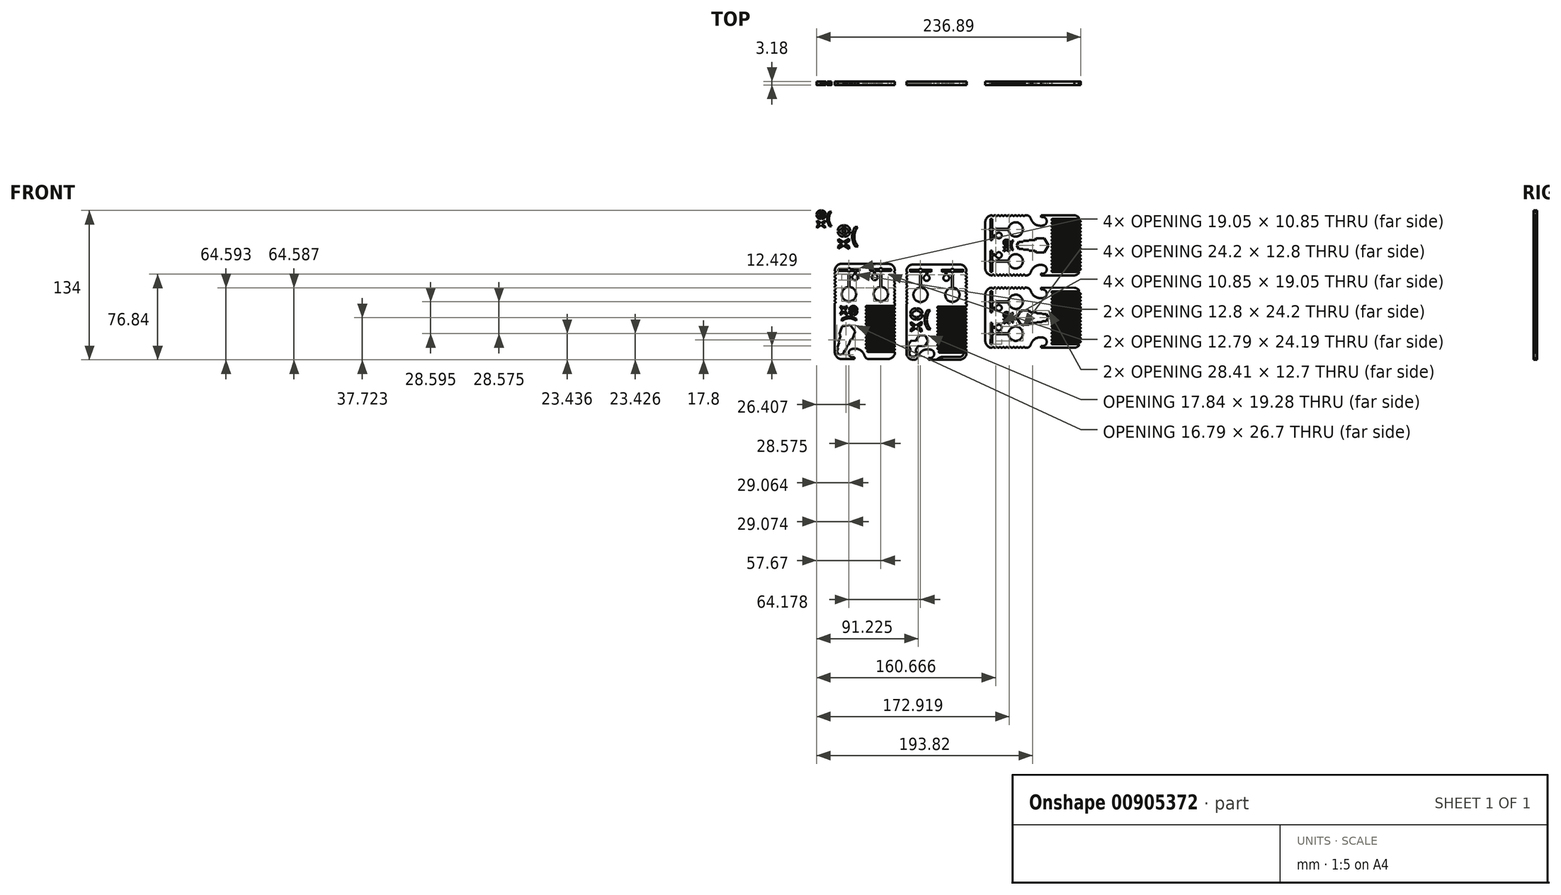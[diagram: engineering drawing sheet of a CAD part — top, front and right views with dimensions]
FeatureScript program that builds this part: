
annotation { "Feature Type Name" : "Feature", "Feature Type Description" : "" }
export const myFeature = defineFeature(function(context is Context, id is Id, definition is map)
    precondition{}
    {
        {
            var Q0;
            Q0=qCreatedBy(makeId("Front.planeOp"),FACE);
            var sketch = newSketch(context, id + "F0", { "sketchPlane" : qUnion([Q0])});
            skLineSegment(sketch, "E0.bottom", {"start": v(-20.64, 42.8) * mm, "end": v(20.64, 42.8) * mm});
            skLineSegment(sketch, "E0.top", {"start": v(-20.64, -42.8) * mm, "end": v(-20.41, -42.8) * mm});
            skLineSegment(sketch, "E0.left", {"start": v(-26.99, 34.92) * mm, "end": v(-26.99, 33.38) * mm});
            skLineSegment(sketch, "E0.right", {"start": v(26.99, 34.92) * mm, "end": v(26.99, 33.38) * mm});
            skArc(sketch, "E1.filletArc", {"start": v(-20.64, 42.8) * mm, "mid": v(-25.13, 40.94) * mm, "end": v(-26.99, 36.45) * mm});
            skArc(sketch, "E2.filletArc", {"start": v(26.99, 36.45) * mm, "mid": v(25.13, 40.94) * mm, "end": v(20.64, 42.8) * mm});
            skPoint(sketch, "E3.visualSharp", {"position": v(26.99, -42.8) * mm});
            skArc(sketch, "E3.filletArc", {"start": v(20.64, -42.8) * mm, "mid": v(24.88, -41.17) * mm, "end": v(26.95, -37.12) * mm});
            skPoint(sketch, "E4.visualSharp", {"position": v(-26.99, -42.8) * mm});
            skArc(sketch, "E4.filletArc", {"start": v(-26.99, -36.45) * mm, "mid": v(-25.13, -40.94) * mm, "end": v(-20.64, -42.8) * mm});
            skLineSegment(sketch, "E5", {"start": v(-23.81, 36.45) * mm, "end": v(-23.81, 38.04) * mm});
            skLineSegment(sketch, "E6", {"start": v(-23.81, 38.04) * mm, "end": v(-15.89, 38.04) * mm});
            skLineSegment(sketch, "E7", {"start": v(-4.76, 38.04) * mm, "end": v(-4.76, 36.45) * mm});
            skLineSegment(sketch, "E8.MirrorCS", {"start": v(4.76, 38.04) * mm, "end": v(4.76, 36.45) * mm});
            skLineSegment(sketch, "E9.MirrorCS", {"start": v(23.81, 38.04) * mm, "end": v(15.89, 38.04) * mm});
            skLineSegment(sketch, "E10.MirrorCS", {"start": v(23.81, 36.45) * mm, "end": v(23.81, 38.04) * mm});
            skLineSegment(sketch, "E11", {"start": v(-26.99, -21.76) * mm, "end": v(-26.99, -13.82) * mm});
            skLineSegment(sketch, "E12", {"start": v(-26.99, -21.76) * mm, "end": v(-26.99, -26.81) * mm});
            skLineSegment(sketch, "E13", {"start": v(-26.99, -29.7) * mm, "end": v(-26.99, -21.76) * mm});
            skPoint(sketch, "E14.orphan", {"position": v(4.76, 36.45) * mm});
            skPoint(sketch, "E15.MirrorCS.end.orphan", {"position": v(23.81, 36.45) * mm});
            skLineSegment(sketch, "E16", {"start": v(4.76, 36.45) * mm, "end": v(8.29, 36.45) * mm});
            skPoint(sketch, "E17.center.orphan", {"position": v(0, -42.8) * mm});
            skLineSegment(sketch, "E18", {"start": v(-23.81, 36.45) * mm, "end": v(-15.68, 36.45) * mm});
            skLineSegment(sketch, "E19.trimOffspring", {"start": v(-7.21, -42.8) * mm, "end": v(20.64, -42.8) * mm});
            skLineSegment(sketch, "E20.MirrorCS", {"start": v(15.06, 25.6) * mm, "end": v(15.06, 25.6) * mm});
            skLineSegment(sketch, "E21.MirrorCS", {"start": v(13.53, 25.6) * mm, "end": v(13.53, 25.6) * mm});
            skLineSegment(sketch, "E22.MirrorCS", {"start": v(13.86, 33.27) * mm, "end": v(14.75, 33.27) * mm});
            skArc(sketch, "E23", {"start": v(-8.11, 1.8) * mm, "mid": v(-10.63, -6.86) * mm, "end": v(-7.86, -15.46) * mm});
            skLineSegment(sketch, "E24.MirrorCS", {"start": v(-13.53, 25.6) * mm, "end": v(-13.53, 25.6) * mm});
            skLineSegment(sketch, "E25.MirrorCS", {"start": v(-15.06, 25.6) * mm, "end": v(-15.06, 25.6) * mm});
            skLineSegment(sketch, "E26.MirrorCS", {"start": v(-13.86, 33.27) * mm, "end": v(-14.75, 33.27) * mm});
            skArc(sketch, "E27", {"start": v(-20.67, -3.67) * mm, "mid": v(-19.53, -4.17) * mm, "end": v(-18.32, -4.4) * mm});
            skArc(sketch, "E28", {"start": v(-16.35, -4.22) * mm, "mid": v(-14.97, -3.48) * mm, "end": v(-14.3, -2.06) * mm});
            skArc(sketch, "E29", {"start": v(-23.46, -2.07) * mm, "mid": v(-23.38, -2.77) * mm, "end": v(-23.23, -3.46) * mm});
            skArc(sketch, "E30", {"start": v(-23.23, -3.46) * mm, "mid": v(-22.88, -4.33) * mm, "end": v(-22.36, -5.1) * mm});
            skArc(sketch, "E31", {"start": v(-22.36, -5.1) * mm, "mid": v(-21.57, -5.81) * mm, "end": v(-20.63, -6.31) * mm});
            skArc(sketch, "E32", {"start": v(-20.63, -6.31) * mm, "mid": v(-19.5, -6.64) * mm, "end": v(-18.32, -6.76) * mm});
            skArc(sketch, "E33", {"start": v(-18.32, -6.76) * mm, "mid": v(-18.31, -6.76) * mm, "end": v(-18.3, -6.76) * mm});
            skArc(sketch, "E34", {"start": v(-16.68, -6.69) * mm, "mid": v(-15.91, -6.55) * mm, "end": v(-15.17, -6.3) * mm});
            skArc(sketch, "E35", {"start": v(-15.17, -6.3) * mm, "mid": v(-14.58, -6.02) * mm, "end": v(-14.05, -5.65) * mm});
            skArc(sketch, "E36", {"start": v(-14.05, -5.65) * mm, "mid": v(-13.51, -5.13) * mm, "end": v(-13.08, -4.53) * mm});
            skArc(sketch, "E37", {"start": v(-13.08, -4.53) * mm, "mid": v(-12.75, -3.84) * mm, "end": v(-12.54, -3.1) * mm});
            skArc(sketch, "E38", {"start": v(-12.54, -3.1) * mm, "mid": v(-12.45, -2.62) * mm, "end": v(-12.4, -2.15) * mm});
            skArc(sketch, "E39", {"start": v(-12.4, -2.15) * mm, "mid": v(-12.4, -2.1) * mm, "end": v(-12.4, -2.06) * mm});
            skLineSegment(sketch, "E40", {"start": v(-21.55, -1.68) * mm, "end": v(-21.56, -1.68) * mm});
            skLineSegment(sketch, "E41", {"start": v(-14.29, -1.66) * mm, "end": v(-14.27, -1.66) * mm});
            skLineSegment(sketch, "E42.trimOffspring", {"start": v(-21.52, -2.06) * mm, "end": v(-23.46, -2.07) * mm});
            skLineSegment(sketch, "E43", {"start": v(-13.36, -2.06) * mm, "end": v(-12.4, -2.06) * mm});
            skArc(sketch, "E44.trimOffspring", {"start": v(-12.4, -1.66) * mm, "mid": v(-12.4, -1.65) * mm, "end": v(-12.4, -1.64) * mm});
            skLineSegment(sketch, "E45.trimOffspring", {"start": v(-14.3, -2.06) * mm, "end": v(-13.36, -2.06) * mm});
            skArc(sketch, "E46.trimOffspring", {"start": v(-21.52, -2.06) * mm, "mid": v(-21.23, -2.94) * mm, "end": v(-20.67, -3.67) * mm});
            skPoint(sketch, "E47.orphan", {"position": v(-17.78, -4.43) * mm});
            skLineSegment(sketch, "E48", {"start": v(-21.56, -1.68) * mm, "end": v(-21.55, -1.68) * mm});
            skArc(sketch, "E49.MirrorCS", {"start": v(-21.53, -1.3) * mm, "mid": v(-21.24, -0.42) * mm, "end": v(-20.68, 0.32) * mm});
            skArc(sketch, "E50.MirrorCS", {"start": v(-20.68, 0.32) * mm, "mid": v(-19.56, 0.83) * mm, "end": v(-18.35, 1.08) * mm});
            skArc(sketch, "E51.MirrorCS", {"start": v(-16.37, 0.9) * mm, "mid": v(-14.99, 0.18) * mm, "end": v(-14.3, -1.23) * mm});
            skArc(sketch, "E52.MirrorCS", {"start": v(-12.41, -1.13) * mm, "mid": v(-12.41, -1.17) * mm, "end": v(-12.4, -1.21) * mm});
            skArc(sketch, "E53.MirrorCS", {"start": v(-12.56, -0.18) * mm, "mid": v(-12.46, -0.65) * mm, "end": v(-12.41, -1.13) * mm});
            skArc(sketch, "E54.MirrorCS", {"start": v(-13.1, 1.25) * mm, "mid": v(-12.77, 0.56) * mm, "end": v(-12.56, -0.18) * mm});
            skArc(sketch, "E55.MirrorCS", {"start": v(-14.09, 2.36) * mm, "mid": v(-13.55, 1.85) * mm, "end": v(-13.1, 1.25) * mm});
            skArc(sketch, "E56.MirrorCS", {"start": v(-15.21, 3) * mm, "mid": v(-14.63, 2.72) * mm, "end": v(-14.09, 2.36) * mm});
            skArc(sketch, "E57.MirrorCS", {"start": v(-16.73, 3.37) * mm, "mid": v(-15.96, 3.24) * mm, "end": v(-15.21, 3) * mm});
            skArc(sketch, "E58.MirrorCS", {"start": v(-18.37, 3.43) * mm, "mid": v(-18.36, 3.43) * mm, "end": v(-18.36, 3.43) * mm});
            skArc(sketch, "E59.MirrorCS", {"start": v(-20.67, 2.96) * mm, "mid": v(-19.54, 3.3) * mm, "end": v(-18.37, 3.43) * mm});
            skArc(sketch, "E60.MirrorCS", {"start": v(-22.4, 1.73) * mm, "mid": v(-21.6, 2.45) * mm, "end": v(-20.67, 2.96) * mm});
            skArc(sketch, "E61.MirrorCS", {"start": v(-23.25, 0.09) * mm, "mid": v(-22.9, 0.95) * mm, "end": v(-22.4, 1.73) * mm});
            skArc(sketch, "E62.MirrorCS", {"start": v(-23.46, -1.3) * mm, "mid": v(-23.4, -0.6) * mm, "end": v(-23.25, 0.09) * mm});
            skLineSegment(sketch, "E63.MirrorCS", {"start": v(-21.53, -1.3) * mm, "end": v(-23.47, -1.3) * mm});
            skLineSegment(sketch, "E64.MirrorCS", {"start": v(-14.3, -1.23) * mm, "end": v(-13.36, -1.22) * mm});
            skLineSegment(sketch, "E65.MirrorCS", {"start": v(-13.36, -1.22) * mm, "end": v(-12.4, -1.21) * mm});
            skArc(sketch, "E66", {"start": v(-14.27, -1.66) * mm, "mid": v(-14.27, -1.65) * mm, "end": v(-14.27, -1.65) * mm});
            skLineSegment(sketch, "E67.0", {"start": v(-17.55, -6.77) * mm, "end": v(-17.56, -4.42) * mm});
            skLineSegment(sketch, "E68.0", {"start": v(-18.3, -6.77) * mm, "end": v(-18.32, -4.4) * mm});
            skLineSegment(sketch, "E69.trimOffspring", {"start": v(-18.35, 1.08) * mm, "end": v(-18.36, 3.44) * mm});
            skPoint(sketch, "E70.orphan", {"position": v(-17.93, -1.66) * mm});
            skLineSegment(sketch, "E71.trimOffspring", {"start": v(-17.58, 1.1) * mm, "end": v(-17.6, 3.45) * mm});
            skPoint(sketch, "E72.MirrorCS.end.orphan", {"position": v(-14.27, -1.64) * mm});
            skPoint(sketch, "E72.MirrorCS.start.orphan", {"position": v(-14.3, -1.23) * mm});
            skPoint(sketch, "E73.MirrorCS.end.orphan", {"position": v(-12.4, -0.88) * mm});
            skPoint(sketch, "E73.MirrorCS.start.orphan", {"position": v(-12.4, -0.45) * mm});
            skPoint(sketch, "E74.orphan", {"position": v(-23.47, -1.69) * mm});
            skPoint(sketch, "E75.MirrorCS.end.orphan", {"position": v(-21.53, -1.3) * mm});
            skArc(sketch, "E76.trimOffspring", {"start": v(-17.55, -6.77) * mm, "mid": v(-17.11, -6.74) * mm, "end": v(-16.68, -6.69) * mm});
            skArc(sketch, "E77.trimOffspring", {"start": v(-17.56, -4.42) * mm, "mid": v(-16.95, -4.35) * mm, "end": v(-16.35, -4.22) * mm});
            skArc(sketch, "E78.trimOffspring", {"start": v(-17.58, 1.1) * mm, "mid": v(-16.97, 1.03) * mm, "end": v(-16.37, 0.9) * mm});
            skArc(sketch, "E79.trimOffspring", {"start": v(-17.6, 3.44) * mm, "mid": v(-17.16, 3.42) * mm, "end": v(-16.73, 3.37) * mm});
            skText(sketch, "E80", { "text": "X", "fontName": "OpenSans-Bold.ttf"});
            skArc(sketch, "E81", {"start": v(-7.21, -41) * mm, "mid": v(-2.22, -38.57) * mm, "end": v(-4.96, -33.74) * mm});
            skArc(sketch, "E82", {"start": v(-20.41, -42.8) * mm, "mid": v(-17.8, -41.93) * mm, "end": v(-16.25, -39.67) * mm});
            skArc(sketch, "E83", {"start": v(-4.96, -33.74) * mm, "mid": v(-10.34, -33.76) * mm, "end": v(-14.8, -36.76) * mm});
            skArc(sketch, "E84", {"start": v(-14.8, -36.76) * mm, "mid": v(-15.63, -38.17) * mm, "end": v(-16.25, -39.67) * mm});
            skLineSegment(sketch, "E85", {"start": v(-7.21, -41) * mm, "end": v(-7.21, -42.8) * mm});
            skLineSegment(sketch, "E86", {"start": v(-13.54, 21.83) * mm, "end": v(-13.53, 21.83) * mm});
            skLineSegment(sketch, "E87", {"start": v(26.99, 6.39) * mm, "end": v(26.99, 7.32) * mm});
            skLineSegment(sketch, "E88", {"start": v(2.84, -34.92) * mm, "end": v(26.23, -34.92) * mm});
            skArc(sketch, "E89", {"start": v(26.23, -34.92) * mm, "mid": v(26.99, -34.16) * mm, "end": v(26.23, -33.39) * mm});
            skLineSegment(sketch, "E90", {"start": v(26.23, -33.39) * mm, "end": v(1.59, -33.39) * mm});
            skArc(sketch, "E91", {"start": v(26.95, -37.12) * mm, "mid": v(26.72, -36.65) * mm, "end": v(26.22, -36.45) * mm});
            skPoint(sketch, "E92.start.orphan", {"position": v(26.99, -36.45) * mm});
            skArc(sketch, "E93", {"start": v(2.84, -34.92) * mm, "mid": v(2.09, -35.69) * mm, "end": v(2.84, -36.45) * mm});
            skLineSegment(sketch, "E94", {"start": v(2.84, -36.45) * mm, "end": v(26.22, -36.45) * mm});
            skArc(sketch, "E95", {"start": v(1.59, -31.86) * mm, "mid": v(0.83, -32.62) * mm, "end": v(1.59, -33.39) * mm});
            skLineSegment(sketch, "E96", {"start": v(1.59, -31.86) * mm, "end": v(26.23, -31.86) * mm});
            skArc(sketch, "E97", {"start": v(26.23, -31.86) * mm, "mid": v(26.99, -31.09) * mm, "end": v(26.23, -30.32) * mm});
            skLineSegment(sketch, "E98", {"start": v(26.23, -30.32) * mm, "end": v(1.59, -30.32) * mm});
            skLineSegment(sketch, "E99", {"start": v(1.59, -28.8) * mm, "end": v(26.23, -28.8) * mm});
            skArc(sketch, "E100", {"start": v(26.23, -28.8) * mm, "mid": v(26.99, -28.02) * mm, "end": v(26.23, -27.26) * mm});
            skLineSegment(sketch, "E101", {"start": v(26.23, -27.26) * mm, "end": v(1.59, -27.26) * mm});
            skArc(sketch, "E102", {"start": v(1.59, -25.72) * mm, "mid": v(0.83, -26.5) * mm, "end": v(1.59, -27.26) * mm});
            skLineSegment(sketch, "E103", {"start": v(1.59, -25.72) * mm, "end": v(26.23, -25.72) * mm});
            skArc(sketch, "E104", {"start": v(26.23, -25.72) * mm, "mid": v(26.99, -24.96) * mm, "end": v(26.23, -24.2) * mm});
            skLineSegment(sketch, "E105", {"start": v(26.23, -24.2) * mm, "end": v(1.59, -24.2) * mm});
            skLineSegment(sketch, "E106", {"start": v(1.59, -22.66) * mm, "end": v(26.23, -22.66) * mm});
            skArc(sketch, "E107", {"start": v(26.23, -22.66) * mm, "mid": v(26.99, -21.9) * mm, "end": v(26.23, -21.13) * mm});
            skLineSegment(sketch, "E108", {"start": v(26.23, -21.13) * mm, "end": v(1.59, -21.13) * mm});
            skArc(sketch, "E109", {"start": v(1.59, -22.66) * mm, "mid": v(0.83, -23.43) * mm, "end": v(1.59, -24.2) * mm});
            skArc(sketch, "E110", {"start": v(1.59, -19.6) * mm, "mid": v(0.83, -20.36) * mm, "end": v(1.59, -21.13) * mm});
            skLineSegment(sketch, "E111", {"start": v(1.59, -19.6) * mm, "end": v(26.23, -19.6) * mm});
            skArc(sketch, "E112", {"start": v(26.23, -19.6) * mm, "mid": v(26.99, -18.83) * mm, "end": v(26.23, -18.06) * mm});
            skLineSegment(sketch, "E113", {"start": v(26.23, -18.06) * mm, "end": v(1.59, -18.06) * mm});
            skArc(sketch, "E114", {"start": v(1.59, -16.53) * mm, "mid": v(0.83, -17.3) * mm, "end": v(1.59, -18.06) * mm});
            skLineSegment(sketch, "E115", {"start": v(1.59, -16.53) * mm, "end": v(26.23, -16.53) * mm});
            skArc(sketch, "E116", {"start": v(26.23, -16.53) * mm, "mid": v(26.99, -15.76) * mm, "end": v(26.23, -15) * mm});
            skLineSegment(sketch, "E117", {"start": v(26.23, -15) * mm, "end": v(1.59, -15) * mm});
            skArc(sketch, "E118", {"start": v(1.59, -13.46) * mm, "mid": v(0.83, -14.23) * mm, "end": v(1.59, -15) * mm});
            skLineSegment(sketch, "E119", {"start": v(1.59, -13.46) * mm, "end": v(26.23, -13.46) * mm});
            skArc(sketch, "E120", {"start": v(26.23, -13.46) * mm, "mid": v(26.99, -12.7) * mm, "end": v(26.23, -11.93) * mm});
            skLineSegment(sketch, "E121", {"start": v(26.23, -11.93) * mm, "end": v(1.59, -11.93) * mm});
            skArc(sketch, "E122", {"start": v(1.59, -10.4) * mm, "mid": v(0.83, -11.16) * mm, "end": v(1.59, -11.93) * mm});
            skLineSegment(sketch, "E123", {"start": v(1.59, -10.4) * mm, "end": v(26.23, -10.4) * mm});
            skArc(sketch, "E124", {"start": v(26.23, -10.4) * mm, "mid": v(26.99, -9.63) * mm, "end": v(26.23, -8.86) * mm});
            skLineSegment(sketch, "E125", {"start": v(26.23, -8.86) * mm, "end": v(1.59, -8.86) * mm});
            skArc(sketch, "E126", {"start": v(1.59, -7.33) * mm, "mid": v(0.83, -8.1) * mm, "end": v(1.59, -8.86) * mm});
            skLineSegment(sketch, "E127", {"start": v(1.59, -7.33) * mm, "end": v(26.23, -7.33) * mm});
            skArc(sketch, "E128", {"start": v(26.23, -7.33) * mm, "mid": v(26.99, -6.56) * mm, "end": v(26.23, -5.8) * mm});
            skLineSegment(sketch, "E129", {"start": v(26.23, -5.8) * mm, "end": v(1.59, -5.8) * mm});
            skArc(sketch, "E130", {"start": v(1.59, -4.26) * mm, "mid": v(0.83, -5.03) * mm, "end": v(1.59, -5.8) * mm});
            skLineSegment(sketch, "E131", {"start": v(1.59, -4.26) * mm, "end": v(26.23, -4.26) * mm});
            skArc(sketch, "E132", {"start": v(26.23, -4.26) * mm, "mid": v(26.99, -3.5) * mm, "end": v(26.23, -2.73) * mm});
            skLineSegment(sketch, "E133", {"start": v(26.23, -2.73) * mm, "end": v(1.59, -2.73) * mm});
            skArc(sketch, "E134", {"start": v(1.59, -1.2) * mm, "mid": v(0.83, -1.97) * mm, "end": v(1.59, -2.73) * mm});
            skLineSegment(sketch, "E135", {"start": v(1.59, -1.2) * mm, "end": v(26.23, -1.2) * mm});
            skArc(sketch, "E136", {"start": v(26.23, -1.2) * mm, "mid": v(26.99, -0.43) * mm, "end": v(26.23, 0.33) * mm});
            skLineSegment(sketch, "E137", {"start": v(26.23, 0.33) * mm, "end": v(1.59, 0.33) * mm});
            skArc(sketch, "E138", {"start": v(1.59, 1.87) * mm, "mid": v(0.83, 1.1) * mm, "end": v(1.59, 0.33) * mm});
            skLineSegment(sketch, "E139", {"start": v(1.59, 1.87) * mm, "end": v(26.23, 1.87) * mm});
            skArc(sketch, "E140", {"start": v(26.23, 1.87) * mm, "mid": v(26.99, 2.63) * mm, "end": v(26.23, 3.4) * mm});
            skLineSegment(sketch, "E141", {"start": v(26.23, 3.4) * mm, "end": v(1.59, 3.4) * mm});
            skArc(sketch, "E142", {"start": v(1.59, 4.93) * mm, "mid": v(0.83, 4.17) * mm, "end": v(1.59, 3.4) * mm});
            skLineSegment(sketch, "E143", {"start": v(1.59, 4.93) * mm, "end": v(26.23, 4.93) * mm});
            skArc(sketch, "E144", {"start": v(26.23, 4.93) * mm, "mid": v(26.77, 5.16) * mm, "end": v(26.99, 5.7) * mm});
            skLineSegment(sketch, "E145", {"start": v(26.99, 5.7) * mm, "end": v(26.99, 6.39) * mm});
            skLineSegment(sketch, "E146.0", {"start": v(-14.75, 33.27) * mm, "end": v(-14.75, 22.45) * mm});
            skLineSegment(sketch, "E147.0", {"start": v(-13.86, 33.27) * mm, "end": v(-13.86, 22.45) * mm});
            skLineSegment(sketch, "E148.0", {"start": v(13.86, 33.27) * mm, "end": v(13.86, 22.45) * mm});
            skLineSegment(sketch, "E149.0", {"start": v(14.75, 33.27) * mm, "end": v(14.75, 22.45) * mm});
            skArc(sketch, "E150", {"start": v(13.3, 21.82) * mm, "mid": v(14.33, 9.08) * mm, "end": v(15.27, 21.83) * mm});
            skArc(sketch, "E151", {"start": v(-15.3, 21.82) * mm, "mid": v(-14.28, 9.07) * mm, "end": v(-13.32, 21.83) * mm});
            skArc(sketch, "E152", {"start": v(-26.99, 7.32) * mm, "mid": v(-26.23, 8.1) * mm, "end": v(-26.99, 8.86) * mm});
            skArc(sketch, "E153", {"start": v(-26.99, 10.4) * mm, "mid": v(-26.23, 11.16) * mm, "end": v(-26.99, 11.92) * mm});
            skArc(sketch, "E154", {"start": v(-26.99, 13.46) * mm, "mid": v(-26.23, 14.22) * mm, "end": v(-26.99, 14.99) * mm});
            skArc(sketch, "E155", {"start": v(-26.99, 16.52) * mm, "mid": v(-26.23, 17.29) * mm, "end": v(-26.99, 18.05) * mm});
            skArc(sketch, "E156", {"start": v(-26.99, 19.59) * mm, "mid": v(-26.23, 20.35) * mm, "end": v(-26.99, 21.12) * mm});
            skArc(sketch, "E157", {"start": v(-26.99, 22.65) * mm, "mid": v(-26.23, 23.42) * mm, "end": v(-26.99, 24.19) * mm});
            skArc(sketch, "E158", {"start": v(-26.99, 25.72) * mm, "mid": v(-26.23, 26.49) * mm, "end": v(-26.99, 27.25) * mm});
            skArc(sketch, "E159", {"start": v(-26.99, 28.78) * mm, "mid": v(-26.23, 29.55) * mm, "end": v(-26.99, 30.32) * mm});
            skArc(sketch, "E160", {"start": v(-26.99, 31.85) * mm, "mid": v(-26.23, 32.62) * mm, "end": v(-26.99, 33.38) * mm});
            skArc(sketch, "E161", {"start": v(-26.99, 34.92) * mm, "mid": v(-26.23, 35.68) * mm, "end": v(-26.99, 36.45) * mm});
            skArc(sketch, "E162", {"start": v(26.99, 8.86) * mm, "mid": v(26.23, 8.1) * mm, "end": v(26.99, 7.32) * mm});
            skArc(sketch, "E163", {"start": v(26.99, 11.92) * mm, "mid": v(26.23, 11.16) * mm, "end": v(26.99, 10.4) * mm});
            skArc(sketch, "E164", {"start": v(26.99, 14.99) * mm, "mid": v(26.23, 14.22) * mm, "end": v(26.99, 13.46) * mm});
            skArc(sketch, "E165", {"start": v(26.99, 18.05) * mm, "mid": v(26.23, 17.29) * mm, "end": v(26.99, 16.52) * mm});
            skArc(sketch, "E166", {"start": v(26.99, 21.12) * mm, "mid": v(26.23, 20.35) * mm, "end": v(26.99, 19.59) * mm});
            skArc(sketch, "E167", {"start": v(26.99, 24.19) * mm, "mid": v(26.23, 23.42) * mm, "end": v(26.99, 22.65) * mm});
            skArc(sketch, "E168", {"start": v(26.99, 27.25) * mm, "mid": v(26.23, 26.49) * mm, "end": v(26.99, 25.72) * mm});
            skArc(sketch, "E169", {"start": v(26.99, 30.32) * mm, "mid": v(26.23, 29.55) * mm, "end": v(26.99, 28.78) * mm});
            skArc(sketch, "E170", {"start": v(26.99, 33.38) * mm, "mid": v(26.23, 32.62) * mm, "end": v(26.99, 31.85) * mm});
            skArc(sketch, "E171", {"start": v(26.99, 36.45) * mm, "mid": v(26.23, 35.68) * mm, "end": v(26.99, 34.92) * mm});
            skLineSegment(sketch, "E172.trimOffspring", {"start": v(-26.99, 7.32) * mm, "end": v(-26.99, -36.45) * mm});
            skLineSegment(sketch, "E173.trimOffspring", {"start": v(-26.99, 10.4) * mm, "end": v(-26.99, 8.86) * mm});
            skLineSegment(sketch, "E174.trimOffspring", {"start": v(-26.99, 13.46) * mm, "end": v(-26.99, 11.92) * mm});
            skLineSegment(sketch, "E175.trimOffspring", {"start": v(-26.99, 16.52) * mm, "end": v(-26.99, 14.99) * mm});
            skLineSegment(sketch, "E176.trimOffspring", {"start": v(-26.99, 19.59) * mm, "end": v(-26.99, 18.05) * mm});
            skLineSegment(sketch, "E177.trimOffspring", {"start": v(-26.99, 22.65) * mm, "end": v(-26.99, 21.12) * mm});
            skLineSegment(sketch, "E178.trimOffspring", {"start": v(-26.99, 25.72) * mm, "end": v(-26.99, 24.19) * mm});
            skLineSegment(sketch, "E179.trimOffspring", {"start": v(-26.99, 28.78) * mm, "end": v(-26.99, 27.25) * mm});
            skLineSegment(sketch, "E180.trimOffspring", {"start": v(-26.99, 31.85) * mm, "end": v(-26.99, 30.32) * mm});
            skLineSegment(sketch, "E181.trimOffspring", {"start": v(26.99, 31.85) * mm, "end": v(26.99, 30.32) * mm});
            skLineSegment(sketch, "E182.trimOffspring", {"start": v(26.99, 28.78) * mm, "end": v(26.99, 27.25) * mm});
            skLineSegment(sketch, "E183.trimOffspring", {"start": v(26.99, 25.72) * mm, "end": v(26.99, 24.19) * mm});
            skLineSegment(sketch, "E184.trimOffspring", {"start": v(26.99, 22.65) * mm, "end": v(26.99, 21.12) * mm});
            skLineSegment(sketch, "E185.trimOffspring", {"start": v(26.99, 19.59) * mm, "end": v(26.99, 18.05) * mm});
            skLineSegment(sketch, "E186.trimOffspring", {"start": v(26.99, 16.52) * mm, "end": v(26.99, 14.99) * mm});
            skLineSegment(sketch, "E187.trimOffspring", {"start": v(26.99, 13.46) * mm, "end": v(26.99, 11.92) * mm});
            skLineSegment(sketch, "E188.trimOffspring", {"start": v(26.99, 10.4) * mm, "end": v(26.99, 8.86) * mm});
            skLineSegment(sketch, "E189", {"start": v(-5.59, 1.8) * mm, "end": v(-8.11, 1.8) * mm});
            skLineSegment(sketch, "E190", {"start": v(-8.11, 1.8) * mm, "end": v(-5.59, 1.8) * mm});
            skPoint(sketch, "E191.orphan", {"position": v(-14.3, 33.27) * mm});
            skLineSegment(sketch, "E192.trimOffspring", {"start": v(-12.71, 38.04) * mm, "end": v(-4.76, 38.04) * mm});
            skPoint(sketch, "E193.endSnap0", {"position": v(14.29, 38.04) * mm});
            skLineSegment(sketch, "E194.trimOffspring", {"start": v(12.71, 38.04) * mm, "end": v(4.76, 38.04) * mm});
            skLineSegment(sketch, "E195.trimOffspring", {"start": v(14.3, 38.04) * mm, "end": v(14.29, 38.04) * mm});
            skPoint(sketch, "E193.start.orphan", {"position": v(14.3, 33.27) * mm});
            skLineSegment(sketch, "E196", {"start": v(12.71, 38.04) * mm, "end": v(12.9, 38.04) * mm});
            skArc(sketch, "E197", {"start": v(15.68, 38.04) * mm, "mid": v(14.29, 38.84) * mm, "end": v(12.9, 38.04) * mm});
            skLineSegment(sketch, "E198.trimOffspring", {"start": v(14.29, 38.04) * mm, "end": v(14.3, 38.04) * mm});
            skLineSegment(sketch, "E199.trimOffspring", {"start": v(15.68, 38.04) * mm, "end": v(15.89, 38.04) * mm});
            skPoint(sketch, "E200.end.orphan", {"position": v(14.3, 36.45) * mm});
            skLineSegment(sketch, "E201.trimOffspring", {"start": v(15.68, 36.45) * mm, "end": v(23.81, 36.45) * mm});
            skArc(sketch, "E202.trimOffspring", {"start": v(12.9, 36.45) * mm, "mid": v(14.29, 35.64) * mm, "end": v(15.68, 36.45) * mm});
            skLineSegment(sketch, "E203", {"start": v(-15.89, 38.04) * mm, "end": v(-15.68, 38.04) * mm});
            skPoint(sketch, "E204.orphan", {"position": v(8.83, 36.45) * mm});
            skPoint(sketch, "E205.start.orphan", {"position": v(8.83, 33.27) * mm});
            skLineSegment(sketch, "E206.trimOffspring", {"start": v(9.28, 36.45) * mm, "end": v(12.9, 36.45) * mm});
            skArc(sketch, "E207.MirrorCS", {"start": v(-15.68, 38.04) * mm, "mid": v(-14.29, 38.84) * mm, "end": v(-12.9, 38.04) * mm});
            skArc(sketch, "E208.MirrorCS", {"start": v(-12.9, 36.45) * mm, "mid": v(-14.29, 35.64) * mm, "end": v(-15.68, 36.45) * mm});
            skPoint(sketch, "E209.start.orphan", {"position": v(0, 42.8) * mm});
            skLineSegment(sketch, "E210.trimOffspring", {"start": v(-12.9, 36.45) * mm, "end": v(-9.28, 36.45) * mm});
            skLineSegment(sketch, "E211.trimOffspring", {"start": v(-12.9, 38.04) * mm, "end": v(-12.71, 38.04) * mm});
            skLineSegment(sketch, "E212.trimOffspring", {"start": v(-8.29, 36.45) * mm, "end": v(-4.76, 36.45) * mm});
            skArc(sketch, "E213", {"start": v(-9.9, 33.04) * mm, "mid": v(-8.95, 34.63) * mm, "end": v(-9.28, 36.45) * mm});
            skArc(sketch, "E214.0", {"start": v(-8.4, 33.52) * mm, "mid": v(-8.02, 34.97) * mm, "end": v(-8.29, 36.45) * mm});
            skArc(sketch, "E215.MirrorCS", {"start": v(8.4, 33.52) * mm, "mid": v(8.02, 34.97) * mm, "end": v(8.29, 36.45) * mm});
            skArc(sketch, "E216.MirrorCS", {"start": v(9.9, 33.04) * mm, "mid": v(8.95, 34.63) * mm, "end": v(9.28, 36.45) * mm});
            skArc(sketch, "E217.MirrorCS", {"start": v(9.9, 33.04) * mm, "mid": v(8.58, 28) * mm, "end": v(8.25, 33.2) * mm});
            skPoint(sketch, "E218.orphan", {"position": v(9.94, 33.02) * mm});
            skPoint(sketch, "E219.start.orphan", {"position": v(-9.9, 33.04) * mm});
            skArc(sketch, "E220.MirrorCS", {"start": v(-9.9, 33.04) * mm, "mid": v(-8.58, 28) * mm, "end": v(-8.25, 33.2) * mm});
            skPoint(sketch, "E221.orphan", {"position": v(-9.94, 33.02) * mm});
            skArc(sketch, "E222.0", {"start": v(-5.59, 1.8) * mm, "mid": v(-8.59, -6.88) * mm, "end": v(-5.28, -15.46) * mm});
            skLineSegment(sketch, "E223", {"start": v(-7.86, -15.46) * mm, "end": v(-5.28, -15.46) * mm});
            skArc(sketch, "E224", {"start": v(-15.3, 21.82) * mm, "mid": v(-14.92, 22.04) * mm, "end": v(-14.75, 22.45) * mm});
            skArc(sketch, "E225.MirrorCS", {"start": v(-13.3, 21.82) * mm, "mid": v(-13.69, 22.04) * mm, "end": v(-13.86, 22.45) * mm});
            skArc(sketch, "E226.MirrorCS", {"start": v(15.3, 21.82) * mm, "mid": v(14.92, 22.04) * mm, "end": v(14.75, 22.45) * mm});
            skArc(sketch, "E227.MirrorCS", {"start": v(13.3, 21.82) * mm, "mid": v(13.69, 22.04) * mm, "end": v(13.86, 22.45) * mm});
            skArc(sketch, "E228", {"start": v(-8.4, 33.52) * mm, "mid": v(-8.4, 33.33) * mm, "end": v(-8.25, 33.2) * mm});
            skArc(sketch, "E229.MirrorCS", {"start": v(8.4, 33.52) * mm, "mid": v(8.4, 33.33) * mm, "end": v(8.25, 33.2) * mm});
            skArc(sketch, "E230", {"start": v(1.59, -28.8) * mm, "mid": v(0.83, -29.56) * mm, "end": v(1.59, -30.32) * mm});
            skPoint(sketch, "E231", {"position": v(13.9, -5.8) * mm});
            skPoint(sketch, "E232", {"position": v(-26.99, -17.79) * mm});
            skLineSegment(sketch, "E233.0", {"start": v(-24.67, -36.57) * mm, "end": v(-22.93, -33.87) * mm});
            skLineSegment(sketch, "E233.2", {"start": v(-18.8, -34.08) * mm, "end": v(-17.34, -36.93) * mm});
            skLineSegment(sketch, "E233.3", {"start": v(-17.34, -36.93) * mm, "end": v(-19.33, -40) * mm});
            skLineSegment(sketch, "E233.4", {"start": v(-19.33, -40) * mm, "end": v(-23, -39.83) * mm});
            skLineSegment(sketch, "E233.5", {"start": v(-23, -39.83) * mm, "end": v(-24.67, -36.57) * mm});
            skLineSegment(sketch, "E234.0", {"start": v(-25.23, -29.39) * mm, "end": v(-22.75, -25.54) * mm});
            skLineSegment(sketch, "E234.1", {"start": v(-22.75, -25.54) * mm, "end": v(-18.63, -25.74) * mm});
            skLineSegment(sketch, "E234.3", {"start": v(-16.33, -30.22) * mm, "end": v(-18.8, -34.08) * mm});
            skLineSegment(sketch, "E234.5", {"start": v(-22.93, -33.87) * mm, "end": v(-25.23, -29.39) * mm});
            skLineSegment(sketch, "E235.0", {"start": v(-18.63, -25.74) * mm, "end": v(-15.4, -20.73) * mm});
            skLineSegment(sketch, "E235.1", {"start": v(-15.4, -20.73) * mm, "end": v(-9.91, -21) * mm});
            skLineSegment(sketch, "E235.2", {"start": v(-9.91, -21) * mm, "end": v(-7.4, -25.9) * mm});
            skLineSegment(sketch, "E235.3", {"start": v(-7.4, -25.9) * mm, "end": v(-10.38, -30.51) * mm});
            skLineSegment(sketch, "E235.4", {"start": v(-10.38, -30.51) * mm, "end": v(-16.33, -30.22) * mm});
            skArc(sketch, "E236", {"start": v(-73.14, 76.21) * mm, "mid": v(-75.66, 67.54) * mm, "end": v(-72.89, 58.95) * mm});
            skArc(sketch, "E237", {"start": v(-85.69, 70.74) * mm, "mid": v(-84.56, 70.24) * mm, "end": v(-83.34, 70) * mm});
            skArc(sketch, "E238", {"start": v(-81.37, 70.2) * mm, "mid": v(-80, 70.93) * mm, "end": v(-79.33, 72.34) * mm});
            skArc(sketch, "E239", {"start": v(-88.48, 72.34) * mm, "mid": v(-88.4, 71.63) * mm, "end": v(-88.25, 70.94) * mm});
            skArc(sketch, "E240", {"start": v(-88.25, 70.94) * mm, "mid": v(-87.9, 70.08) * mm, "end": v(-87.39, 69.31) * mm});
            skArc(sketch, "E241", {"start": v(-87.39, 69.31) * mm, "mid": v(-86.6, 68.6) * mm, "end": v(-85.65, 68.1) * mm});
            skArc(sketch, "E242", {"start": v(-85.65, 68.1) * mm, "mid": v(-84.52, 67.77) * mm, "end": v(-83.34, 67.65) * mm});
            skArc(sketch, "E243", {"start": v(-83.34, 67.65) * mm, "mid": v(-83.34, 67.65) * mm, "end": v(-83.33, 67.65) * mm});
            skArc(sketch, "E244", {"start": v(-81.7, 67.72) * mm, "mid": v(-80.94, 67.86) * mm, "end": v(-80.2, 68.1) * mm});
            skArc(sketch, "E245", {"start": v(-80.2, 68.1) * mm, "mid": v(-79.6, 68.39) * mm, "end": v(-79.07, 68.76) * mm});
            skArc(sketch, "E246", {"start": v(-79.07, 68.76) * mm, "mid": v(-78.54, 69.27) * mm, "end": v(-78.1, 69.88) * mm});
            skArc(sketch, "E247", {"start": v(-78.1, 69.88) * mm, "mid": v(-77.77, 70.57) * mm, "end": v(-77.57, 71.31) * mm});
            skArc(sketch, "E248", {"start": v(-77.57, 71.31) * mm, "mid": v(-77.48, 71.78) * mm, "end": v(-77.43, 72.26) * mm});
            skArc(sketch, "E249", {"start": v(-77.43, 72.26) * mm, "mid": v(-77.43, 72.3) * mm, "end": v(-77.43, 72.34) * mm});
            skLineSegment(sketch, "E250", {"start": v(-86.58, 72.73) * mm, "end": v(-86.59, 72.73) * mm});
            skLineSegment(sketch, "E251", {"start": v(-79.3, 72.75) * mm, "end": v(-79.3, 72.75) * mm});
            skLineSegment(sketch, "E252.trimOffspring", {"start": v(-86.55, 72.34) * mm, "end": v(-88.49, 72.34) * mm});
            skLineSegment(sketch, "E253", {"start": v(-78.38, 72.34) * mm, "end": v(-77.43, 72.34) * mm});
            skArc(sketch, "E254.trimOffspring", {"start": v(-77.41, 72.75) * mm, "mid": v(-77.41, 72.76) * mm, "end": v(-77.41, 72.77) * mm});
            skLineSegment(sketch, "E255.trimOffspring", {"start": v(-79.33, 72.34) * mm, "end": v(-78.38, 72.34) * mm});
            skArc(sketch, "E256.trimOffspring", {"start": v(-86.55, 72.34) * mm, "mid": v(-86.25, 71.47) * mm, "end": v(-85.69, 70.74) * mm});
            skPoint(sketch, "E257.orphan", {"position": v(-82.8, 69.98) * mm});
            skLineSegment(sketch, "E258", {"start": v(-86.59, 72.73) * mm, "end": v(-86.58, 72.73) * mm});
            skArc(sketch, "E259.MirrorCS", {"start": v(-86.55, 73.1) * mm, "mid": v(-86.27, 73.99) * mm, "end": v(-85.7, 74.73) * mm});
            skArc(sketch, "E260.MirrorCS", {"start": v(-85.7, 74.73) * mm, "mid": v(-84.58, 75.24) * mm, "end": v(-83.37, 75.48) * mm});
            skArc(sketch, "E261.MirrorCS", {"start": v(-81.4, 75.31) * mm, "mid": v(-80.01, 74.59) * mm, "end": v(-79.33, 73.18) * mm});
            skArc(sketch, "E262.MirrorCS", {"start": v(-77.44, 73.28) * mm, "mid": v(-77.43, 73.24) * mm, "end": v(-77.43, 73.2) * mm});
            skArc(sketch, "E263.MirrorCS", {"start": v(-77.58, 74.23) * mm, "mid": v(-77.49, 73.76) * mm, "end": v(-77.44, 73.28) * mm});
            skArc(sketch, "E264.MirrorCS", {"start": v(-78.13, 75.66) * mm, "mid": v(-77.8, 74.97) * mm, "end": v(-77.58, 74.23) * mm});
            skArc(sketch, "E265.MirrorCS", {"start": v(-79.11, 76.77) * mm, "mid": v(-78.57, 76.26) * mm, "end": v(-78.13, 75.66) * mm});
            skArc(sketch, "E266.MirrorCS", {"start": v(-80.24, 77.4) * mm, "mid": v(-79.65, 77.13) * mm, "end": v(-79.11, 76.77) * mm});
            skArc(sketch, "E267.MirrorCS", {"start": v(-81.76, 77.78) * mm, "mid": v(-80.98, 77.64) * mm, "end": v(-80.24, 77.4) * mm});
            skArc(sketch, "E268.MirrorCS", {"start": v(-83.39, 77.84) * mm, "mid": v(-83.39, 77.84) * mm, "end": v(-83.38, 77.84) * mm});
            skArc(sketch, "E269.MirrorCS", {"start": v(-85.7, 77.37) * mm, "mid": v(-84.56, 77.7) * mm, "end": v(-83.39, 77.84) * mm});
            skArc(sketch, "E270.MirrorCS", {"start": v(-87.42, 76.13) * mm, "mid": v(-86.63, 76.86) * mm, "end": v(-85.7, 77.37) * mm});
            skArc(sketch, "E271.MirrorCS", {"start": v(-88.27, 74.5) * mm, "mid": v(-87.93, 75.36) * mm, "end": v(-87.42, 76.13) * mm});
            skArc(sketch, "E272.MirrorCS", {"start": v(-88.48, 73.1) * mm, "mid": v(-88.41, 73.8) * mm, "end": v(-88.27, 74.5) * mm});
            skLineSegment(sketch, "E273.MirrorCS", {"start": v(-86.55, 73.1) * mm, "end": v(-88.5, 73.1) * mm});
            skLineSegment(sketch, "E274.MirrorCS", {"start": v(-79.33, 73.18) * mm, "end": v(-78.39, 73.19) * mm});
            skLineSegment(sketch, "E275.MirrorCS", {"start": v(-78.39, 73.19) * mm, "end": v(-77.43, 73.2) * mm});
            skArc(sketch, "E276", {"start": v(-79.3, 72.75) * mm, "mid": v(-79.3, 72.76) * mm, "end": v(-79.3, 72.76) * mm});
            skLineSegment(sketch, "E277.0", {"start": v(-82.57, 67.64) * mm, "end": v(-82.58, 70) * mm});
            skLineSegment(sketch, "E278.0", {"start": v(-83.33, 67.63) * mm, "end": v(-83.34, 70) * mm});
            skLineSegment(sketch, "E279.trimOffspring", {"start": v(-83.37, 75.48) * mm, "end": v(-83.38, 77.85) * mm});
            skPoint(sketch, "E280.orphan", {"position": v(-82.95, 72.74) * mm});
            skLineSegment(sketch, "E281.trimOffspring", {"start": v(-82.6, 75.5) * mm, "end": v(-82.62, 77.85) * mm});
            skPoint(sketch, "E282.MirrorCS.end.orphan", {"position": v(-79.3, 72.77) * mm});
            skPoint(sketch, "E282.MirrorCS.start.orphan", {"position": v(-79.33, 73.18) * mm});
            skPoint(sketch, "E283.MirrorCS.end.orphan", {"position": v(-77.41, 73.53) * mm});
            skPoint(sketch, "E283.MirrorCS.start.orphan", {"position": v(-77.43, 73.96) * mm});
            skPoint(sketch, "E284.orphan", {"position": v(-88.49, 72.72) * mm});
            skPoint(sketch, "E285.MirrorCS.end.orphan", {"position": v(-86.55, 73.1) * mm});
            skArc(sketch, "E286.trimOffspring", {"start": v(-82.57, 67.64) * mm, "mid": v(-82.14, 67.67) * mm, "end": v(-81.7, 67.72) * mm});
            skArc(sketch, "E287.trimOffspring", {"start": v(-82.58, 70) * mm, "mid": v(-81.97, 70.06) * mm, "end": v(-81.37, 70.2) * mm});
            skArc(sketch, "E288.trimOffspring", {"start": v(-82.6, 75.5) * mm, "mid": v(-82, 75.44) * mm, "end": v(-81.4, 75.31) * mm});
            skArc(sketch, "E289.trimOffspring", {"start": v(-82.62, 77.85) * mm, "mid": v(-82.19, 77.83) * mm, "end": v(-81.76, 77.78) * mm});
            skText(sketch, "E290", { "text": "X", "fontName": "OpenSans-Bold.ttf"});
            skLineSegment(sketch, "E291", {"start": v(-70.61, 76.21) * mm, "end": v(-73.14, 76.21) * mm});
            skLineSegment(sketch, "E292", {"start": v(-73.14, 76.21) * mm, "end": v(-70.61, 76.21) * mm});
            skCircle(sketch, "E293", {"center": v(-82.95, 72.74) * mm, "radius": 1.3 * mm});
            skArc(sketch, "E294.0", {"start": v(-70.61, 76.21) * mm, "mid": v(-73.61, 67.53) * mm, "end": v(-70.3, 58.95) * mm});
            skLineSegment(sketch, "E295", {"start": v(-72.89, 58.95) * mm, "end": v(-70.3, 58.95) * mm});
            skPoint(sketch, "E296", {"position": v(-17.8, -41.93) * mm});
            skArc(sketch, "E297", {"start": v(-96.1, 89.98) * mm, "mid": v(-97.99, 83.52) * mm, "end": v(-95.93, 77.12) * mm});
            skArc(sketch, "E298", {"start": v(-105.46, 85.9) * mm, "mid": v(-104.62, 85.53) * mm, "end": v(-103.71, 85.35) * mm});
            skArc(sketch, "E299", {"start": v(-102.25, 85.5) * mm, "mid": v(-101.22, 86.05) * mm, "end": v(-100.72, 87.1) * mm});
            skArc(sketch, "E300", {"start": v(-107.54, 87.1) * mm, "mid": v(-107.48, 86.57) * mm, "end": v(-107.37, 86.06) * mm});
            skArc(sketch, "E301", {"start": v(-107.37, 86.06) * mm, "mid": v(-107.11, 85.41) * mm, "end": v(-106.72, 84.84) * mm});
            skArc(sketch, "E302", {"start": v(-106.72, 84.84) * mm, "mid": v(-106.13, 84.3) * mm, "end": v(-105.43, 83.93) * mm});
            skArc(sketch, "E303", {"start": v(-105.43, 83.93) * mm, "mid": v(-104.59, 83.7) * mm, "end": v(-103.71, 83.6) * mm});
            skArc(sketch, "E304", {"start": v(-103.71, 83.6) * mm, "mid": v(-103.7, 83.6) * mm, "end": v(-103.7, 83.6) * mm});
            skArc(sketch, "E305", {"start": v(-102.5, 83.65) * mm, "mid": v(-101.92, 83.76) * mm, "end": v(-101.37, 83.94) * mm});
            skArc(sketch, "E306", {"start": v(-101.37, 83.94) * mm, "mid": v(-100.93, 84.15) * mm, "end": v(-100.53, 84.43) * mm});
            skArc(sketch, "E307", {"start": v(-100.53, 84.43) * mm, "mid": v(-100.13, 84.81) * mm, "end": v(-99.8, 85.26) * mm});
            skArc(sketch, "E308", {"start": v(-99.8, 85.26) * mm, "mid": v(-99.56, 85.78) * mm, "end": v(-99.4, 86.33) * mm});
            skArc(sketch, "E309", {"start": v(-99.4, 86.33) * mm, "mid": v(-99.34, 86.68) * mm, "end": v(-99.31, 87.04) * mm});
            skArc(sketch, "E310", {"start": v(-99.31, 87.04) * mm, "mid": v(-99.3, 87.07) * mm, "end": v(-99.3, 87.1) * mm});
            skLineSegment(sketch, "E311", {"start": v(-106.12, 87.38) * mm, "end": v(-106.13, 87.38) * mm});
            skLineSegment(sketch, "E312", {"start": v(-100.7, 87.4) * mm, "end": v(-100.7, 87.4) * mm});
            skLineSegment(sketch, "E313.trimOffspring", {"start": v(-106.1, 87.1) * mm, "end": v(-107.54, 87.1) * mm});
            skLineSegment(sketch, "E314", {"start": v(-100.02, 87.1) * mm, "end": v(-99.3, 87.1) * mm});
            skArc(sketch, "E315.trimOffspring", {"start": v(-99.3, 87.4) * mm, "mid": v(-99.3, 87.4) * mm, "end": v(-99.3, 87.42) * mm});
            skLineSegment(sketch, "E316.trimOffspring", {"start": v(-100.72, 87.1) * mm, "end": v(-100.02, 87.1) * mm});
            skArc(sketch, "E317.trimOffspring", {"start": v(-106.1, 87.1) * mm, "mid": v(-105.88, 86.45) * mm, "end": v(-105.46, 85.9) * mm});
            skPoint(sketch, "E318.orphan", {"position": v(-103.31, 85.34) * mm});
            skLineSegment(sketch, "E319", {"start": v(-106.13, 87.38) * mm, "end": v(-106.12, 87.38) * mm});
            skArc(sketch, "E320.MirrorCS", {"start": v(-106.1, 87.67) * mm, "mid": v(-105.89, 88.32) * mm, "end": v(-105.47, 88.87) * mm});
            skArc(sketch, "E321.MirrorCS", {"start": v(-105.47, 88.87) * mm, "mid": v(-104.64, 89.25) * mm, "end": v(-103.73, 89.44) * mm});
            skArc(sketch, "E322.MirrorCS", {"start": v(-102.26, 89.3) * mm, "mid": v(-101.23, 88.77) * mm, "end": v(-100.72, 87.72) * mm});
            skArc(sketch, "E323.MirrorCS", {"start": v(-99.31, 87.8) * mm, "mid": v(-99.31, 87.76) * mm, "end": v(-99.3, 87.73) * mm});
            skArc(sketch, "E324.MirrorCS", {"start": v(-99.42, 88.5) * mm, "mid": v(-99.35, 88.15) * mm, "end": v(-99.31, 87.8) * mm});
            skArc(sketch, "E325.MirrorCS", {"start": v(-99.83, 89.57) * mm, "mid": v(-99.58, 89.05) * mm, "end": v(-99.42, 88.5) * mm});
            skArc(sketch, "E326.MirrorCS", {"start": v(-100.56, 90.4) * mm, "mid": v(-100.16, 90.01) * mm, "end": v(-99.83, 89.57) * mm});
            skArc(sketch, "E327.MirrorCS", {"start": v(-101.4, 90.87) * mm, "mid": v(-100.96, 90.66) * mm, "end": v(-100.56, 90.4) * mm});
            skArc(sketch, "E328.MirrorCS", {"start": v(-102.53, 91.15) * mm, "mid": v(-101.95, 91.05) * mm, "end": v(-101.4, 90.87) * mm});
            skArc(sketch, "E329.MirrorCS", {"start": v(-103.75, 91.19) * mm, "mid": v(-103.74, 91.19) * mm, "end": v(-103.74, 91.19) * mm});
            skArc(sketch, "E330.MirrorCS", {"start": v(-105.46, 90.84) * mm, "mid": v(-104.62, 91.1) * mm, "end": v(-103.75, 91.19) * mm});
            skArc(sketch, "E331.MirrorCS", {"start": v(-106.75, 89.92) * mm, "mid": v(-106.16, 90.46) * mm, "end": v(-105.46, 90.84) * mm});
            skArc(sketch, "E332.MirrorCS", {"start": v(-107.38, 88.7) * mm, "mid": v(-107.13, 89.35) * mm, "end": v(-106.75, 89.92) * mm});
            skArc(sketch, "E333.MirrorCS", {"start": v(-107.54, 87.66) * mm, "mid": v(-107.5, 88.19) * mm, "end": v(-107.38, 88.7) * mm});
            skLineSegment(sketch, "E334.MirrorCS", {"start": v(-106.1, 87.67) * mm, "end": v(-107.55, 87.66) * mm});
            skLineSegment(sketch, "E335.MirrorCS", {"start": v(-100.72, 87.72) * mm, "end": v(-100.02, 87.73) * mm});
            skLineSegment(sketch, "E336.MirrorCS", {"start": v(-100.02, 87.73) * mm, "end": v(-99.3, 87.73) * mm});
            skArc(sketch, "E337", {"start": v(-100.7, 87.4) * mm, "mid": v(-100.7, 87.4) * mm, "end": v(-100.7, 87.4) * mm});
            skLineSegment(sketch, "E338.0", {"start": v(-103.14, 83.6) * mm, "end": v(-103.15, 85.35) * mm});
            skLineSegment(sketch, "E339.0", {"start": v(-103.7, 83.6) * mm, "end": v(-103.71, 85.35) * mm});
            skLineSegment(sketch, "E340.trimOffspring", {"start": v(-103.73, 89.44) * mm, "end": v(-103.74, 91.2) * mm});
            skPoint(sketch, "E341.orphan", {"position": v(-103.42, 87.4) * mm});
            skLineSegment(sketch, "E342.trimOffspring", {"start": v(-103.17, 89.45) * mm, "end": v(-103.17, 91.2) * mm});
            skPoint(sketch, "E343.MirrorCS.end.orphan", {"position": v(-100.7, 87.42) * mm});
            skPoint(sketch, "E343.MirrorCS.start.orphan", {"position": v(-100.72, 87.72) * mm});
            skPoint(sketch, "E344.MirrorCS.end.orphan", {"position": v(-99.3, 87.98) * mm});
            skPoint(sketch, "E344.MirrorCS.start.orphan", {"position": v(-99.3, 88.3) * mm});
            skPoint(sketch, "E345.orphan", {"position": v(-107.55, 87.38) * mm});
            skPoint(sketch, "E346.MirrorCS.end.orphan", {"position": v(-106.1, 87.67) * mm});
            skArc(sketch, "E347.trimOffspring", {"start": v(-103.14, 83.6) * mm, "mid": v(-102.81, 83.62) * mm, "end": v(-102.5, 83.65) * mm});
            skArc(sketch, "E348.trimOffspring", {"start": v(-103.15, 85.35) * mm, "mid": v(-102.7, 85.4) * mm, "end": v(-102.25, 85.5) * mm});
            skArc(sketch, "E349.trimOffspring", {"start": v(-103.17, 89.45) * mm, "mid": v(-102.71, 89.4) * mm, "end": v(-102.26, 89.3) * mm});
            skArc(sketch, "E350.trimOffspring", {"start": v(-103.17, 91.2) * mm, "mid": v(-102.85, 91.18) * mm, "end": v(-102.53, 91.15) * mm});
            skText(sketch, "E351", { "text": "X", "fontName": "OpenSans-Bold.ttf"});
            skLineSegment(sketch, "E352", {"start": v(-94.23, 89.98) * mm, "end": v(-96.1, 89.98) * mm});
            skLineSegment(sketch, "E353", {"start": v(-96.1, 89.98) * mm, "end": v(-94.23, 89.98) * mm});
            skCircle(sketch, "E354", {"center": v(-103.42, 87.4) * mm, "radius": 0.97 * mm});
            skArc(sketch, "E355.0", {"start": v(-94.23, 89.98) * mm, "mid": v(-96.46, 83.51) * mm, "end": v(-94, 77.12) * mm});
            skLineSegment(sketch, "E356", {"start": v(-95.93, 77.12) * mm, "end": v(-94, 77.12) * mm});
            skLineSegment(sketch, "E357.MirrorCS", {"start": v(-73.58, -40.38) * mm, "end": v(-73.58, -42.18) * mm});
            skArc(sketch, "E358.MirrorCS", {"start": v(-73.58, -40.38) * mm, "mid": v(-78.57, -37.95) * mm, "end": v(-75.83, -33.12) * mm});
            skArc(sketch, "E359.MirrorCS", {"start": v(-75.83, -33.12) * mm, "mid": v(-70.45, -33.14) * mm, "end": v(-66, -36.14) * mm});
            skArc(sketch, "E360.MirrorCS", {"start": v(-66, -36.14) * mm, "mid": v(-65.16, -37.55) * mm, "end": v(-64.54, -39.05) * mm});
            skArc(sketch, "E361.MirrorCS", {"start": v(-60.38, -42.18) * mm, "mid": v(-62.98, -41.3) * mm, "end": v(-64.54, -39.05) * mm});
            skPoint(sketch, "E362.visualSharp", {"position": v(-47.84, 29.85) * mm});
            skLineSegment(sketch, "E363.0", {"start": v(-84.67, -12.92) * mm, "end": v(-77.45, -11.65) * mm});
            skLineSegment(sketch, "E363.1", {"start": v(-77.45, -11.65) * mm, "end": v(-72.74, -17.27) * mm});
            skLineSegment(sketch, "E363.2", {"start": v(-72.74, -17.27) * mm, "end": v(-75.25, -24.16) * mm});
            skLineSegment(sketch, "E363.3", {"start": v(-75.25, -24.16) * mm, "end": v(-77.05, -24.48) * mm});
            skLineSegment(sketch, "E363.4", {"start": v(-86, -21.22) * mm, "end": v(-87.18, -19.81) * mm});
            skLineSegment(sketch, "E363.5", {"start": v(-87.18, -19.81) * mm, "end": v(-84.67, -12.92) * mm});
            skPoint(sketch, "E363.0.midPoint", {"position": v(-81.06, -12.29) * mm});
            skLineSegment(sketch, "E364.2", {"start": v(-77.05, -24.48) * mm, "end": v(-78.93, -29.64) * mm});
            skLineSegment(sketch, "E364.3", {"start": v(-78.93, -29.64) * mm, "end": v(-79.84, -29.8) * mm});
            skLineSegment(sketch, "E364.4", {"start": v(-87.3, -27.09) * mm, "end": v(-87.88, -26.39) * mm});
            skLineSegment(sketch, "E364.5", {"start": v(-87.88, -26.39) * mm, "end": v(-86, -21.22) * mm});
            skPoint(sketch, "E365.visualSharp", {"position": v(-89.88, -42.8) * mm});
            skLineSegment(sketch, "E366.2", {"start": v(-79.84, -29.8) * mm, "end": v(-81.4, -34.1) * mm});
            skLineSegment(sketch, "E366.3", {"start": v(-81.4, -34.1) * mm, "end": v(-82.3, -34.27) * mm});
            skLineSegment(sketch, "E366.4", {"start": v(-88.27, -32.1) * mm, "end": v(-88.86, -31.4) * mm});
            skLineSegment(sketch, "E366.5", {"start": v(-88.86, -31.4) * mm, "end": v(-87.3, -27.09) * mm});
            skLineSegment(sketch, "E367.2", {"start": v(-82.3, -34.27) * mm, "end": v(-83.56, -37.71) * mm});
            skLineSegment(sketch, "E367.3", {"start": v(-83.56, -37.71) * mm, "end": v(-87.17, -38.35) * mm});
            skLineSegment(sketch, "E367.4", {"start": v(-87.17, -38.35) * mm, "end": v(-89.53, -35.54) * mm});
            skLineSegment(sketch, "E367.5", {"start": v(-89.53, -35.54) * mm, "end": v(-88.27, -32.1) * mm});
            skLineSegment(sketch, "E368.bottom", {"start": v(-84.82, 43.42) * mm, "end": v(-43.54, 43.42) * mm});
            skLineSegment(sketch, "E368.left", {"start": v(-91.17, 35.54) * mm, "end": v(-91.17, 34) * mm});
            skLineSegment(sketch, "E368.right", {"start": v(-37.2, 35.54) * mm, "end": v(-37.2, 34) * mm});
            skArc(sketch, "E369.filletArc", {"start": v(-84.82, 43.42) * mm, "mid": v(-89.3, 41.56) * mm, "end": v(-91.17, 37.07) * mm});
            skArc(sketch, "E370.filletArc", {"start": v(-37.2, 37.07) * mm, "mid": v(-39.05, 41.56) * mm, "end": v(-43.54, 43.42) * mm});
            skPoint(sketch, "E371.visualSharp", {"position": v(-37.2, -42.18) * mm});
            skArc(sketch, "E371.filletArc", {"start": v(-43.54, -42.18) * mm, "mid": v(-39.3, -40.55) * mm, "end": v(-37.23, -36.5) * mm});
            skArc(sketch, "E372.filletArc", {"start": v(-91.17, -35.83) * mm, "mid": v(-89.3, -40.32) * mm, "end": v(-84.82, -42.18) * mm});
            skLineSegment(sketch, "E373", {"start": v(-88, 37.07) * mm, "end": v(-88, 38.66) * mm});
            skLineSegment(sketch, "E374", {"start": v(-88, 38.66) * mm, "end": v(-80.07, 38.66) * mm});
            skLineSegment(sketch, "E375", {"start": v(-68.94, 38.66) * mm, "end": v(-68.94, 37.07) * mm});
            skLineSegment(sketch, "E376.MirrorCS", {"start": v(-59.42, 38.66) * mm, "end": v(-59.42, 37.07) * mm});
            skLineSegment(sketch, "E377.MirrorCS", {"start": v(-40.37, 38.66) * mm, "end": v(-48.29, 38.66) * mm});
            skLineSegment(sketch, "E378.MirrorCS", {"start": v(-40.37, 37.07) * mm, "end": v(-40.37, 38.66) * mm});
            skLineSegment(sketch, "E379", {"start": v(-91.17, -21.14) * mm, "end": v(-91.17, -13.2) * mm});
            skLineSegment(sketch, "E380", {"start": v(-91.17, -21.14) * mm, "end": v(-91.17, -26.2) * mm});
            skLineSegment(sketch, "E381", {"start": v(-91.17, -29.08) * mm, "end": v(-91.17, -21.14) * mm});
            skPoint(sketch, "E382.orphan", {"position": v(-59.42, 37.07) * mm});
            skPoint(sketch, "E383.MirrorCS.end.orphan", {"position": v(-40.37, 37.07) * mm});
            skLineSegment(sketch, "E384", {"start": v(-59.42, 37.07) * mm, "end": v(-55.9, 37.07) * mm});
            skPoint(sketch, "E385.center.orphan", {"position": v(-64.18, -42.18) * mm});
            skLineSegment(sketch, "E386", {"start": v(-88, 37.07) * mm, "end": v(-79.86, 37.07) * mm});
            skLineSegment(sketch, "E387.trimOffspring", {"start": v(-60.38, -42.18) * mm, "end": v(-43.54, -42.18) * mm});
            skLineSegment(sketch, "E388.MirrorCS", {"start": v(-49.11, 26.22) * mm, "end": v(-49.11, 26.21) * mm});
            skLineSegment(sketch, "E389.MirrorCS", {"start": v(-50.64, 26.22) * mm, "end": v(-50.64, 26.22) * mm});
            skLineSegment(sketch, "E390.MirrorCS", {"start": v(-50.32, 33.89) * mm, "end": v(-49.43, 33.89) * mm});
            skLineSegment(sketch, "E391.MirrorCS", {"start": v(-77.71, 26.22) * mm, "end": v(-77.71, 26.22) * mm});
            skLineSegment(sketch, "E392.MirrorCS", {"start": v(-79.24, 26.22) * mm, "end": v(-79.24, 26.21) * mm});
            skLineSegment(sketch, "E393.MirrorCS", {"start": v(-78.04, 33.89) * mm, "end": v(-78.92, 33.89) * mm});
            skLineSegment(sketch, "E394", {"start": v(-77.72, 22.45) * mm, "end": v(-77.71, 22.45) * mm});
            skLineSegment(sketch, "E395", {"start": v(-37.2, 7) * mm, "end": v(-37.2, 7.94) * mm});
            skLineSegment(sketch, "E396", {"start": v(-61.33, -34.3) * mm, "end": v(-37.95, -34.3) * mm});
            skArc(sketch, "E397", {"start": v(-37.95, -34.3) * mm, "mid": v(-37.2, -33.54) * mm, "end": v(-37.95, -32.77) * mm});
            skLineSegment(sketch, "E398", {"start": v(-37.95, -32.77) * mm, "end": v(-62.6, -32.77) * mm});
            skArc(sketch, "E399", {"start": v(-37.23, -36.5) * mm, "mid": v(-37.46, -36.03) * mm, "end": v(-37.96, -35.83) * mm});
            skPoint(sketch, "E400.start.orphan", {"position": v(-37.2, -35.83) * mm});
            skArc(sketch, "E401", {"start": v(-61.33, -34.3) * mm, "mid": v(-62.1, -35.07) * mm, "end": v(-61.33, -35.83) * mm});
            skLineSegment(sketch, "E402", {"start": v(-61.33, -35.83) * mm, "end": v(-37.96, -35.83) * mm});
            skArc(sketch, "E403", {"start": v(-62.6, -31.24) * mm, "mid": v(-63.35, -32) * mm, "end": v(-62.6, -32.77) * mm});
            skLineSegment(sketch, "E404", {"start": v(-62.6, -31.24) * mm, "end": v(-37.95, -31.24) * mm});
            skArc(sketch, "E405", {"start": v(-37.95, -31.24) * mm, "mid": v(-37.2, -30.47) * mm, "end": v(-37.95, -29.7) * mm});
            skLineSegment(sketch, "E406", {"start": v(-37.95, -29.7) * mm, "end": v(-62.6, -29.7) * mm});
            skLineSegment(sketch, "E407", {"start": v(-62.6, -28.17) * mm, "end": v(-37.95, -28.17) * mm});
            skArc(sketch, "E408", {"start": v(-37.95, -28.17) * mm, "mid": v(-37.2, -27.4) * mm, "end": v(-37.95, -26.64) * mm});
            skLineSegment(sketch, "E409", {"start": v(-37.95, -26.64) * mm, "end": v(-62.6, -26.64) * mm});
            skArc(sketch, "E410", {"start": v(-62.6, -25.1) * mm, "mid": v(-63.35, -25.87) * mm, "end": v(-62.6, -26.64) * mm});
            skLineSegment(sketch, "E411", {"start": v(-62.6, -25.1) * mm, "end": v(-37.95, -25.1) * mm});
            skArc(sketch, "E412", {"start": v(-37.95, -25.1) * mm, "mid": v(-37.2, -24.34) * mm, "end": v(-37.95, -23.57) * mm});
            skLineSegment(sketch, "E413", {"start": v(-37.95, -23.57) * mm, "end": v(-62.6, -23.57) * mm});
            skLineSegment(sketch, "E414", {"start": v(-62.6, -22.04) * mm, "end": v(-37.95, -22.04) * mm});
            skArc(sketch, "E415", {"start": v(-37.95, -22.04) * mm, "mid": v(-37.2, -21.27) * mm, "end": v(-37.95, -20.5) * mm});
            skLineSegment(sketch, "E416", {"start": v(-37.95, -20.5) * mm, "end": v(-62.6, -20.5) * mm});
            skArc(sketch, "E417", {"start": v(-62.6, -22.04) * mm, "mid": v(-63.35, -22.8) * mm, "end": v(-62.6, -23.57) * mm});
            skArc(sketch, "E418", {"start": v(-62.6, -18.97) * mm, "mid": v(-63.35, -19.74) * mm, "end": v(-62.6, -20.5) * mm});
            skLineSegment(sketch, "E419", {"start": v(-62.6, -18.97) * mm, "end": v(-37.95, -18.97) * mm});
            skArc(sketch, "E420", {"start": v(-37.95, -18.97) * mm, "mid": v(-37.2, -18.2) * mm, "end": v(-37.95, -17.44) * mm});
            skLineSegment(sketch, "E421", {"start": v(-37.95, -17.44) * mm, "end": v(-62.6, -17.44) * mm});
            skArc(sketch, "E422", {"start": v(-62.6, -15.9) * mm, "mid": v(-63.35, -16.67) * mm, "end": v(-62.6, -17.44) * mm});
            skLineSegment(sketch, "E423", {"start": v(-62.6, -15.9) * mm, "end": v(-37.95, -15.9) * mm});
            skArc(sketch, "E424", {"start": v(-37.95, -15.9) * mm, "mid": v(-37.2, -15.14) * mm, "end": v(-37.95, -14.37) * mm});
            skLineSegment(sketch, "E425", {"start": v(-37.95, -14.37) * mm, "end": v(-62.6, -14.37) * mm});
            skArc(sketch, "E426", {"start": v(-62.6, -12.84) * mm, "mid": v(-63.35, -13.6) * mm, "end": v(-62.6, -14.37) * mm});
            skLineSegment(sketch, "E427", {"start": v(-62.6, -12.84) * mm, "end": v(-37.95, -12.84) * mm});
            skArc(sketch, "E428", {"start": v(-37.95, -12.84) * mm, "mid": v(-37.2, -12.08) * mm, "end": v(-37.95, -11.3) * mm});
            skLineSegment(sketch, "E429", {"start": v(-37.95, -11.3) * mm, "end": v(-62.6, -11.3) * mm});
            skArc(sketch, "E430", {"start": v(-62.6, -9.78) * mm, "mid": v(-63.35, -10.54) * mm, "end": v(-62.6, -11.3) * mm});
            skLineSegment(sketch, "E431", {"start": v(-62.6, -9.78) * mm, "end": v(-37.95, -9.78) * mm});
            skArc(sketch, "E432", {"start": v(-37.95, -9.78) * mm, "mid": v(-37.2, -9) * mm, "end": v(-37.95, -8.24) * mm});
            skLineSegment(sketch, "E433", {"start": v(-37.95, -8.24) * mm, "end": v(-62.6, -8.24) * mm});
            skArc(sketch, "E434", {"start": v(-62.6, -6.71) * mm, "mid": v(-63.35, -7.48) * mm, "end": v(-62.6, -8.24) * mm});
            skLineSegment(sketch, "E435", {"start": v(-62.6, -6.71) * mm, "end": v(-37.95, -6.71) * mm});
            skArc(sketch, "E436", {"start": v(-37.95, -6.71) * mm, "mid": v(-37.2, -5.94) * mm, "end": v(-37.95, -5.18) * mm});
            skLineSegment(sketch, "E437", {"start": v(-37.95, -5.18) * mm, "end": v(-62.6, -5.18) * mm});
            skArc(sketch, "E438", {"start": v(-62.6, -3.64) * mm, "mid": v(-63.35, -4.41) * mm, "end": v(-62.6, -5.18) * mm});
            skLineSegment(sketch, "E439", {"start": v(-62.6, -3.64) * mm, "end": v(-37.95, -3.64) * mm});
            skArc(sketch, "E440", {"start": v(-37.95, -3.64) * mm, "mid": v(-37.2, -2.88) * mm, "end": v(-37.95, -2.11) * mm});
            skLineSegment(sketch, "E441", {"start": v(-37.95, -2.11) * mm, "end": v(-62.6, -2.11) * mm});
            skArc(sketch, "E442", {"start": v(-62.6, -0.58) * mm, "mid": v(-63.35, -1.35) * mm, "end": v(-62.6, -2.11) * mm});
            skLineSegment(sketch, "E443", {"start": v(-62.6, -0.58) * mm, "end": v(-37.95, -0.58) * mm});
            skArc(sketch, "E444", {"start": v(-37.95, -0.58) * mm, "mid": v(-37.2, 0.19) * mm, "end": v(-37.95, 0.95) * mm});
            skLineSegment(sketch, "E445", {"start": v(-37.95, 0.95) * mm, "end": v(-62.6, 0.95) * mm});
            skArc(sketch, "E446", {"start": v(-62.6, 2.49) * mm, "mid": v(-63.35, 1.72) * mm, "end": v(-62.6, 0.95) * mm});
            skLineSegment(sketch, "E447", {"start": v(-62.6, 2.49) * mm, "end": v(-37.95, 2.49) * mm});
            skArc(sketch, "E448", {"start": v(-37.95, 2.49) * mm, "mid": v(-37.2, 3.25) * mm, "end": v(-37.95, 4.02) * mm});
            skLineSegment(sketch, "E449", {"start": v(-37.95, 4.02) * mm, "end": v(-62.6, 4.02) * mm});
            skArc(sketch, "E450", {"start": v(-62.6, 5.55) * mm, "mid": v(-63.35, 4.79) * mm, "end": v(-62.6, 4.02) * mm});
            skLineSegment(sketch, "E451", {"start": v(-62.6, 5.55) * mm, "end": v(-37.95, 5.55) * mm});
            skArc(sketch, "E452", {"start": v(-37.95, 5.55) * mm, "mid": v(-37.41, 5.78) * mm, "end": v(-37.2, 6.32) * mm});
            skLineSegment(sketch, "E453", {"start": v(-37.2, 6.32) * mm, "end": v(-37.2, 7) * mm});
            skLineSegment(sketch, "E454.0", {"start": v(-78.92, 33.89) * mm, "end": v(-78.92, 23.07) * mm});
            skLineSegment(sketch, "E455.0", {"start": v(-78.04, 33.89) * mm, "end": v(-78.04, 23.07) * mm});
            skLineSegment(sketch, "E456.0", {"start": v(-50.32, 33.89) * mm, "end": v(-50.32, 23.07) * mm});
            skLineSegment(sketch, "E457.0", {"start": v(-49.43, 33.89) * mm, "end": v(-49.43, 23.07) * mm});
            skArc(sketch, "E458", {"start": v(-50.88, 22.44) * mm, "mid": v(-49.85, 9.7) * mm, "end": v(-48.9, 22.45) * mm});
            skArc(sketch, "E459", {"start": v(-79.48, 22.44) * mm, "mid": v(-78.46, 9.69) * mm, "end": v(-77.5, 22.45) * mm});
            skArc(sketch, "E460", {"start": v(-91.17, 7.94) * mm, "mid": v(-90.4, 8.71) * mm, "end": v(-91.17, 9.48) * mm});
            skArc(sketch, "E461", {"start": v(-91.17, 11.01) * mm, "mid": v(-90.4, 11.78) * mm, "end": v(-91.17, 12.54) * mm});
            skArc(sketch, "E462", {"start": v(-91.17, 14.08) * mm, "mid": v(-90.4, 14.84) * mm, "end": v(-91.17, 15.6) * mm});
            skArc(sketch, "E463", {"start": v(-91.17, 17.14) * mm, "mid": v(-90.4, 17.9) * mm, "end": v(-91.17, 18.67) * mm});
            skArc(sketch, "E464", {"start": v(-91.17, 20.2) * mm, "mid": v(-90.4, 20.97) * mm, "end": v(-91.17, 21.74) * mm});
            skArc(sketch, "E465", {"start": v(-91.17, 23.27) * mm, "mid": v(-90.4, 24.04) * mm, "end": v(-91.17, 24.8) * mm});
            skArc(sketch, "E466", {"start": v(-91.17, 26.34) * mm, "mid": v(-90.4, 27.1) * mm, "end": v(-91.17, 27.87) * mm});
            skArc(sketch, "E467", {"start": v(-91.17, 29.4) * mm, "mid": v(-90.4, 30.17) * mm, "end": v(-91.17, 30.94) * mm});
            skArc(sketch, "E468", {"start": v(-91.17, 32.47) * mm, "mid": v(-90.4, 33.24) * mm, "end": v(-91.17, 34) * mm});
            skArc(sketch, "E469", {"start": v(-91.17, 35.54) * mm, "mid": v(-90.4, 36.3) * mm, "end": v(-91.17, 37.07) * mm});
            skArc(sketch, "E470", {"start": v(-37.2, 9.48) * mm, "mid": v(-37.95, 8.71) * mm, "end": v(-37.2, 7.94) * mm});
            skArc(sketch, "E471", {"start": v(-37.2, 12.54) * mm, "mid": v(-37.95, 11.78) * mm, "end": v(-37.2, 11.01) * mm});
            skArc(sketch, "E472", {"start": v(-37.2, 15.6) * mm, "mid": v(-37.95, 14.84) * mm, "end": v(-37.2, 14.08) * mm});
            skArc(sketch, "E473", {"start": v(-37.2, 18.67) * mm, "mid": v(-37.95, 17.9) * mm, "end": v(-37.2, 17.14) * mm});
            skArc(sketch, "E474", {"start": v(-37.2, 21.74) * mm, "mid": v(-37.95, 20.97) * mm, "end": v(-37.2, 20.2) * mm});
            skArc(sketch, "E475", {"start": v(-37.2, 24.8) * mm, "mid": v(-37.95, 24.04) * mm, "end": v(-37.2, 23.27) * mm});
            skArc(sketch, "E476", {"start": v(-37.2, 27.87) * mm, "mid": v(-37.95, 27.1) * mm, "end": v(-37.2, 26.34) * mm});
            skArc(sketch, "E477", {"start": v(-37.2, 30.94) * mm, "mid": v(-37.95, 30.17) * mm, "end": v(-37.2, 29.4) * mm});
            skArc(sketch, "E478", {"start": v(-37.2, 34) * mm, "mid": v(-37.95, 33.24) * mm, "end": v(-37.2, 32.47) * mm});
            skArc(sketch, "E479", {"start": v(-37.2, 37.07) * mm, "mid": v(-37.95, 36.3) * mm, "end": v(-37.2, 35.54) * mm});
            skLineSegment(sketch, "E480.trimOffspring", {"start": v(-91.17, 7.94) * mm, "end": v(-91.17, -35.83) * mm});
            skLineSegment(sketch, "E481.trimOffspring", {"start": v(-91.17, 11.01) * mm, "end": v(-91.17, 9.48) * mm});
            skLineSegment(sketch, "E482.trimOffspring", {"start": v(-91.17, 14.08) * mm, "end": v(-91.17, 12.54) * mm});
            skLineSegment(sketch, "E483.trimOffspring", {"start": v(-91.17, 17.14) * mm, "end": v(-91.17, 15.6) * mm});
            skLineSegment(sketch, "E484.trimOffspring", {"start": v(-91.17, 20.2) * mm, "end": v(-91.17, 18.67) * mm});
            skLineSegment(sketch, "E485.trimOffspring", {"start": v(-91.17, 23.27) * mm, "end": v(-91.17, 21.74) * mm});
            skLineSegment(sketch, "E486.trimOffspring", {"start": v(-91.17, 26.34) * mm, "end": v(-91.17, 24.8) * mm});
            skLineSegment(sketch, "E487.trimOffspring", {"start": v(-91.17, 29.4) * mm, "end": v(-91.17, 27.87) * mm});
            skLineSegment(sketch, "E488.trimOffspring", {"start": v(-91.17, 32.47) * mm, "end": v(-91.17, 30.94) * mm});
            skLineSegment(sketch, "E489.trimOffspring", {"start": v(-37.2, 32.47) * mm, "end": v(-37.2, 30.94) * mm});
            skLineSegment(sketch, "E490.trimOffspring", {"start": v(-37.2, 29.4) * mm, "end": v(-37.2, 27.87) * mm});
            skLineSegment(sketch, "E491.trimOffspring", {"start": v(-37.2, 26.34) * mm, "end": v(-37.2, 24.8) * mm});
            skLineSegment(sketch, "E492.trimOffspring", {"start": v(-37.2, 23.27) * mm, "end": v(-37.2, 21.74) * mm});
            skLineSegment(sketch, "E493.trimOffspring", {"start": v(-37.2, 20.2) * mm, "end": v(-37.2, 18.67) * mm});
            skLineSegment(sketch, "E494.trimOffspring", {"start": v(-37.2, 17.14) * mm, "end": v(-37.2, 15.6) * mm});
            skLineSegment(sketch, "E495.trimOffspring", {"start": v(-37.2, 14.08) * mm, "end": v(-37.2, 12.54) * mm});
            skLineSegment(sketch, "E496.trimOffspring", {"start": v(-37.2, 11.01) * mm, "end": v(-37.2, 9.48) * mm});
            skPoint(sketch, "E497.orphan", {"position": v(-78.48, 33.89) * mm});
            skLineSegment(sketch, "E498.trimOffspring", {"start": v(-76.9, 38.66) * mm, "end": v(-68.94, 38.66) * mm});
            skPoint(sketch, "E499.endSnap0", {"position": v(-49.9, 38.66) * mm});
            skLineSegment(sketch, "E500.trimOffspring", {"start": v(-51.46, 38.66) * mm, "end": v(-59.42, 38.66) * mm});
            skLineSegment(sketch, "E501.trimOffspring", {"start": v(-49.88, 38.66) * mm, "end": v(-49.9, 38.66) * mm});
            skPoint(sketch, "E499.start.orphan", {"position": v(-49.88, 33.89) * mm});
            skLineSegment(sketch, "E502", {"start": v(-51.46, 38.66) * mm, "end": v(-51.28, 38.66) * mm});
            skArc(sketch, "E503", {"start": v(-48.5, 38.66) * mm, "mid": v(-49.89, 39.46) * mm, "end": v(-51.28, 38.66) * mm});
            skLineSegment(sketch, "E504.trimOffspring", {"start": v(-49.9, 38.66) * mm, "end": v(-49.88, 38.66) * mm});
            skLineSegment(sketch, "E505.trimOffspring", {"start": v(-48.5, 38.66) * mm, "end": v(-48.29, 38.66) * mm});
            skPoint(sketch, "E506.end.orphan", {"position": v(-49.89, 37.07) * mm});
            skLineSegment(sketch, "E507.trimOffspring", {"start": v(-48.5, 37.07) * mm, "end": v(-40.37, 37.07) * mm});
            skArc(sketch, "E508.trimOffspring", {"start": v(-51.28, 37.07) * mm, "mid": v(-49.89, 36.26) * mm, "end": v(-48.5, 37.07) * mm});
            skLineSegment(sketch, "E509", {"start": v(-80.07, 38.66) * mm, "end": v(-79.86, 38.66) * mm});
            skPoint(sketch, "E510.orphan", {"position": v(-55.35, 37.07) * mm});
            skPoint(sketch, "E511.start.orphan", {"position": v(-55.35, 33.89) * mm});
            skLineSegment(sketch, "E512.trimOffspring", {"start": v(-54.9, 37.07) * mm, "end": v(-51.28, 37.07) * mm});
            skArc(sketch, "E513.MirrorCS", {"start": v(-79.86, 38.66) * mm, "mid": v(-78.47, 39.46) * mm, "end": v(-77.08, 38.66) * mm});
            skArc(sketch, "E514.MirrorCS", {"start": v(-77.08, 37.07) * mm, "mid": v(-78.47, 36.26) * mm, "end": v(-79.86, 37.07) * mm});
            skPoint(sketch, "E515.start.orphan", {"position": v(-64.18, 43.42) * mm});
            skLineSegment(sketch, "E516.trimOffspring", {"start": v(-77.08, 37.07) * mm, "end": v(-73.45, 37.07) * mm});
            skLineSegment(sketch, "E517.trimOffspring", {"start": v(-77.08, 38.66) * mm, "end": v(-76.9, 38.66) * mm});
            skLineSegment(sketch, "E518.trimOffspring", {"start": v(-72.46, 37.07) * mm, "end": v(-68.94, 37.07) * mm});
            skArc(sketch, "E519", {"start": v(-74.09, 33.66) * mm, "mid": v(-73.13, 35.25) * mm, "end": v(-73.45, 37.07) * mm});
            skArc(sketch, "E520.0", {"start": v(-72.58, 34.14) * mm, "mid": v(-72.2, 35.6) * mm, "end": v(-72.46, 37.07) * mm});
            skArc(sketch, "E521.MirrorCS", {"start": v(-55.78, 34.14) * mm, "mid": v(-56.15, 35.6) * mm, "end": v(-55.9, 37.07) * mm});
            skArc(sketch, "E522.MirrorCS", {"start": v(-54.27, 33.66) * mm, "mid": v(-55.22, 35.25) * mm, "end": v(-54.9, 37.07) * mm});
            skArc(sketch, "E523.MirrorCS", {"start": v(-54.27, 33.66) * mm, "mid": v(-55.6, 28.62) * mm, "end": v(-55.93, 33.82) * mm});
            skPoint(sketch, "E524.orphan", {"position": v(-54.24, 33.64) * mm});
            skPoint(sketch, "E525.start.orphan", {"position": v(-74.09, 33.66) * mm});
            skArc(sketch, "E526.MirrorCS", {"start": v(-74.09, 33.66) * mm, "mid": v(-72.76, 28.62) * mm, "end": v(-72.43, 33.82) * mm});
            skPoint(sketch, "E527.orphan", {"position": v(-74.11, 33.64) * mm});
            skArc(sketch, "E528", {"start": v(-79.48, 22.44) * mm, "mid": v(-79.1, 22.66) * mm, "end": v(-78.92, 23.07) * mm});
            skArc(sketch, "E529.MirrorCS", {"start": v(-77.48, 22.44) * mm, "mid": v(-77.86, 22.66) * mm, "end": v(-78.04, 23.07) * mm});
            skArc(sketch, "E530.MirrorCS", {"start": v(-48.87, 22.44) * mm, "mid": v(-49.26, 22.66) * mm, "end": v(-49.43, 23.07) * mm});
            skArc(sketch, "E531.MirrorCS", {"start": v(-50.88, 22.44) * mm, "mid": v(-50.5, 22.66) * mm, "end": v(-50.32, 23.07) * mm});
            skArc(sketch, "E532", {"start": v(-72.58, 34.14) * mm, "mid": v(-72.57, 33.95) * mm, "end": v(-72.43, 33.82) * mm});
            skArc(sketch, "E533.MirrorCS", {"start": v(-55.78, 34.14) * mm, "mid": v(-55.78, 33.95) * mm, "end": v(-55.93, 33.82) * mm});
            skArc(sketch, "E534", {"start": v(-62.6, -28.17) * mm, "mid": v(-63.35, -28.94) * mm, "end": v(-62.6, -29.7) * mm});
            skPoint(sketch, "E535", {"position": v(-50.27, -5.18) * mm});
            skPoint(sketch, "E536", {"position": v(-91.17, -17.17) * mm});
            skArc(sketch, "E537", {"start": v(-76.1, 3.4) * mm, "mid": v(-76.47, 2.56) * mm, "end": v(-76.65, 1.65) * mm});
            skArc(sketch, "E538", {"start": v(-76.5, 0.19) * mm, "mid": v(-75.96, -0.84) * mm, "end": v(-74.9, -1.34) * mm});
            skArc(sketch, "E539", {"start": v(-74.9, 5.48) * mm, "mid": v(-75.43, 5.42) * mm, "end": v(-75.95, 5.3) * mm});
            skArc(sketch, "E540", {"start": v(-75.95, 5.3) * mm, "mid": v(-76.59, 5.05) * mm, "end": v(-77.16, 4.66) * mm});
            skArc(sketch, "E541", {"start": v(-77.16, 4.66) * mm, "mid": v(-77.7, 4.08) * mm, "end": v(-78.07, 3.37) * mm});
            skArc(sketch, "E542", {"start": v(-78.07, 3.37) * mm, "mid": v(-78.31, 2.53) * mm, "end": v(-78.4, 1.65) * mm});
            skArc(sketch, "E543", {"start": v(-78.4, 1.65) * mm, "mid": v(-78.4, 1.65) * mm, "end": v(-78.4, 1.65) * mm});
            skArc(sketch, "E544", {"start": v(-78.35, 0.43) * mm, "mid": v(-78.24, -0.14) * mm, "end": v(-78.06, -0.7) * mm});
            skArc(sketch, "E545", {"start": v(-78.06, -0.7) * mm, "mid": v(-77.85, -1.13) * mm, "end": v(-77.57, -1.53) * mm});
            skArc(sketch, "E546", {"start": v(-77.57, -1.53) * mm, "mid": v(-77.19, -1.93) * mm, "end": v(-76.74, -2.25) * mm});
            skArc(sketch, "E547", {"start": v(-76.74, -2.25) * mm, "mid": v(-76.22, -2.5) * mm, "end": v(-75.67, -2.65) * mm});
            skArc(sketch, "E548", {"start": v(-75.67, -2.65) * mm, "mid": v(-75.32, -2.72) * mm, "end": v(-74.96, -2.75) * mm});
            skArc(sketch, "E549", {"start": v(-74.96, -2.75) * mm, "mid": v(-74.93, -2.75) * mm, "end": v(-74.9, -2.75) * mm});
            skLineSegment(sketch, "E550", {"start": v(-74.62, 4.06) * mm, "end": v(-74.62, 4.07) * mm});
            skLineSegment(sketch, "E551", {"start": v(-74.6, -1.35) * mm, "end": v(-74.6, -1.36) * mm});
            skLineSegment(sketch, "E552.trimOffspring", {"start": v(-74.9, 4.04) * mm, "end": v(-74.9, 5.49) * mm});
            skLineSegment(sketch, "E553", {"start": v(-74.9, -2.04) * mm, "end": v(-74.9, -2.75) * mm});
            skArc(sketch, "E554.trimOffspring", {"start": v(-74.6, -2.76) * mm, "mid": v(-74.6, -2.76) * mm, "end": v(-74.58, -2.76) * mm});
            skLineSegment(sketch, "E555.trimOffspring", {"start": v(-74.9, -1.34) * mm, "end": v(-74.9, -2.04) * mm});
            skArc(sketch, "E556.trimOffspring", {"start": v(-74.9, 4.04) * mm, "mid": v(-75.55, 3.82) * mm, "end": v(-76.1, 3.4) * mm});
            skPoint(sketch, "E557.orphan", {"position": v(-76.66, 1.25) * mm});
            skLineSegment(sketch, "E558", {"start": v(-74.62, 4.07) * mm, "end": v(-74.62, 4.06) * mm});
            skArc(sketch, "E559.MirrorCS", {"start": v(-74.33, 4.04) * mm, "mid": v(-73.68, 3.83) * mm, "end": v(-73.13, 3.42) * mm});
            skArc(sketch, "E560.MirrorCS", {"start": v(-73.13, 3.42) * mm, "mid": v(-72.75, 2.58) * mm, "end": v(-72.56, 1.67) * mm});
            skArc(sketch, "E561.MirrorCS", {"start": v(-72.7, 0.2) * mm, "mid": v(-73.23, -0.83) * mm, "end": v(-74.28, -1.34) * mm});
            skArc(sketch, "E562.MirrorCS", {"start": v(-74.2, -2.74) * mm, "mid": v(-74.24, -2.75) * mm, "end": v(-74.27, -2.75) * mm});
            skArc(sketch, "E563.MirrorCS", {"start": v(-73.5, -2.64) * mm, "mid": v(-73.85, -2.7) * mm, "end": v(-74.2, -2.74) * mm});
            skArc(sketch, "E564.MirrorCS", {"start": v(-72.43, -2.23) * mm, "mid": v(-72.95, -2.48) * mm, "end": v(-73.5, -2.64) * mm});
            skArc(sketch, "E565.MirrorCS", {"start": v(-71.6, -1.5) * mm, "mid": v(-71.99, -1.9) * mm, "end": v(-72.43, -2.23) * mm});
            skArc(sketch, "E566.MirrorCS", {"start": v(-71.13, -0.66) * mm, "mid": v(-71.34, -1.1) * mm, "end": v(-71.6, -1.5) * mm});
            skArc(sketch, "E567.MirrorCS", {"start": v(-70.85, 0.47) * mm, "mid": v(-70.95, -0.1) * mm, "end": v(-71.13, -0.66) * mm});
            skArc(sketch, "E568.MirrorCS", {"start": v(-70.81, 1.69) * mm, "mid": v(-70.81, 1.68) * mm, "end": v(-70.81, 1.68) * mm});
            skArc(sketch, "E569.MirrorCS", {"start": v(-71.16, 3.4) * mm, "mid": v(-70.9, 2.56) * mm, "end": v(-70.81, 1.69) * mm});
            skArc(sketch, "E570.MirrorCS", {"start": v(-72.08, 4.69) * mm, "mid": v(-71.54, 4.1) * mm, "end": v(-71.16, 3.4) * mm});
            skArc(sketch, "E571.MirrorCS", {"start": v(-73.3, 5.32) * mm, "mid": v(-72.66, 5.07) * mm, "end": v(-72.08, 4.69) * mm});
            skArc(sketch, "E572.MirrorCS", {"start": v(-74.34, 5.48) * mm, "mid": v(-73.82, 5.43) * mm, "end": v(-73.3, 5.32) * mm});
            skLineSegment(sketch, "E573.MirrorCS", {"start": v(-74.33, 4.04) * mm, "end": v(-74.34, 5.49) * mm});
            skLineSegment(sketch, "E574.MirrorCS", {"start": v(-74.28, -1.34) * mm, "end": v(-74.27, -2.04) * mm});
            skLineSegment(sketch, "E575.MirrorCS", {"start": v(-74.27, -2.04) * mm, "end": v(-74.27, -2.75) * mm});
            skArc(sketch, "E576", {"start": v(-74.6, -1.36) * mm, "mid": v(-74.6, -1.36) * mm, "end": v(-74.6, -1.36) * mm});
            skLineSegment(sketch, "E577.0", {"start": v(-78.4, 1.08) * mm, "end": v(-76.66, 1.09) * mm});
            skLineSegment(sketch, "E578.0", {"start": v(-78.41, 1.65) * mm, "end": v(-76.65, 1.65) * mm});
            skLineSegment(sketch, "E579.trimOffspring", {"start": v(-72.56, 1.67) * mm, "end": v(-70.8, 1.68) * mm});
            skPoint(sketch, "E580.orphan", {"position": v(-74.6, 1.36) * mm});
            skLineSegment(sketch, "E581.trimOffspring", {"start": v(-72.55, 1.1) * mm, "end": v(-70.8, 1.11) * mm});
            skPoint(sketch, "E582.MirrorCS.end.orphan", {"position": v(-74.58, -1.36) * mm});
            skPoint(sketch, "E582.MirrorCS.start.orphan", {"position": v(-74.28, -1.34) * mm});
            skPoint(sketch, "E583.MirrorCS.end.orphan", {"position": v(-74.02, -2.76) * mm});
            skPoint(sketch, "E583.MirrorCS.start.orphan", {"position": v(-73.7, -2.75) * mm});
            skPoint(sketch, "E584.orphan", {"position": v(-74.62, 5.49) * mm});
            skPoint(sketch, "E585.MirrorCS.end.orphan", {"position": v(-74.33, 4.04) * mm});
            skArc(sketch, "E586.trimOffspring", {"start": v(-78.4, 1.08) * mm, "mid": v(-78.38, 0.76) * mm, "end": v(-78.35, 0.43) * mm});
            skArc(sketch, "E587.trimOffspring", {"start": v(-76.66, 1.09) * mm, "mid": v(-76.6, 0.63) * mm, "end": v(-76.5, 0.19) * mm});
            skArc(sketch, "E588.trimOffspring", {"start": v(-72.55, 1.1) * mm, "mid": v(-72.6, 0.65) * mm, "end": v(-72.7, 0.2) * mm});
            skArc(sketch, "E589.trimOffspring", {"start": v(-70.8, 1.11) * mm, "mid": v(-70.82, 0.8) * mm, "end": v(-70.85, 0.47) * mm});
            skText(sketch, "E590", { "text": "X", "fontName": "OpenSans-Bold.ttf"});
            skLineSegment(sketch, "E591", {"start": v(-72.02, -7.83) * mm, "end": v(-72.02, -5.95) * mm});
            skLineSegment(sketch, "E592", {"start": v(-72.02, -5.95) * mm, "end": v(-72.02, -7.83) * mm});
            skCircle(sketch, "E593", {"center": v(-74.6, 1.36) * mm, "radius": 0.97 * mm});
            skArc(sketch, "E594.0", {"start": v(-72.02, -7.83) * mm, "mid": v(-78.5, -5.6) * mm, "end": v(-84.88, -8.06) * mm});
            skLineSegment(sketch, "E595", {"start": v(-84.88, -6.13) * mm, "end": v(-84.88, -8.06) * mm});
            skArc(sketch, "E596", {"start": v(-72.02, -5.95) * mm, "mid": v(-78.48, -4.07) * mm, "end": v(-84.88, -6.13) * mm});
            skLineSegment(sketch, "E597", {"start": v(-84.82, -42.18) * mm, "end": v(-73.58, -42.18) * mm});
            skPoint(sketch, "E598.orphan", {"position": v(-71.4, -42.18) * mm});
            skLineSegment(sketch, "E599.0", {"start": v(96.82, 66.24) * mm, "end": v(100.49, 59.9) * mm});
            skLineSegment(sketch, "E599.4", {"start": v(88.57, 64.66) * mm, "end": v(89.49, 66.24) * mm});
            skLineSegment(sketch, "E599.5", {"start": v(89.49, 66.24) * mm, "end": v(96.82, 66.24) * mm});
            skPoint(sketch, "E599.0.midPoint", {"position": v(98.65, 63.07) * mm});
            skLineSegment(sketch, "E600.4", {"start": v(82.61, 63.86) * mm, "end": v(83.07, 64.66) * mm});
            skLineSegment(sketch, "E600.5", {"start": v(83.07, 64.66) * mm, "end": v(88.57, 64.66) * mm});
            skPoint(sketch, "E601.visualSharp", {"position": v(129.97, 34.2) * mm});
            skLineSegment(sketch, "E602.4", {"start": v(77.57, 63.07) * mm, "end": v(78.03, 63.86) * mm});
            skLineSegment(sketch, "E602.5", {"start": v(78.03, 63.86) * mm, "end": v(82.61, 63.86) * mm});
            skLineSegment(sketch, "E603.4", {"start": v(72.07, 59.9) * mm, "end": v(73.9, 63.07) * mm});
            skLineSegment(sketch, "E603.5", {"start": v(73.9, 63.07) * mm, "end": v(77.57, 63.07) * mm});
            skLineSegment(sketch, "E604.left", {"start": v(51.63, 32.9) * mm, "end": v(53.16, 32.9) * mm});
            skArc(sketch, "E605.filletArc", {"start": v(43.75, 39.26) * mm, "mid": v(45.6, 34.77) * mm, "end": v(50.1, 32.9) * mm});
            skArc(sketch, "E606.filletArc", {"start": v(123.67, 32.94) * mm, "mid": v(125.91, 33.62) * mm, "end": v(127.76, 35.06) * mm});
            skLineSegment(sketch, "E607", {"start": v(50.1, 36.08) * mm, "end": v(48.5, 36.08) * mm});
            skLineSegment(sketch, "E608", {"start": v(48.5, 36.08) * mm, "end": v(48.5, 44) * mm});
            skLineSegment(sketch, "E609", {"start": v(48.5, 55.13) * mm, "end": v(50.1, 55.13) * mm});
            skLineSegment(sketch, "E610", {"start": v(50.1, 36.08) * mm, "end": v(50.1, 44.22) * mm});
            skLineSegment(sketch, "E611.MirrorCS", {"start": v(60.94, 46.36) * mm, "end": v(60.95, 46.36) * mm});
            skLineSegment(sketch, "E612.MirrorCS", {"start": v(60.94, 44.83) * mm, "end": v(60.95, 44.83) * mm});
            skLineSegment(sketch, "E613.MirrorCS", {"start": v(53.28, 46.04) * mm, "end": v(53.28, 45.15) * mm});
            skLineSegment(sketch, "E614", {"start": v(64.71, 46.35) * mm, "end": v(64.71, 46.36) * mm});
            skLineSegment(sketch, "E615.0", {"start": v(53.28, 45.15) * mm, "end": v(64.1, 45.15) * mm});
            skLineSegment(sketch, "E616.0", {"start": v(53.28, 46.04) * mm, "end": v(64.1, 46.04) * mm});
            skArc(sketch, "E617", {"start": v(64.72, 44.6) * mm, "mid": v(77.48, 45.61) * mm, "end": v(64.72, 46.57) * mm});
            skArc(sketch, "E618", {"start": v(79.22, 32.9) * mm, "mid": v(78.46, 33.66) * mm, "end": v(77.69, 32.9) * mm});
            skArc(sketch, "E619", {"start": v(76.16, 32.9) * mm, "mid": v(75.39, 33.66) * mm, "end": v(74.62, 32.9) * mm});
            skArc(sketch, "E620", {"start": v(73.1, 32.9) * mm, "mid": v(72.32, 33.66) * mm, "end": v(71.56, 32.9) * mm});
            skArc(sketch, "E621", {"start": v(70.02, 32.9) * mm, "mid": v(69.26, 33.66) * mm, "end": v(68.5, 32.9) * mm});
            skArc(sketch, "E622", {"start": v(66.96, 32.9) * mm, "mid": v(66.2, 33.66) * mm, "end": v(65.43, 32.9) * mm});
            skArc(sketch, "E623", {"start": v(63.9, 32.9) * mm, "mid": v(63.13, 33.66) * mm, "end": v(62.36, 32.9) * mm});
            skArc(sketch, "E624", {"start": v(60.83, 32.9) * mm, "mid": v(60.06, 33.66) * mm, "end": v(59.3, 32.9) * mm});
            skArc(sketch, "E625", {"start": v(57.76, 32.9) * mm, "mid": v(57, 33.66) * mm, "end": v(56.23, 32.9) * mm});
            skArc(sketch, "E626", {"start": v(54.7, 32.9) * mm, "mid": v(53.93, 33.66) * mm, "end": v(53.16, 32.9) * mm});
            skArc(sketch, "E627", {"start": v(51.63, 32.9) * mm, "mid": v(50.86, 33.66) * mm, "end": v(50.1, 32.9) * mm});
            skLineSegment(sketch, "E628.trimOffspring", {"start": v(76.16, 32.9) * mm, "end": v(77.69, 32.9) * mm});
            skLineSegment(sketch, "E629.trimOffspring", {"start": v(73.1, 32.9) * mm, "end": v(74.62, 32.9) * mm});
            skLineSegment(sketch, "E630.trimOffspring", {"start": v(70.02, 32.9) * mm, "end": v(71.56, 32.9) * mm});
            skLineSegment(sketch, "E631.trimOffspring", {"start": v(66.96, 32.9) * mm, "end": v(68.5, 32.9) * mm});
            skLineSegment(sketch, "E632.trimOffspring", {"start": v(63.9, 32.9) * mm, "end": v(65.43, 32.9) * mm});
            skLineSegment(sketch, "E633.trimOffspring", {"start": v(60.83, 32.9) * mm, "end": v(62.36, 32.9) * mm});
            skLineSegment(sketch, "E634.trimOffspring", {"start": v(57.76, 32.9) * mm, "end": v(59.3, 32.9) * mm});
            skLineSegment(sketch, "E635.trimOffspring", {"start": v(54.7, 32.9) * mm, "end": v(56.23, 32.9) * mm});
            skPoint(sketch, "E636.orphan", {"position": v(53.28, 45.6) * mm});
            skLineSegment(sketch, "E637.trimOffspring", {"start": v(48.5, 47.18) * mm, "end": v(48.5, 55.13) * mm});
            skLineSegment(sketch, "E638", {"start": v(48.5, 44) * mm, "end": v(48.5, 44.22) * mm});
            skArc(sketch, "E639.MirrorCS", {"start": v(48.5, 44.22) * mm, "mid": v(47.7, 45.6) * mm, "end": v(48.5, 47) * mm});
            skArc(sketch, "E640.MirrorCS", {"start": v(50.1, 47) * mm, "mid": v(50.9, 45.6) * mm, "end": v(50.1, 44.22) * mm});
            skLineSegment(sketch, "E641.trimOffspring", {"start": v(50.1, 47) * mm, "end": v(50.1, 50.62) * mm});
            skLineSegment(sketch, "E642.trimOffspring", {"start": v(48.5, 47) * mm, "end": v(48.5, 47.18) * mm});
            skLineSegment(sketch, "E643.trimOffspring", {"start": v(50.1, 51.6) * mm, "end": v(50.1, 55.13) * mm});
            skArc(sketch, "E644", {"start": v(53.5, 49.99) * mm, "mid": v(51.92, 50.94) * mm, "end": v(50.1, 50.62) * mm});
            skArc(sketch, "E645.0", {"start": v(53.02, 51.5) * mm, "mid": v(51.57, 51.87) * mm, "end": v(50.1, 51.6) * mm});
            skPoint(sketch, "E646.start.orphan", {"position": v(53.5, 49.99) * mm});
            skArc(sketch, "E647.MirrorCS", {"start": v(53.5, 49.99) * mm, "mid": v(58.55, 51.31) * mm, "end": v(53.34, 51.65) * mm});
            skPoint(sketch, "E648.orphan", {"position": v(53.53, 49.96) * mm});
            skArc(sketch, "E649", {"start": v(64.72, 44.6) * mm, "mid": v(64.5, 44.98) * mm, "end": v(64.1, 45.15) * mm});
            skArc(sketch, "E650.MirrorCS", {"start": v(64.72, 46.6) * mm, "mid": v(64.5, 46.2) * mm, "end": v(64.1, 46.04) * mm});
            skArc(sketch, "E651", {"start": v(53.02, 51.5) * mm, "mid": v(53.22, 51.5) * mm, "end": v(53.34, 51.65) * mm});
            skLineSegment(sketch, "E652", {"start": v(128.59, 59.13) * mm, "end": v(103.95, 59.13) * mm});
            skArc(sketch, "E653", {"start": v(103.95, 59.13) * mm, "mid": v(103.19, 58.36) * mm, "end": v(103.95, 57.6) * mm});
            skLineSegment(sketch, "E654", {"start": v(103.95, 57.6) * mm, "end": v(128.59, 57.6) * mm});
            skArc(sketch, "E655", {"start": v(128.59, 56.06) * mm, "mid": v(129.35, 56.83) * mm, "end": v(128.59, 57.6) * mm});
            skLineSegment(sketch, "E656", {"start": v(128.59, 56.06) * mm, "end": v(103.95, 56.06) * mm});
            skArc(sketch, "E657", {"start": v(103.95, 56.06) * mm, "mid": v(103.19, 55.3) * mm, "end": v(103.95, 54.53) * mm});
            skLineSegment(sketch, "E658", {"start": v(103.95, 54.53) * mm, "end": v(128.59, 54.53) * mm});
            skLineSegment(sketch, "E659", {"start": v(128.59, 53) * mm, "end": v(103.95, 53) * mm});
            skArc(sketch, "E660", {"start": v(103.95, 53) * mm, "mid": v(103.19, 52.23) * mm, "end": v(103.95, 51.46) * mm});
            skLineSegment(sketch, "E661", {"start": v(103.95, 51.46) * mm, "end": v(128.59, 51.46) * mm});
            skArc(sketch, "E662", {"start": v(128.59, 53) * mm, "mid": v(129.35, 53.76) * mm, "end": v(128.59, 54.53) * mm});
            skArc(sketch, "E663", {"start": v(128.59, 49.93) * mm, "mid": v(129.35, 50.7) * mm, "end": v(128.59, 51.46) * mm});
            skLineSegment(sketch, "E664", {"start": v(128.59, 49.93) * mm, "end": v(103.95, 49.93) * mm});
            skArc(sketch, "E665", {"start": v(103.95, 49.93) * mm, "mid": v(103.19, 49.16) * mm, "end": v(103.95, 48.4) * mm});
            skLineSegment(sketch, "E666", {"start": v(103.95, 48.4) * mm, "end": v(128.59, 48.4) * mm});
            skArc(sketch, "E667", {"start": v(128.59, 46.87) * mm, "mid": v(129.35, 47.63) * mm, "end": v(128.59, 48.4) * mm});
            skLineSegment(sketch, "E668", {"start": v(128.59, 46.87) * mm, "end": v(103.95, 46.87) * mm});
            skArc(sketch, "E669", {"start": v(103.95, 46.87) * mm, "mid": v(103.19, 46.1) * mm, "end": v(103.95, 45.33) * mm});
            skLineSegment(sketch, "E670", {"start": v(103.95, 45.33) * mm, "end": v(128.59, 45.33) * mm});
            skArc(sketch, "E671", {"start": v(128.59, 43.8) * mm, "mid": v(129.35, 44.57) * mm, "end": v(128.59, 45.33) * mm});
            skLineSegment(sketch, "E672", {"start": v(128.59, 43.8) * mm, "end": v(103.95, 43.8) * mm});
            skArc(sketch, "E673", {"start": v(103.95, 43.8) * mm, "mid": v(103.19, 43.03) * mm, "end": v(103.95, 42.27) * mm});
            skLineSegment(sketch, "E674", {"start": v(103.95, 42.27) * mm, "end": v(128.59, 42.27) * mm});
            skArc(sketch, "E675", {"start": v(128.59, 40.73) * mm, "mid": v(129.35, 41.5) * mm, "end": v(128.59, 42.27) * mm});
            skLineSegment(sketch, "E676", {"start": v(128.59, 40.73) * mm, "end": v(103.95, 40.73) * mm});
            skArc(sketch, "E677", {"start": v(103.95, 40.73) * mm, "mid": v(103.19, 39.97) * mm, "end": v(103.95, 39.2) * mm});
            skLineSegment(sketch, "E678", {"start": v(103.95, 39.2) * mm, "end": v(128.54, 39.2) * mm});
            skArc(sketch, "E679", {"start": v(128.54, 37.67) * mm, "mid": v(129.3, 38.43) * mm, "end": v(128.54, 39.2) * mm});
            skLineSegment(sketch, "E680", {"start": v(128.54, 37.67) * mm, "end": v(103.95, 37.67) * mm});
            skArc(sketch, "E681", {"start": v(103.95, 37.67) * mm, "mid": v(103.19, 36.9) * mm, "end": v(103.95, 36.14) * mm});
            skLineSegment(sketch, "E682", {"start": v(103.95, 36.14) * mm, "end": v(127.26, 36.14) * mm});
            skArc(sketch, "E683", {"start": v(127.8, 35.9) * mm, "mid": v(127.55, 36.07) * mm, "end": v(127.26, 36.14) * mm});
            skArc(sketch, "E684", {"start": v(128.59, 59.13) * mm, "mid": v(129.35, 59.9) * mm, "end": v(128.59, 60.66) * mm});
            skArc(sketch, "E685", {"start": v(103.95, 62.2) * mm, "mid": v(103.19, 61.43) * mm, "end": v(103.95, 60.66) * mm});
            skLineSegment(sketch, "E686.trimOffspring", {"start": v(128.53, 36.14) * mm, "end": v(128.59, 36.14) * mm});
            skArc(sketch, "E687", {"start": v(127.76, 35.06) * mm, "mid": v(127.91, 35.48) * mm, "end": v(127.8, 35.9) * mm});
            skArc(sketch, "E688.MirrorCS", {"start": v(80.55, 32.92) * mm, "mid": v(83.15, 33.79) * mm, "end": v(84.7, 36.05) * mm});
            skArc(sketch, "E689.MirrorCS", {"start": v(86.16, 38.96) * mm, "mid": v(85.33, 37.55) * mm, "end": v(84.7, 36.05) * mm});
            skArc(sketch, "E690.MirrorCS", {"start": v(96, 41.98) * mm, "mid": v(90.62, 41.96) * mm, "end": v(86.16, 38.96) * mm});
            skArc(sketch, "E691.MirrorCS", {"start": v(93.75, 34.72) * mm, "mid": v(98.74, 37.15) * mm, "end": v(96, 41.98) * mm});
            skLineSegment(sketch, "E692.MirrorCS", {"start": v(93.75, 34.72) * mm, "end": v(93.75, 32.92) * mm});
            skLineSegment(sketch, "E693.MirrorCS", {"start": v(93.75, 32.92) * mm, "end": v(123.67, 32.94) * mm});
            skLineSegment(sketch, "E694", {"start": v(80.55, 32.92) * mm, "end": v(79.22, 32.9) * mm});
            skArc(sketch, "E695.MirrorCS", {"start": v(43.75, 80.53) * mm, "mid": v(45.6, 85.02) * mm, "end": v(50.1, 86.88) * mm});
            skLineSegment(sketch, "E696.MirrorCS", {"start": v(48.5, 83.7) * mm, "end": v(48.5, 75.78) * mm});
            skArc(sketch, "E697.MirrorCS", {"start": v(48.5, 75.57) * mm, "mid": v(47.7, 74.18) * mm, "end": v(48.5, 72.8) * mm});
            skLineSegment(sketch, "E698.MirrorCS", {"start": v(48.5, 72.6) * mm, "end": v(48.5, 64.66) * mm});
            skLineSegment(sketch, "E699.MirrorCS", {"start": v(48.5, 64.66) * mm, "end": v(50.1, 64.66) * mm});
            skLineSegment(sketch, "E700.MirrorCS", {"start": v(50.1, 68.18) * mm, "end": v(50.1, 64.66) * mm});
            skArc(sketch, "E701.MirrorCS", {"start": v(53.02, 68.3) * mm, "mid": v(51.57, 67.92) * mm, "end": v(50.1, 68.18) * mm});
            skLineSegment(sketch, "E702.MirrorCS", {"start": v(53.28, 73.75) * mm, "end": v(64.1, 73.75) * mm});
            skLineSegment(sketch, "E703.MirrorCS", {"start": v(53.28, 74.64) * mm, "end": v(64.1, 74.64) * mm});
            skLineSegment(sketch, "E704.MirrorCS", {"start": v(53.28, 73.75) * mm, "end": v(53.28, 74.64) * mm});
            skLineSegment(sketch, "E705.MirrorCS", {"start": v(50.1, 72.8) * mm, "end": v(50.1, 69.17) * mm});
            skArc(sketch, "E706.MirrorCS", {"start": v(50.1, 72.8) * mm, "mid": v(50.9, 74.18) * mm, "end": v(50.1, 75.57) * mm});
            skLineSegment(sketch, "E707.MirrorCS", {"start": v(50.1, 83.7) * mm, "end": v(50.1, 75.57) * mm});
            skLineSegment(sketch, "E708.MirrorCS", {"start": v(50.1, 83.7) * mm, "end": v(48.5, 83.7) * mm});
            skArc(sketch, "E709.MirrorCS", {"start": v(53.5, 69.8) * mm, "mid": v(51.92, 68.85) * mm, "end": v(50.1, 69.17) * mm});
            skArc(sketch, "E710.MirrorCS", {"start": v(53.5, 69.8) * mm, "mid": v(58.55, 68.47) * mm, "end": v(53.34, 68.14) * mm});
            skArc(sketch, "E711.MirrorCS", {"start": v(53.02, 68.3) * mm, "mid": v(53.22, 68.3) * mm, "end": v(53.34, 68.14) * mm});
            skLineSegment(sketch, "E712.MirrorCS", {"start": v(80.55, 86.87) * mm, "end": v(79.22, 86.88) * mm});
            skArc(sketch, "E713.MirrorCS", {"start": v(54.7, 86.88) * mm, "mid": v(53.93, 86.13) * mm, "end": v(53.16, 86.88) * mm});
            skLineSegment(sketch, "E714.MirrorCS", {"start": v(54.7, 86.88) * mm, "end": v(56.23, 86.88) * mm});
            skArc(sketch, "E715.MirrorCS", {"start": v(79.22, 86.88) * mm, "mid": v(78.46, 86.13) * mm, "end": v(77.69, 86.88) * mm});
            skArc(sketch, "E716.MirrorCS", {"start": v(60.83, 86.88) * mm, "mid": v(60.06, 86.13) * mm, "end": v(59.3, 86.88) * mm});
            skLineSegment(sketch, "E717.MirrorCS", {"start": v(51.63, 86.88) * mm, "end": v(53.16, 86.88) * mm});
            skLineSegment(sketch, "E718.MirrorCS", {"start": v(73.1, 86.88) * mm, "end": v(74.62, 86.88) * mm});
            skLineSegment(sketch, "E719.MirrorCS", {"start": v(63.9, 86.88) * mm, "end": v(65.43, 86.88) * mm});
            skLineSegment(sketch, "E720.MirrorCS", {"start": v(66.96, 86.88) * mm, "end": v(68.5, 86.88) * mm});
            skLineSegment(sketch, "E721.MirrorCS", {"start": v(70.02, 86.88) * mm, "end": v(71.56, 86.88) * mm});
            skArc(sketch, "E722.MirrorCS", {"start": v(57.76, 86.88) * mm, "mid": v(57, 86.13) * mm, "end": v(56.23, 86.88) * mm});
            skArc(sketch, "E723.MirrorCS", {"start": v(66.96, 86.88) * mm, "mid": v(66.2, 86.13) * mm, "end": v(65.43, 86.88) * mm});
            skLineSegment(sketch, "E724.MirrorCS", {"start": v(57.76, 86.88) * mm, "end": v(59.3, 86.88) * mm});
            skArc(sketch, "E725.MirrorCS", {"start": v(63.9, 86.88) * mm, "mid": v(63.13, 86.13) * mm, "end": v(62.36, 86.88) * mm});
            skArc(sketch, "E726.MirrorCS", {"start": v(51.63, 86.88) * mm, "mid": v(50.86, 86.13) * mm, "end": v(50.1, 86.88) * mm});
            skLineSegment(sketch, "E727.MirrorCS", {"start": v(76.16, 86.88) * mm, "end": v(77.69, 86.88) * mm});
            skLineSegment(sketch, "E728.MirrorCS", {"start": v(60.83, 86.88) * mm, "end": v(62.36, 86.88) * mm});
            skArc(sketch, "E729.MirrorCS", {"start": v(73.1, 86.88) * mm, "mid": v(72.32, 86.13) * mm, "end": v(71.56, 86.88) * mm});
            skArc(sketch, "E730.MirrorCS", {"start": v(76.16, 86.88) * mm, "mid": v(75.39, 86.13) * mm, "end": v(74.62, 86.88) * mm});
            skArc(sketch, "E731.MirrorCS", {"start": v(70.02, 86.88) * mm, "mid": v(69.26, 86.13) * mm, "end": v(68.5, 86.88) * mm});
            skArc(sketch, "E732.MirrorCS", {"start": v(128.59, 72.92) * mm, "mid": v(129.35, 72.16) * mm, "end": v(128.59, 71.4) * mm});
            skArc(sketch, "E733.MirrorCS", {"start": v(128.59, 79.06) * mm, "mid": v(129.35, 78.29) * mm, "end": v(128.59, 77.52) * mm});
            skArc(sketch, "E734.MirrorCS", {"start": v(128.59, 69.86) * mm, "mid": v(129.35, 69.1) * mm, "end": v(128.59, 68.33) * mm});
            skArc(sketch, "E735.MirrorCS", {"start": v(103.95, 63.73) * mm, "mid": v(103.19, 64.5) * mm, "end": v(103.95, 65.26) * mm});
            skArc(sketch, "E736.MirrorCS", {"start": v(128.59, 66.8) * mm, "mid": v(129.35, 66.03) * mm, "end": v(128.59, 65.26) * mm});
            skArc(sketch, "E737.MirrorCS", {"start": v(103.95, 66.8) * mm, "mid": v(103.19, 67.56) * mm, "end": v(103.95, 68.33) * mm});
            skLineSegment(sketch, "E738.MirrorCS", {"start": v(64.71, 73.44) * mm, "end": v(64.71, 73.43) * mm});
            skArc(sketch, "E739.MirrorCS", {"start": v(128.59, 60.66) * mm, "mid": v(129.35, 59.9) * mm, "end": v(128.59, 59.13) * mm});
            skArc(sketch, "E740.MirrorCS", {"start": v(103.95, 60.66) * mm, "mid": v(103.19, 61.43) * mm, "end": v(103.95, 62.2) * mm});
            skArc(sketch, "E741.MirrorCS", {"start": v(103.95, 75.99) * mm, "mid": v(103.19, 76.76) * mm, "end": v(103.95, 77.52) * mm});
            skArc(sketch, "E742.MirrorCS", {"start": v(103.95, 72.92) * mm, "mid": v(103.19, 73.7) * mm, "end": v(103.95, 74.46) * mm});
            skArc(sketch, "E743.MirrorCS", {"start": v(64.72, 73.2) * mm, "mid": v(64.5, 73.58) * mm, "end": v(64.1, 73.75) * mm});
            skArc(sketch, "E744.MirrorCS", {"start": v(64.72, 75.2) * mm, "mid": v(64.5, 74.81) * mm, "end": v(64.1, 74.64) * mm});
            skLineSegment(sketch, "E745.MirrorCS", {"start": v(128.53, 83.65) * mm, "end": v(128.59, 83.65) * mm});
            skArc(sketch, "E746.MirrorCS", {"start": v(128.54, 82.12) * mm, "mid": v(129.3, 81.35) * mm, "end": v(128.54, 80.59) * mm});
            skLineSegment(sketch, "E747.MirrorCS", {"start": v(48.5, 72.8) * mm, "end": v(48.5, 72.6) * mm});
            skArc(sketch, "E748.MirrorCS", {"start": v(103.95, 69.86) * mm, "mid": v(103.19, 70.62) * mm, "end": v(103.95, 71.4) * mm});
            skArc(sketch, "E749.MirrorCS", {"start": v(128.59, 63.73) * mm, "mid": v(129.35, 62.96) * mm, "end": v(128.59, 62.2) * mm});
            skLineSegment(sketch, "E750.MirrorCS", {"start": v(48.5, 75.78) * mm, "end": v(48.5, 75.57) * mm});
            skArc(sketch, "E751.MirrorCS", {"start": v(128.59, 75.99) * mm, "mid": v(129.35, 75.22) * mm, "end": v(128.59, 74.46) * mm});
            skArc(sketch, "E752.MirrorCS", {"start": v(127.76, 84.73) * mm, "mid": v(127.91, 84.3) * mm, "end": v(127.8, 83.88) * mm});
            skLineSegment(sketch, "E753.MirrorCS", {"start": v(93.75, 85.07) * mm, "end": v(93.75, 86.87) * mm});
            skArc(sketch, "E754.MirrorCS", {"start": v(103.95, 79.06) * mm, "mid": v(103.19, 79.82) * mm, "end": v(103.95, 80.59) * mm});
            skArc(sketch, "E755.MirrorCS", {"start": v(123.67, 86.85) * mm, "mid": v(125.91, 86.17) * mm, "end": v(127.76, 84.73) * mm});
            skLineSegment(sketch, "E756.MirrorCS", {"start": v(77.57, 56.72) * mm, "end": v(78.03, 55.93) * mm});
            skArc(sketch, "E757.MirrorCS", {"start": v(127.8, 83.88) * mm, "mid": v(127.55, 83.72) * mm, "end": v(127.26, 83.65) * mm});
            skLineSegment(sketch, "E758.MirrorCS", {"start": v(78.03, 55.93) * mm, "end": v(82.61, 55.93) * mm});
            skLineSegment(sketch, "E759.MirrorCS", {"start": v(73.9, 56.72) * mm, "end": v(77.57, 56.72) * mm});
            skArc(sketch, "E760.MirrorCS", {"start": v(103.95, 82.12) * mm, "mid": v(103.19, 82.89) * mm, "end": v(103.95, 83.65) * mm});
            skLineSegment(sketch, "E761.MirrorCS", {"start": v(82.61, 55.93) * mm, "end": v(83.07, 55.13) * mm});
            skLineSegment(sketch, "E762.MirrorCS", {"start": v(60.94, 73.43) * mm, "end": v(60.95, 73.43) * mm});
            skLineSegment(sketch, "E763.MirrorCS", {"start": v(60.94, 74.96) * mm, "end": v(60.95, 74.96) * mm});
            skArc(sketch, "E764.MirrorCS", {"start": v(86.16, 80.83) * mm, "mid": v(85.33, 82.24) * mm, "end": v(84.7, 83.74) * mm});
            skLineSegment(sketch, "E765.MirrorCS", {"start": v(88.57, 55.13) * mm, "end": v(89.49, 53.54) * mm});
            skLineSegment(sketch, "E766.MirrorCS", {"start": v(72.07, 59.9) * mm, "end": v(73.9, 56.72) * mm});
            skLineSegment(sketch, "E767.MirrorCS", {"start": v(96.82, 53.54) * mm, "end": v(100.49, 59.9) * mm});
            skLineSegment(sketch, "E768.MirrorCS", {"start": v(103.95, 77.52) * mm, "end": v(128.59, 77.52) * mm});
            skLineSegment(sketch, "E769.MirrorCS", {"start": v(89.49, 53.54) * mm, "end": v(96.82, 53.54) * mm});
            skLineSegment(sketch, "E770.MirrorCS", {"start": v(103.95, 71.4) * mm, "end": v(128.59, 71.4) * mm});
            skLineSegment(sketch, "E771.MirrorCS", {"start": v(128.54, 82.12) * mm, "end": v(103.95, 82.12) * mm});
            skLineSegment(sketch, "E772.MirrorCS", {"start": v(93.75, 86.87) * mm, "end": v(123.67, 86.85) * mm});
            skArc(sketch, "E773.MirrorCS", {"start": v(96, 77.81) * mm, "mid": v(90.62, 77.83) * mm, "end": v(86.16, 80.83) * mm});
            skLineSegment(sketch, "E774.MirrorCS", {"start": v(103.95, 83.65) * mm, "end": v(127.26, 83.65) * mm});
            skPoint(sketch, "E775.MirrorP", {"position": v(53.28, 74.2) * mm});
            skArc(sketch, "E776.MirrorCS", {"start": v(93.75, 85.07) * mm, "mid": v(98.74, 82.64) * mm, "end": v(96, 77.81) * mm});
            skLineSegment(sketch, "E777.MirrorCS", {"start": v(128.59, 60.66) * mm, "end": v(103.95, 60.66) * mm});
            skPoint(sketch, "E778.MirrorP", {"position": v(98.65, 56.72) * mm});
            skLineSegment(sketch, "E779.MirrorCS", {"start": v(103.95, 80.59) * mm, "end": v(128.54, 80.59) * mm});
            skLineSegment(sketch, "E780.MirrorCS", {"start": v(128.59, 75.99) * mm, "end": v(103.95, 75.99) * mm});
            skPoint(sketch, "E781.MirrorP", {"position": v(123, 86.88) * mm});
            skPoint(sketch, "E782.MirrorP", {"position": v(53.5, 69.8) * mm});
            skLineSegment(sketch, "E783.MirrorCS", {"start": v(128.59, 63.73) * mm, "end": v(103.95, 63.73) * mm});
            skLineSegment(sketch, "E784.MirrorCS", {"start": v(103.95, 74.46) * mm, "end": v(128.59, 74.46) * mm});
            skArc(sketch, "E785.MirrorCS", {"start": v(64.72, 75.2) * mm, "mid": v(77.48, 74.18) * mm, "end": v(64.72, 73.22) * mm});
            skPoint(sketch, "E786.MirrorP", {"position": v(53.53, 69.83) * mm});
            skArc(sketch, "E787.MirrorCS", {"start": v(80.55, 86.87) * mm, "mid": v(83.15, 86) * mm, "end": v(84.7, 83.74) * mm});
            skLineSegment(sketch, "E788.MirrorCS", {"start": v(103.95, 65.26) * mm, "end": v(128.59, 65.26) * mm});
            skLineSegment(sketch, "E789.MirrorCS", {"start": v(83.07, 55.13) * mm, "end": v(88.57, 55.13) * mm});
            skLineSegment(sketch, "E790.MirrorCS", {"start": v(128.59, 72.92) * mm, "end": v(103.95, 72.92) * mm});
            skPoint(sketch, "E791.MirrorP", {"position": v(129.97, 85.6) * mm});
            skLineSegment(sketch, "E792.MirrorCS", {"start": v(128.59, 79.06) * mm, "end": v(103.95, 79.06) * mm});
            skLineSegment(sketch, "E793.MirrorCS", {"start": v(128.59, 69.86) * mm, "end": v(103.95, 69.86) * mm});
            skLineSegment(sketch, "E794.MirrorCS", {"start": v(103.95, 68.33) * mm, "end": v(128.59, 68.33) * mm});
            skLineSegment(sketch, "E795.MirrorCS", {"start": v(103.95, 62.2) * mm, "end": v(128.59, 62.2) * mm});
            skLineSegment(sketch, "E796.MirrorCS", {"start": v(128.59, 66.8) * mm, "end": v(103.95, 66.8) * mm});
            skLineSegment(sketch, "E797", {"start": v(43.75, 39.26) * mm, "end": v(43.75, 80.53) * mm});
            skArc(sketch, "E798", {"start": v(67.7, 64.2) * mm, "mid": v(66.45, 59.9) * mm, "end": v(67.83, 55.63) * mm});
            skArc(sketch, "E799", {"start": v(61.47, 61.48) * mm, "mid": v(62.03, 61.23) * mm, "end": v(62.64, 61.12) * mm});
            skArc(sketch, "E800", {"start": v(63.61, 61.21) * mm, "mid": v(64.3, 61.58) * mm, "end": v(64.63, 62.28) * mm});
            skArc(sketch, "E801", {"start": v(60.09, 62.28) * mm, "mid": v(60.12, 61.93) * mm, "end": v(60.2, 61.58) * mm});
            skArc(sketch, "E802", {"start": v(60.2, 61.58) * mm, "mid": v(60.37, 61.16) * mm, "end": v(60.63, 60.77) * mm});
            skArc(sketch, "E803", {"start": v(60.63, 60.77) * mm, "mid": v(61.02, 60.42) * mm, "end": v(61.5, 60.17) * mm});
            skArc(sketch, "E804", {"start": v(61.5, 60.17) * mm, "mid": v(62.05, 60) * mm, "end": v(62.64, 59.95) * mm});
            skArc(sketch, "E805", {"start": v(62.64, 59.95) * mm, "mid": v(62.64, 59.95) * mm, "end": v(62.64, 59.95) * mm});
            skArc(sketch, "E806", {"start": v(63.45, 59.98) * mm, "mid": v(63.83, 60.06) * mm, "end": v(64.2, 60.18) * mm});
            skArc(sketch, "E807", {"start": v(64.2, 60.18) * mm, "mid": v(64.5, 60.32) * mm, "end": v(64.76, 60.5) * mm});
            skArc(sketch, "E808", {"start": v(64.76, 60.5) * mm, "mid": v(65.02, 60.76) * mm, "end": v(65.24, 61.05) * mm});
            skArc(sketch, "E809", {"start": v(65.24, 61.05) * mm, "mid": v(65.4, 61.4) * mm, "end": v(65.5, 61.77) * mm});
            skArc(sketch, "E810", {"start": v(65.5, 61.77) * mm, "mid": v(65.55, 62) * mm, "end": v(65.57, 62.24) * mm});
            skArc(sketch, "E811", {"start": v(65.57, 62.24) * mm, "mid": v(65.57, 62.26) * mm, "end": v(65.57, 62.28) * mm});
            skLineSegment(sketch, "E812", {"start": v(61.03, 62.47) * mm, "end": v(61.03, 62.47) * mm});
            skLineSegment(sketch, "E813", {"start": v(64.64, 62.48) * mm, "end": v(64.65, 62.48) * mm});
            skLineSegment(sketch, "E814.trimOffspring", {"start": v(61.05, 62.28) * mm, "end": v(60.08, 62.28) * mm});
            skLineSegment(sketch, "E815", {"start": v(65.1, 62.28) * mm, "end": v(65.57, 62.28) * mm});
            skArc(sketch, "E816.trimOffspring", {"start": v(65.58, 62.48) * mm, "mid": v(65.58, 62.49) * mm, "end": v(65.58, 62.5) * mm});
            skLineSegment(sketch, "E817.trimOffspring", {"start": v(64.63, 62.28) * mm, "end": v(65.1, 62.28) * mm});
            skArc(sketch, "E818.trimOffspring", {"start": v(61.05, 62.28) * mm, "mid": v(61.2, 61.85) * mm, "end": v(61.47, 61.48) * mm});
            skPoint(sketch, "E819.orphan", {"position": v(62.9, 61.1) * mm});
            skArc(sketch, "E820.MirrorCS", {"start": v(61.04, 62.66) * mm, "mid": v(61.19, 63.1) * mm, "end": v(61.46, 63.46) * mm});
            skArc(sketch, "E821.MirrorCS", {"start": v(61.46, 63.46) * mm, "mid": v(62.02, 63.72) * mm, "end": v(62.62, 63.84) * mm});
            skArc(sketch, "E822.MirrorCS", {"start": v(63.6, 63.75) * mm, "mid": v(64.3, 63.4) * mm, "end": v(64.63, 62.7) * mm});
            skArc(sketch, "E823.MirrorCS", {"start": v(65.57, 62.74) * mm, "mid": v(65.57, 62.72) * mm, "end": v(65.57, 62.7) * mm});
            skArc(sketch, "E824.MirrorCS", {"start": v(65.5, 63.22) * mm, "mid": v(65.54, 62.98) * mm, "end": v(65.57, 62.74) * mm});
            skArc(sketch, "E825.MirrorCS", {"start": v(65.23, 63.93) * mm, "mid": v(65.4, 63.58) * mm, "end": v(65.5, 63.22) * mm});
            skArc(sketch, "E826.MirrorCS", {"start": v(64.74, 64.48) * mm, "mid": v(65, 64.22) * mm, "end": v(65.23, 63.93) * mm});
            skArc(sketch, "E827.MirrorCS", {"start": v(64.18, 64.8) * mm, "mid": v(64.47, 64.66) * mm, "end": v(64.74, 64.48) * mm});
            skArc(sketch, "E828.MirrorCS", {"start": v(63.43, 64.98) * mm, "mid": v(63.8, 64.91) * mm, "end": v(64.18, 64.8) * mm});
            skArc(sketch, "E829.MirrorCS", {"start": v(62.61, 65) * mm, "mid": v(62.62, 65) * mm, "end": v(62.62, 65) * mm});
            skArc(sketch, "E830.MirrorCS", {"start": v(61.47, 64.78) * mm, "mid": v(62.03, 64.94) * mm, "end": v(62.61, 65) * mm});
            skArc(sketch, "E831.MirrorCS", {"start": v(60.61, 64.16) * mm, "mid": v(61, 64.52) * mm, "end": v(61.47, 64.78) * mm});
            skArc(sketch, "E832.MirrorCS", {"start": v(60.2, 63.35) * mm, "mid": v(60.36, 63.78) * mm, "end": v(60.61, 64.16) * mm});
            skArc(sketch, "E833.MirrorCS", {"start": v(60.08, 62.66) * mm, "mid": v(60.12, 63) * mm, "end": v(60.2, 63.35) * mm});
            skLineSegment(sketch, "E834.MirrorCS", {"start": v(61.04, 62.66) * mm, "end": v(60.08, 62.66) * mm});
            skLineSegment(sketch, "E835.MirrorCS", {"start": v(64.63, 62.7) * mm, "end": v(65.1, 62.7) * mm});
            skLineSegment(sketch, "E836.MirrorCS", {"start": v(65.1, 62.7) * mm, "end": v(65.57, 62.7) * mm});
            skArc(sketch, "E837", {"start": v(64.65, 62.48) * mm, "mid": v(64.65, 62.49) * mm, "end": v(64.65, 62.49) * mm});
            skLineSegment(sketch, "E838.0", {"start": v(63.02, 59.94) * mm, "end": v(63.01, 61.11) * mm});
            skLineSegment(sketch, "E839.0", {"start": v(62.64, 59.94) * mm, "end": v(62.64, 61.12) * mm});
            skLineSegment(sketch, "E840.trimOffspring", {"start": v(62.62, 63.84) * mm, "end": v(62.62, 65.01) * mm});
            skPoint(sketch, "E841.orphan", {"position": v(62.83, 62.48) * mm});
            skLineSegment(sketch, "E842.trimOffspring", {"start": v(63, 63.85) * mm, "end": v(63, 65.02) * mm});
            skPoint(sketch, "E843.MirrorCS.end.orphan", {"position": v(64.65, 62.5) * mm});
            skPoint(sketch, "E843.MirrorCS.start.orphan", {"position": v(64.63, 62.7) * mm});
            skPoint(sketch, "E844.MirrorCS.end.orphan", {"position": v(65.58, 62.87) * mm});
            skPoint(sketch, "E844.MirrorCS.start.orphan", {"position": v(65.57, 63.08) * mm});
            skPoint(sketch, "E845.orphan", {"position": v(60.08, 62.47) * mm});
            skPoint(sketch, "E846.MirrorCS.end.orphan", {"position": v(61.04, 62.66) * mm});
            skArc(sketch, "E847.trimOffspring", {"start": v(63.02, 59.95) * mm, "mid": v(63.23, 59.96) * mm, "end": v(63.45, 59.98) * mm});
            skArc(sketch, "E848.trimOffspring", {"start": v(63.01, 61.11) * mm, "mid": v(63.32, 61.15) * mm, "end": v(63.61, 61.21) * mm});
            skArc(sketch, "E849.trimOffspring", {"start": v(63, 63.85) * mm, "mid": v(63.3, 63.82) * mm, "end": v(63.6, 63.75) * mm});
            skArc(sketch, "E850.trimOffspring", {"start": v(63, 65.01) * mm, "mid": v(63.21, 65) * mm, "end": v(63.43, 64.98) * mm});
            skText(sketch, "E851", { "text": "X", "fontName": "OpenSans-Bold.ttf"});
            skLineSegment(sketch, "E852", {"start": v(68.96, 64.2) * mm, "end": v(67.7, 64.2) * mm});
            skLineSegment(sketch, "E853", {"start": v(67.7, 64.2) * mm, "end": v(68.96, 64.2) * mm});
            skCircle(sketch, "E854", {"center": v(62.83, 62.48) * mm, "radius": 0.65 * mm});
            skArc(sketch, "E855.0", {"start": v(68.96, 64.2) * mm, "mid": v(67.47, 59.89) * mm, "end": v(69.11, 55.63) * mm});
            skLineSegment(sketch, "E856", {"start": v(67.83, 55.63) * mm, "end": v(69.11, 55.63) * mm});
            skLineSegment(sketch, "E857.0", {"start": v(75.74, -11.43) * mm, "end": v(72.07, -5.08) * mm});
            skLineSegment(sketch, "E857.4", {"start": v(83.99, -9.84) * mm, "end": v(83.07, -11.43) * mm});
            skLineSegment(sketch, "E857.5", {"start": v(83.07, -11.43) * mm, "end": v(75.74, -11.43) * mm});
            skPoint(sketch, "E857.0.midPoint", {"position": v(73.9, -8.25) * mm});
            skLineSegment(sketch, "E858.4", {"start": v(89.95, -9.05) * mm, "end": v(89.49, -9.84) * mm});
            skLineSegment(sketch, "E858.5", {"start": v(89.49, -9.84) * mm, "end": v(83.99, -9.84) * mm});
            skPoint(sketch, "E859.visualSharp", {"position": v(129.97, -30.77) * mm});
            skLineSegment(sketch, "E860.4", {"start": v(94.99, -8.25) * mm, "end": v(94.53, -9.05) * mm});
            skLineSegment(sketch, "E860.5", {"start": v(94.53, -9.05) * mm, "end": v(89.95, -9.05) * mm});
            skLineSegment(sketch, "E861.4", {"start": v(100.49, -5.08) * mm, "end": v(98.65, -8.25) * mm});
            skLineSegment(sketch, "E861.5", {"start": v(98.65, -8.25) * mm, "end": v(94.99, -8.25) * mm});
            skLineSegment(sketch, "E862.left", {"start": v(51.63, -32.06) * mm, "end": v(53.16, -32.06) * mm});
            skArc(sketch, "E863.filletArc", {"start": v(43.75, -25.71) * mm, "mid": v(45.6, -30.2) * mm, "end": v(50.1, -32.06) * mm});
            skArc(sketch, "E864.filletArc", {"start": v(123.67, -32.03) * mm, "mid": v(125.91, -31.35) * mm, "end": v(127.76, -29.9) * mm});
            skLineSegment(sketch, "E865", {"start": v(50.1, -28.89) * mm, "end": v(48.5, -28.89) * mm});
            skLineSegment(sketch, "E866", {"start": v(48.5, -28.89) * mm, "end": v(48.5, -20.97) * mm});
            skLineSegment(sketch, "E867", {"start": v(48.5, -9.84) * mm, "end": v(50.1, -9.84) * mm});
            skLineSegment(sketch, "E868", {"start": v(50.1, -28.89) * mm, "end": v(50.1, -20.76) * mm});
            skLineSegment(sketch, "E869.MirrorCS", {"start": v(60.94, -18.61) * mm, "end": v(60.95, -18.61) * mm});
            skLineSegment(sketch, "E870.MirrorCS", {"start": v(60.94, -20.14) * mm, "end": v(60.95, -20.14) * mm});
            skLineSegment(sketch, "E871.MirrorCS", {"start": v(53.28, -18.93) * mm, "end": v(53.28, -19.82) * mm});
            skLineSegment(sketch, "E872", {"start": v(64.71, -18.62) * mm, "end": v(64.71, -18.61) * mm});
            skLineSegment(sketch, "E873.0", {"start": v(53.28, -19.82) * mm, "end": v(64.1, -19.82) * mm});
            skLineSegment(sketch, "E874.0", {"start": v(53.28, -18.93) * mm, "end": v(64.1, -18.93) * mm});
            skArc(sketch, "E875", {"start": v(64.72, -20.38) * mm, "mid": v(77.48, -19.36) * mm, "end": v(64.72, -18.4) * mm});
            skArc(sketch, "E876", {"start": v(79.22, -32.06) * mm, "mid": v(78.46, -31.3) * mm, "end": v(77.69, -32.06) * mm});
            skArc(sketch, "E877", {"start": v(76.16, -32.06) * mm, "mid": v(75.39, -31.3) * mm, "end": v(74.62, -32.06) * mm});
            skArc(sketch, "E878", {"start": v(73.1, -32.06) * mm, "mid": v(72.32, -31.3) * mm, "end": v(71.56, -32.06) * mm});
            skArc(sketch, "E879", {"start": v(70.02, -32.06) * mm, "mid": v(69.26, -31.3) * mm, "end": v(68.5, -32.06) * mm});
            skArc(sketch, "E880", {"start": v(66.96, -32.06) * mm, "mid": v(66.2, -31.3) * mm, "end": v(65.43, -32.06) * mm});
            skArc(sketch, "E881", {"start": v(63.9, -32.06) * mm, "mid": v(63.13, -31.3) * mm, "end": v(62.36, -32.06) * mm});
            skArc(sketch, "E882", {"start": v(60.83, -32.06) * mm, "mid": v(60.06, -31.3) * mm, "end": v(59.3, -32.06) * mm});
            skArc(sketch, "E883", {"start": v(57.76, -32.06) * mm, "mid": v(57, -31.3) * mm, "end": v(56.23, -32.06) * mm});
            skArc(sketch, "E884", {"start": v(54.7, -32.06) * mm, "mid": v(53.93, -31.3) * mm, "end": v(53.16, -32.06) * mm});
            skArc(sketch, "E885", {"start": v(51.63, -32.06) * mm, "mid": v(50.86, -31.3) * mm, "end": v(50.1, -32.06) * mm});
            skLineSegment(sketch, "E886.trimOffspring", {"start": v(76.16, -32.06) * mm, "end": v(77.69, -32.06) * mm});
            skLineSegment(sketch, "E887.trimOffspring", {"start": v(73.1, -32.06) * mm, "end": v(74.62, -32.06) * mm});
            skLineSegment(sketch, "E888.trimOffspring", {"start": v(70.02, -32.06) * mm, "end": v(71.56, -32.06) * mm});
            skLineSegment(sketch, "E889.trimOffspring", {"start": v(66.96, -32.06) * mm, "end": v(68.5, -32.06) * mm});
            skLineSegment(sketch, "E890.trimOffspring", {"start": v(63.9, -32.06) * mm, "end": v(65.43, -32.06) * mm});
            skLineSegment(sketch, "E891.trimOffspring", {"start": v(60.83, -32.06) * mm, "end": v(62.36, -32.06) * mm});
            skLineSegment(sketch, "E892.trimOffspring", {"start": v(57.76, -32.06) * mm, "end": v(59.3, -32.06) * mm});
            skLineSegment(sketch, "E893.trimOffspring", {"start": v(54.7, -32.06) * mm, "end": v(56.23, -32.06) * mm});
            skPoint(sketch, "E894.orphan", {"position": v(53.28, -19.38) * mm});
            skLineSegment(sketch, "E895.trimOffspring", {"start": v(48.5, -17.8) * mm, "end": v(48.5, -9.84) * mm});
            skLineSegment(sketch, "E896", {"start": v(48.5, -20.97) * mm, "end": v(48.5, -20.76) * mm});
            skArc(sketch, "E897.MirrorCS", {"start": v(48.5, -20.76) * mm, "mid": v(47.7, -19.37) * mm, "end": v(48.5, -17.98) * mm});
            skArc(sketch, "E898.MirrorCS", {"start": v(50.1, -17.98) * mm, "mid": v(50.9, -19.37) * mm, "end": v(50.1, -20.76) * mm});
            skLineSegment(sketch, "E899.trimOffspring", {"start": v(50.1, -17.98) * mm, "end": v(50.1, -14.35) * mm});
            skLineSegment(sketch, "E900.trimOffspring", {"start": v(48.5, -17.98) * mm, "end": v(48.5, -17.8) * mm});
            skLineSegment(sketch, "E901.trimOffspring", {"start": v(50.1, -13.36) * mm, "end": v(50.1, -9.84) * mm});
            skArc(sketch, "E902", {"start": v(53.5, -14.98) * mm, "mid": v(51.92, -14.03) * mm, "end": v(50.1, -14.35) * mm});
            skArc(sketch, "E903.0", {"start": v(53.02, -13.47) * mm, "mid": v(51.57, -13.1) * mm, "end": v(50.1, -13.36) * mm});
            skPoint(sketch, "E904.start.orphan", {"position": v(53.5, -14.98) * mm});
            skArc(sketch, "E905.MirrorCS", {"start": v(53.5, -14.98) * mm, "mid": v(58.55, -13.66) * mm, "end": v(53.34, -13.32) * mm});
            skPoint(sketch, "E906.orphan", {"position": v(53.53, -15.01) * mm});
            skArc(sketch, "E907", {"start": v(64.72, -20.38) * mm, "mid": v(64.5, -20) * mm, "end": v(64.1, -19.82) * mm});
            skArc(sketch, "E908.MirrorCS", {"start": v(64.72, -18.38) * mm, "mid": v(64.5, -18.76) * mm, "end": v(64.1, -18.93) * mm});
            skArc(sketch, "E909", {"start": v(53.02, -13.47) * mm, "mid": v(53.22, -13.47) * mm, "end": v(53.34, -13.32) * mm});
            skLineSegment(sketch, "E910", {"start": v(128.59, -5.84) * mm, "end": v(103.95, -5.84) * mm});
            skArc(sketch, "E911", {"start": v(103.95, -5.84) * mm, "mid": v(103.19, -6.6) * mm, "end": v(103.95, -7.38) * mm});
            skLineSegment(sketch, "E912", {"start": v(103.95, -7.38) * mm, "end": v(128.59, -7.38) * mm});
            skArc(sketch, "E913", {"start": v(128.59, -8.9) * mm, "mid": v(129.35, -8.14) * mm, "end": v(128.59, -7.38) * mm});
            skLineSegment(sketch, "E914", {"start": v(128.59, -8.9) * mm, "end": v(103.95, -8.9) * mm});
            skArc(sketch, "E915", {"start": v(103.95, -8.9) * mm, "mid": v(103.19, -9.68) * mm, "end": v(103.95, -10.44) * mm});
            skLineSegment(sketch, "E916", {"start": v(103.95, -10.44) * mm, "end": v(128.59, -10.44) * mm});
            skLineSegment(sketch, "E917", {"start": v(128.59, -11.97) * mm, "end": v(103.95, -11.97) * mm});
            skArc(sketch, "E918", {"start": v(103.95, -11.97) * mm, "mid": v(103.19, -12.74) * mm, "end": v(103.95, -13.5) * mm});
            skLineSegment(sketch, "E919", {"start": v(103.95, -13.5) * mm, "end": v(128.59, -13.5) * mm});
            skArc(sketch, "E920", {"start": v(128.59, -11.97) * mm, "mid": v(129.35, -11.2) * mm, "end": v(128.59, -10.44) * mm});
            skArc(sketch, "E921", {"start": v(128.59, -15.04) * mm, "mid": v(129.35, -14.27) * mm, "end": v(128.59, -13.5) * mm});
            skLineSegment(sketch, "E922", {"start": v(128.59, -15.04) * mm, "end": v(103.95, -15.04) * mm});
            skArc(sketch, "E923", {"start": v(103.95, -15.04) * mm, "mid": v(103.19, -15.8) * mm, "end": v(103.95, -16.57) * mm});
            skLineSegment(sketch, "E924", {"start": v(103.95, -16.57) * mm, "end": v(128.59, -16.57) * mm});
            skArc(sketch, "E925", {"start": v(128.59, -18.1) * mm, "mid": v(129.35, -17.34) * mm, "end": v(128.59, -16.57) * mm});
            skLineSegment(sketch, "E926", {"start": v(128.59, -18.1) * mm, "end": v(103.95, -18.1) * mm});
            skArc(sketch, "E927", {"start": v(103.95, -18.1) * mm, "mid": v(103.19, -18.87) * mm, "end": v(103.95, -19.64) * mm});
            skLineSegment(sketch, "E928", {"start": v(103.95, -19.64) * mm, "end": v(128.59, -19.64) * mm});
            skArc(sketch, "E929", {"start": v(128.59, -21.17) * mm, "mid": v(129.35, -20.4) * mm, "end": v(128.59, -19.64) * mm});
            skLineSegment(sketch, "E930", {"start": v(128.59, -21.17) * mm, "end": v(103.95, -21.17) * mm});
            skArc(sketch, "E931", {"start": v(103.95, -21.17) * mm, "mid": v(103.19, -21.94) * mm, "end": v(103.95, -22.7) * mm});
            skLineSegment(sketch, "E932", {"start": v(103.95, -22.7) * mm, "end": v(128.59, -22.7) * mm});
            skArc(sketch, "E933", {"start": v(128.59, -24.24) * mm, "mid": v(129.35, -23.47) * mm, "end": v(128.59, -22.7) * mm});
            skLineSegment(sketch, "E934", {"start": v(128.59, -24.24) * mm, "end": v(103.95, -24.24) * mm});
            skArc(sketch, "E935", {"start": v(103.95, -24.24) * mm, "mid": v(103.19, -25) * mm, "end": v(103.95, -25.77) * mm});
            skLineSegment(sketch, "E936", {"start": v(103.95, -25.77) * mm, "end": v(128.54, -25.77) * mm});
            skArc(sketch, "E937", {"start": v(128.54, -27.3) * mm, "mid": v(129.3, -26.54) * mm, "end": v(128.54, -25.77) * mm});
            skLineSegment(sketch, "E938", {"start": v(128.54, -27.3) * mm, "end": v(103.95, -27.3) * mm});
            skArc(sketch, "E939", {"start": v(103.95, -27.3) * mm, "mid": v(103.19, -28.07) * mm, "end": v(103.95, -28.84) * mm});
            skLineSegment(sketch, "E940", {"start": v(103.95, -28.84) * mm, "end": v(127.26, -28.84) * mm});
            skArc(sketch, "E941", {"start": v(127.8, -29.06) * mm, "mid": v(127.55, -28.9) * mm, "end": v(127.26, -28.84) * mm});
            skArc(sketch, "E942", {"start": v(128.59, -5.84) * mm, "mid": v(129.35, -5.08) * mm, "end": v(128.59, -4.31) * mm});
            skArc(sketch, "E943", {"start": v(103.95, -2.78) * mm, "mid": v(103.19, -3.54) * mm, "end": v(103.95, -4.31) * mm});
            skLineSegment(sketch, "E944.trimOffspring", {"start": v(128.53, -28.84) * mm, "end": v(128.59, -28.84) * mm});
            skArc(sketch, "E945", {"start": v(127.76, -29.9) * mm, "mid": v(127.91, -29.5) * mm, "end": v(127.8, -29.06) * mm});
            skArc(sketch, "E946.MirrorCS", {"start": v(80.55, -32.05) * mm, "mid": v(83.15, -31.18) * mm, "end": v(84.7, -28.93) * mm});
            skArc(sketch, "E947.MirrorCS", {"start": v(86.16, -26.01) * mm, "mid": v(85.33, -27.42) * mm, "end": v(84.7, -28.93) * mm});
            skArc(sketch, "E948.MirrorCS", {"start": v(96, -23) * mm, "mid": v(90.62, -23.01) * mm, "end": v(86.16, -26.01) * mm});
            skArc(sketch, "E949.MirrorCS", {"start": v(93.75, -30.26) * mm, "mid": v(98.74, -27.83) * mm, "end": v(96, -23) * mm});
            skLineSegment(sketch, "E950.MirrorCS", {"start": v(93.75, -30.26) * mm, "end": v(93.75, -32.05) * mm});
            skLineSegment(sketch, "E951.MirrorCS", {"start": v(93.75, -32.05) * mm, "end": v(123.67, -32.03) * mm});
            skLineSegment(sketch, "E952", {"start": v(80.55, -32.05) * mm, "end": v(79.22, -32.06) * mm});
            skArc(sketch, "E953.MirrorCS", {"start": v(43.75, 15.56) * mm, "mid": v(45.6, 20.05) * mm, "end": v(50.1, 21.91) * mm});
            skLineSegment(sketch, "E954.MirrorCS", {"start": v(48.5, 18.74) * mm, "end": v(48.5, 10.81) * mm});
            skArc(sketch, "E955.MirrorCS", {"start": v(48.5, 10.6) * mm, "mid": v(47.7, 9.21) * mm, "end": v(48.5, 7.82) * mm});
            skLineSegment(sketch, "E956.MirrorCS", {"start": v(48.5, 7.64) * mm, "end": v(48.5, -0.31) * mm});
            skLineSegment(sketch, "E957.MirrorCS", {"start": v(48.5, -0.31) * mm, "end": v(50.1, -0.31) * mm});
            skLineSegment(sketch, "E958.MirrorCS", {"start": v(50.1, 3.2) * mm, "end": v(50.1, -0.31) * mm});
            skArc(sketch, "E959.MirrorCS", {"start": v(53.02, 3.32) * mm, "mid": v(51.57, 2.95) * mm, "end": v(50.1, 3.2) * mm});
            skLineSegment(sketch, "E960.MirrorCS", {"start": v(53.28, 8.78) * mm, "end": v(64.1, 8.78) * mm});
            skLineSegment(sketch, "E961.MirrorCS", {"start": v(53.28, 9.67) * mm, "end": v(64.1, 9.67) * mm});
            skLineSegment(sketch, "E962.MirrorCS", {"start": v(53.28, 8.78) * mm, "end": v(53.28, 9.67) * mm});
            skLineSegment(sketch, "E963.MirrorCS", {"start": v(50.1, 7.82) * mm, "end": v(50.1, 4.2) * mm});
            skArc(sketch, "E964.MirrorCS", {"start": v(50.1, 7.82) * mm, "mid": v(50.9, 9.21) * mm, "end": v(50.1, 10.6) * mm});
            skLineSegment(sketch, "E965.MirrorCS", {"start": v(50.1, 18.74) * mm, "end": v(50.1, 10.6) * mm});
            skLineSegment(sketch, "E966.MirrorCS", {"start": v(50.1, 18.74) * mm, "end": v(48.5, 18.74) * mm});
            skArc(sketch, "E967.MirrorCS", {"start": v(53.5, 4.83) * mm, "mid": v(51.92, 3.88) * mm, "end": v(50.1, 4.2) * mm});
            skArc(sketch, "E968.MirrorCS", {"start": v(53.5, 4.83) * mm, "mid": v(58.55, 3.5) * mm, "end": v(53.34, 3.17) * mm});
            skArc(sketch, "E969.MirrorCS", {"start": v(53.02, 3.32) * mm, "mid": v(53.22, 3.32) * mm, "end": v(53.34, 3.17) * mm});
            skLineSegment(sketch, "E970.MirrorCS", {"start": v(80.55, 21.9) * mm, "end": v(79.22, 21.91) * mm});
            skArc(sketch, "E971.MirrorCS", {"start": v(54.7, 21.91) * mm, "mid": v(53.93, 21.15) * mm, "end": v(53.16, 21.91) * mm});
            skLineSegment(sketch, "E972.MirrorCS", {"start": v(54.7, 21.91) * mm, "end": v(56.23, 21.91) * mm});
            skArc(sketch, "E973.MirrorCS", {"start": v(79.22, 21.91) * mm, "mid": v(78.46, 21.15) * mm, "end": v(77.69, 21.91) * mm});
            skArc(sketch, "E974.MirrorCS", {"start": v(60.83, 21.91) * mm, "mid": v(60.06, 21.15) * mm, "end": v(59.3, 21.91) * mm});
            skLineSegment(sketch, "E975.MirrorCS", {"start": v(51.63, 21.91) * mm, "end": v(53.16, 21.91) * mm});
            skLineSegment(sketch, "E976.MirrorCS", {"start": v(73.1, 21.91) * mm, "end": v(74.62, 21.91) * mm});
            skLineSegment(sketch, "E977.MirrorCS", {"start": v(63.9, 21.91) * mm, "end": v(65.43, 21.91) * mm});
            skLineSegment(sketch, "E978.MirrorCS", {"start": v(66.96, 21.91) * mm, "end": v(68.5, 21.91) * mm});
            skLineSegment(sketch, "E979.MirrorCS", {"start": v(70.02, 21.91) * mm, "end": v(71.56, 21.91) * mm});
            skArc(sketch, "E980.MirrorCS", {"start": v(57.76, 21.91) * mm, "mid": v(57, 21.15) * mm, "end": v(56.23, 21.91) * mm});
            skArc(sketch, "E981.MirrorCS", {"start": v(66.96, 21.91) * mm, "mid": v(66.2, 21.15) * mm, "end": v(65.43, 21.91) * mm});
            skLineSegment(sketch, "E982.MirrorCS", {"start": v(57.76, 21.91) * mm, "end": v(59.3, 21.91) * mm});
            skArc(sketch, "E983.MirrorCS", {"start": v(63.9, 21.91) * mm, "mid": v(63.13, 21.15) * mm, "end": v(62.36, 21.91) * mm});
            skArc(sketch, "E984.MirrorCS", {"start": v(51.63, 21.91) * mm, "mid": v(50.86, 21.15) * mm, "end": v(50.1, 21.91) * mm});
            skLineSegment(sketch, "E985.MirrorCS", {"start": v(76.16, 21.91) * mm, "end": v(77.69, 21.91) * mm});
            skLineSegment(sketch, "E986.MirrorCS", {"start": v(60.83, 21.91) * mm, "end": v(62.36, 21.91) * mm});
            skArc(sketch, "E987.MirrorCS", {"start": v(73.1, 21.91) * mm, "mid": v(72.32, 21.15) * mm, "end": v(71.56, 21.91) * mm});
            skArc(sketch, "E988.MirrorCS", {"start": v(76.16, 21.91) * mm, "mid": v(75.39, 21.15) * mm, "end": v(74.62, 21.91) * mm});
            skArc(sketch, "E989.MirrorCS", {"start": v(70.02, 21.91) * mm, "mid": v(69.26, 21.15) * mm, "end": v(68.5, 21.91) * mm});
            skArc(sketch, "E990.MirrorCS", {"start": v(128.59, 7.95) * mm, "mid": v(129.35, 7.19) * mm, "end": v(128.59, 6.42) * mm});
            skArc(sketch, "E991.MirrorCS", {"start": v(128.59, 14.08) * mm, "mid": v(129.35, 13.32) * mm, "end": v(128.59, 12.55) * mm});
            skArc(sketch, "E992.MirrorCS", {"start": v(128.59, 4.89) * mm, "mid": v(129.35, 4.12) * mm, "end": v(128.59, 3.35) * mm});
            skArc(sketch, "E993.MirrorCS", {"start": v(103.95, -1.24) * mm, "mid": v(103.19, -0.48) * mm, "end": v(103.95, 0.29) * mm});
            skArc(sketch, "E994.MirrorCS", {"start": v(128.59, 1.82) * mm, "mid": v(129.35, 1.05) * mm, "end": v(128.59, 0.29) * mm});
            skArc(sketch, "E995.MirrorCS", {"start": v(103.95, 1.82) * mm, "mid": v(103.19, 2.59) * mm, "end": v(103.95, 3.35) * mm});
            skLineSegment(sketch, "E996.MirrorCS", {"start": v(64.71, 8.47) * mm, "end": v(64.71, 8.46) * mm});
            skArc(sketch, "E997.MirrorCS", {"start": v(128.59, -4.31) * mm, "mid": v(129.35, -5.08) * mm, "end": v(128.59, -5.84) * mm});
            skArc(sketch, "E998.MirrorCS", {"start": v(103.95, -4.31) * mm, "mid": v(103.19, -3.54) * mm, "end": v(103.95, -2.78) * mm});
            skArc(sketch, "E999.MirrorCS", {"start": v(103.95, 11.02) * mm, "mid": v(103.19, 11.78) * mm, "end": v(103.95, 12.55) * mm});
            skArc(sketch, "E1000.MirrorCS", {"start": v(103.95, 7.95) * mm, "mid": v(103.19, 8.72) * mm, "end": v(103.95, 9.49) * mm});
            skArc(sketch, "E1001.MirrorCS", {"start": v(64.72, 8.22) * mm, "mid": v(64.5, 8.6) * mm, "end": v(64.1, 8.78) * mm});
            skArc(sketch, "E1002.MirrorCS", {"start": v(64.72, 10.23) * mm, "mid": v(64.5, 9.84) * mm, "end": v(64.1, 9.67) * mm});
            skLineSegment(sketch, "E1003.MirrorCS", {"start": v(128.53, 18.68) * mm, "end": v(128.59, 18.68) * mm});
            skArc(sketch, "E1004.MirrorCS", {"start": v(128.54, 17.15) * mm, "mid": v(129.3, 16.38) * mm, "end": v(128.54, 15.62) * mm});
            skLineSegment(sketch, "E1005.MirrorCS", {"start": v(48.5, 7.82) * mm, "end": v(48.5, 7.64) * mm});
            skArc(sketch, "E1006.MirrorCS", {"start": v(103.95, 4.89) * mm, "mid": v(103.19, 5.65) * mm, "end": v(103.95, 6.42) * mm});
            skArc(sketch, "E1007.MirrorCS", {"start": v(128.59, -1.24) * mm, "mid": v(129.35, -2.01) * mm, "end": v(128.59, -2.78) * mm});
            skLineSegment(sketch, "E1008.MirrorCS", {"start": v(48.5, 10.81) * mm, "end": v(48.5, 10.6) * mm});
            skArc(sketch, "E1009.MirrorCS", {"start": v(128.59, 11.02) * mm, "mid": v(129.35, 10.25) * mm, "end": v(128.59, 9.49) * mm});
            skArc(sketch, "E1010.MirrorCS", {"start": v(127.76, 19.76) * mm, "mid": v(127.91, 19.34) * mm, "end": v(127.8, 18.91) * mm});
            skLineSegment(sketch, "E1011.MirrorCS", {"start": v(93.75, 20.1) * mm, "end": v(93.75, 21.9) * mm});
            skArc(sketch, "E1012.MirrorCS", {"start": v(103.95, 14.08) * mm, "mid": v(103.19, 14.85) * mm, "end": v(103.95, 15.62) * mm});
            skArc(sketch, "E1013.MirrorCS", {"start": v(123.67, 21.88) * mm, "mid": v(125.91, 21.2) * mm, "end": v(127.76, 19.76) * mm});
            skLineSegment(sketch, "E1014.MirrorCS", {"start": v(94.99, -1.9) * mm, "end": v(94.53, -1.1) * mm});
            skArc(sketch, "E1015.MirrorCS", {"start": v(127.8, 18.91) * mm, "mid": v(127.55, 18.74) * mm, "end": v(127.26, 18.68) * mm});
            skLineSegment(sketch, "E1016.MirrorCS", {"start": v(94.53, -1.1) * mm, "end": v(89.95, -1.1) * mm});
            skLineSegment(sketch, "E1017.MirrorCS", {"start": v(98.65, -1.9) * mm, "end": v(94.99, -1.9) * mm});
            skArc(sketch, "E1018.MirrorCS", {"start": v(103.95, 17.15) * mm, "mid": v(103.19, 17.92) * mm, "end": v(103.95, 18.68) * mm});
            skLineSegment(sketch, "E1019.MirrorCS", {"start": v(89.95, -1.1) * mm, "end": v(89.49, -0.31) * mm});
            skLineSegment(sketch, "E1020.MirrorCS", {"start": v(60.94, 8.46) * mm, "end": v(60.95, 8.46) * mm});
            skLineSegment(sketch, "E1021.MirrorCS", {"start": v(60.94, 9.99) * mm, "end": v(60.95, 9.99) * mm});
            skArc(sketch, "E1022.MirrorCS", {"start": v(86.16, 15.86) * mm, "mid": v(85.33, 17.27) * mm, "end": v(84.7, 18.77) * mm});
            skLineSegment(sketch, "E1023.MirrorCS", {"start": v(83.99, -0.31) * mm, "end": v(83.07, 1.27) * mm});
            skLineSegment(sketch, "E1024.MirrorCS", {"start": v(100.49, -5.08) * mm, "end": v(98.65, -1.9) * mm});
            skLineSegment(sketch, "E1025.MirrorCS", {"start": v(75.74, 1.27) * mm, "end": v(72.07, -5.08) * mm});
            skLineSegment(sketch, "E1026.MirrorCS", {"start": v(103.95, 12.55) * mm, "end": v(128.59, 12.55) * mm});
            skLineSegment(sketch, "E1027.MirrorCS", {"start": v(83.07, 1.27) * mm, "end": v(75.74, 1.27) * mm});
            skLineSegment(sketch, "E1028.MirrorCS", {"start": v(103.95, 6.42) * mm, "end": v(128.59, 6.42) * mm});
            skLineSegment(sketch, "E1029.MirrorCS", {"start": v(128.54, 17.15) * mm, "end": v(103.95, 17.15) * mm});
            skLineSegment(sketch, "E1030.MirrorCS", {"start": v(93.75, 21.9) * mm, "end": v(123.67, 21.88) * mm});
            skArc(sketch, "E1031.MirrorCS", {"start": v(96, 12.84) * mm, "mid": v(90.62, 12.86) * mm, "end": v(86.16, 15.86) * mm});
            skLineSegment(sketch, "E1032.MirrorCS", {"start": v(103.95, 18.68) * mm, "end": v(127.26, 18.68) * mm});
            skPoint(sketch, "E1033.MirrorP", {"position": v(53.28, 9.23) * mm});
            skArc(sketch, "E1034.MirrorCS", {"start": v(93.75, 20.1) * mm, "mid": v(98.74, 17.67) * mm, "end": v(96, 12.84) * mm});
            skLineSegment(sketch, "E1035.MirrorCS", {"start": v(128.59, -4.31) * mm, "end": v(103.95, -4.31) * mm});
            skPoint(sketch, "E1036.MirrorP", {"position": v(73.9, -1.9) * mm});
            skLineSegment(sketch, "E1037.MirrorCS", {"start": v(103.95, 15.62) * mm, "end": v(128.54, 15.62) * mm});
            skLineSegment(sketch, "E1038.MirrorCS", {"start": v(128.59, 11.02) * mm, "end": v(103.95, 11.02) * mm});
            skPoint(sketch, "E1039.MirrorP", {"position": v(123, 21.91) * mm});
            skPoint(sketch, "E1040.MirrorP", {"position": v(53.5, 4.83) * mm});
            skLineSegment(sketch, "E1041.MirrorCS", {"start": v(128.59, -1.24) * mm, "end": v(103.95, -1.24) * mm});
            skLineSegment(sketch, "E1042.MirrorCS", {"start": v(103.95, 9.49) * mm, "end": v(128.59, 9.49) * mm});
            skArc(sketch, "E1043.MirrorCS", {"start": v(64.72, 10.23) * mm, "mid": v(77.48, 9.2) * mm, "end": v(64.72, 8.24) * mm});
            skPoint(sketch, "E1044.MirrorP", {"position": v(53.53, 4.86) * mm});
            skArc(sketch, "E1045.MirrorCS", {"start": v(80.55, 21.9) * mm, "mid": v(83.15, 21.03) * mm, "end": v(84.7, 18.77) * mm});
            skLineSegment(sketch, "E1046.MirrorCS", {"start": v(103.95, 0.29) * mm, "end": v(128.59, 0.29) * mm});
            skLineSegment(sketch, "E1047.MirrorCS", {"start": v(89.49, -0.31) * mm, "end": v(83.99, -0.31) * mm});
            skLineSegment(sketch, "E1048.MirrorCS", {"start": v(128.59, 7.95) * mm, "end": v(103.95, 7.95) * mm});
            skPoint(sketch, "E1049.MirrorP", {"position": v(129.97, 20.62) * mm});
            skLineSegment(sketch, "E1050.MirrorCS", {"start": v(128.59, 14.08) * mm, "end": v(103.95, 14.08) * mm});
            skLineSegment(sketch, "E1051.MirrorCS", {"start": v(128.59, 4.89) * mm, "end": v(103.95, 4.89) * mm});
            skLineSegment(sketch, "E1052.MirrorCS", {"start": v(103.95, 3.35) * mm, "end": v(128.59, 3.35) * mm});
            skLineSegment(sketch, "E1053.MirrorCS", {"start": v(103.95, -2.78) * mm, "end": v(128.59, -2.78) * mm});
            skLineSegment(sketch, "E1054.MirrorCS", {"start": v(128.59, 1.82) * mm, "end": v(103.95, 1.82) * mm});
            skLineSegment(sketch, "E1055", {"start": v(43.75, -25.71) * mm, "end": v(43.75, 15.56) * mm});
            skArc(sketch, "E1056", {"start": v(67.7, -0.77) * mm, "mid": v(66.45, -5.07) * mm, "end": v(67.83, -9.34) * mm});
            skArc(sketch, "E1057", {"start": v(61.47, -3.49) * mm, "mid": v(62.03, -3.74) * mm, "end": v(62.64, -3.85) * mm});
            skArc(sketch, "E1058", {"start": v(63.61, -3.76) * mm, "mid": v(64.3, -3.4) * mm, "end": v(64.63, -2.7) * mm});
            skArc(sketch, "E1059", {"start": v(60.09, -2.7) * mm, "mid": v(60.12, -3.04) * mm, "end": v(60.2, -3.39) * mm});
            skArc(sketch, "E1060", {"start": v(60.2, -3.39) * mm, "mid": v(60.37, -3.82) * mm, "end": v(60.63, -4.2) * mm});
            skArc(sketch, "E1061", {"start": v(60.63, -4.2) * mm, "mid": v(61.02, -4.55) * mm, "end": v(61.5, -4.8) * mm});
            skArc(sketch, "E1062", {"start": v(61.5, -4.8) * mm, "mid": v(62.05, -4.96) * mm, "end": v(62.64, -5.02) * mm});
            skArc(sketch, "E1063", {"start": v(62.64, -5.02) * mm, "mid": v(62.64, -5.02) * mm, "end": v(62.64, -5.02) * mm});
            skArc(sketch, "E1064", {"start": v(63.45, -4.99) * mm, "mid": v(63.83, -4.92) * mm, "end": v(64.2, -4.8) * mm});
            skArc(sketch, "E1065", {"start": v(64.2, -4.8) * mm, "mid": v(64.5, -4.65) * mm, "end": v(64.76, -4.47) * mm});
            skArc(sketch, "E1066", {"start": v(64.76, -4.47) * mm, "mid": v(65.02, -4.22) * mm, "end": v(65.24, -3.92) * mm});
            skArc(sketch, "E1067", {"start": v(65.24, -3.92) * mm, "mid": v(65.4, -3.57) * mm, "end": v(65.5, -3.2) * mm});
            skArc(sketch, "E1068", {"start": v(65.5, -3.2) * mm, "mid": v(65.55, -2.97) * mm, "end": v(65.57, -2.73) * mm});
            skArc(sketch, "E1069", {"start": v(65.57, -2.73) * mm, "mid": v(65.57, -2.71) * mm, "end": v(65.57, -2.7) * mm});
            skLineSegment(sketch, "E1070", {"start": v(61.03, -2.5) * mm, "end": v(61.03, -2.5) * mm});
            skLineSegment(sketch, "E1071", {"start": v(64.64, -2.49) * mm, "end": v(64.65, -2.49) * mm});
            skLineSegment(sketch, "E1072.trimOffspring", {"start": v(61.05, -2.7) * mm, "end": v(60.08, -2.7) * mm});
            skLineSegment(sketch, "E1073", {"start": v(65.1, -2.7) * mm, "end": v(65.57, -2.7) * mm});
            skArc(sketch, "E1074.trimOffspring", {"start": v(65.58, -2.49) * mm, "mid": v(65.58, -2.48) * mm, "end": v(65.58, -2.48) * mm});
            skLineSegment(sketch, "E1075.trimOffspring", {"start": v(64.63, -2.7) * mm, "end": v(65.1, -2.7) * mm});
            skArc(sketch, "E1076.trimOffspring", {"start": v(61.05, -2.7) * mm, "mid": v(61.2, -3.13) * mm, "end": v(61.47, -3.49) * mm});
            skPoint(sketch, "E1077.orphan", {"position": v(62.9, -3.86) * mm});
            skArc(sketch, "E1078.MirrorCS", {"start": v(61.04, -2.31) * mm, "mid": v(61.19, -1.87) * mm, "end": v(61.46, -1.5) * mm});
            skArc(sketch, "E1079.MirrorCS", {"start": v(61.46, -1.5) * mm, "mid": v(62.02, -1.26) * mm, "end": v(62.62, -1.13) * mm});
            skArc(sketch, "E1080.MirrorCS", {"start": v(63.6, -1.22) * mm, "mid": v(64.3, -1.58) * mm, "end": v(64.63, -2.28) * mm});
            skArc(sketch, "E1081.MirrorCS", {"start": v(65.57, -2.23) * mm, "mid": v(65.57, -2.25) * mm, "end": v(65.57, -2.27) * mm});
            skArc(sketch, "E1082.MirrorCS", {"start": v(65.5, -1.75) * mm, "mid": v(65.54, -1.99) * mm, "end": v(65.57, -2.23) * mm});
            skArc(sketch, "E1083.MirrorCS", {"start": v(65.23, -1.05) * mm, "mid": v(65.4, -1.39) * mm, "end": v(65.5, -1.75) * mm});
            skArc(sketch, "E1084.MirrorCS", {"start": v(64.74, -0.5) * mm, "mid": v(65, -0.75) * mm, "end": v(65.23, -1.05) * mm});
            skArc(sketch, "E1085.MirrorCS", {"start": v(64.18, -0.18) * mm, "mid": v(64.47, -0.31) * mm, "end": v(64.74, -0.5) * mm});
            skArc(sketch, "E1086.MirrorCS", {"start": v(63.43, 0) * mm, "mid": v(63.8, -0.06) * mm, "end": v(64.18, -0.18) * mm});
            skArc(sketch, "E1087.MirrorCS", {"start": v(62.61, 0.04) * mm, "mid": v(62.62, 0.04) * mm, "end": v(62.62, 0.04) * mm});
            skArc(sketch, "E1088.MirrorCS", {"start": v(61.47, -0.2) * mm, "mid": v(62.03, -0.03) * mm, "end": v(62.61, 0.04) * mm});
            skArc(sketch, "E1089.MirrorCS", {"start": v(60.61, -0.8) * mm, "mid": v(61, -0.45) * mm, "end": v(61.47, -0.2) * mm});
            skArc(sketch, "E1090.MirrorCS", {"start": v(60.2, -1.62) * mm, "mid": v(60.36, -1.2) * mm, "end": v(60.61, -0.8) * mm});
            skArc(sketch, "E1091.MirrorCS", {"start": v(60.08, -2.32) * mm, "mid": v(60.12, -1.97) * mm, "end": v(60.2, -1.62) * mm});
            skLineSegment(sketch, "E1092.MirrorCS", {"start": v(61.04, -2.31) * mm, "end": v(60.08, -2.32) * mm});
            skLineSegment(sketch, "E1093.MirrorCS", {"start": v(64.63, -2.28) * mm, "end": v(65.1, -2.27) * mm});
            skLineSegment(sketch, "E1094.MirrorCS", {"start": v(65.1, -2.27) * mm, "end": v(65.57, -2.27) * mm});
            skArc(sketch, "E1095", {"start": v(64.65, -2.49) * mm, "mid": v(64.65, -2.49) * mm, "end": v(64.65, -2.48) * mm});
            skLineSegment(sketch, "E1096.0", {"start": v(63.02, -5.03) * mm, "end": v(63.01, -3.86) * mm});
            skLineSegment(sketch, "E1097.0", {"start": v(62.64, -5.03) * mm, "end": v(62.64, -3.85) * mm});
            skLineSegment(sketch, "E1098.trimOffspring", {"start": v(62.62, -1.13) * mm, "end": v(62.62, 0.04) * mm});
            skPoint(sketch, "E1099.orphan", {"position": v(62.83, -2.5) * mm});
            skLineSegment(sketch, "E1100.trimOffspring", {"start": v(63, -1.12) * mm, "end": v(63, 0.04) * mm});
            skPoint(sketch, "E1101.MirrorCS.end.orphan", {"position": v(64.65, -2.48) * mm});
            skPoint(sketch, "E1101.MirrorCS.start.orphan", {"position": v(64.63, -2.28) * mm});
            skPoint(sketch, "E1102.MirrorCS.end.orphan", {"position": v(65.58, -2.1) * mm});
            skPoint(sketch, "E1102.MirrorCS.start.orphan", {"position": v(65.57, -1.89) * mm});
            skPoint(sketch, "E1103.orphan", {"position": v(60.08, -2.5) * mm});
            skPoint(sketch, "E1104.MirrorCS.end.orphan", {"position": v(61.04, -2.31) * mm});
            skArc(sketch, "E1105.trimOffspring", {"start": v(63.02, -5.03) * mm, "mid": v(63.23, -5.01) * mm, "end": v(63.45, -4.99) * mm});
            skArc(sketch, "E1106.trimOffspring", {"start": v(63.01, -3.86) * mm, "mid": v(63.32, -3.83) * mm, "end": v(63.61, -3.76) * mm});
            skArc(sketch, "E1107.trimOffspring", {"start": v(63, -1.12) * mm, "mid": v(63.3, -1.15) * mm, "end": v(63.6, -1.22) * mm});
            skArc(sketch, "E1108.trimOffspring", {"start": v(63, 0.04) * mm, "mid": v(63.21, 0.03) * mm, "end": v(63.43, 0) * mm});
            skText(sketch, "E1109", { "text": "X", "fontName": "OpenSans-Bold.ttf"});
            skLineSegment(sketch, "E1110", {"start": v(68.96, -0.77) * mm, "end": v(67.7, -0.77) * mm});
            skLineSegment(sketch, "E1111", {"start": v(67.7, -0.77) * mm, "end": v(68.96, -0.77) * mm});
            skCircle(sketch, "E1112", {"center": v(62.83, -2.5) * mm, "radius": 0.65 * mm});
            skArc(sketch, "E1113.0", {"start": v(68.96, -0.77) * mm, "mid": v(67.47, -5.08) * mm, "end": v(69.11, -9.34) * mm});
            skLineSegment(sketch, "E1114", {"start": v(67.83, -9.34) * mm, "end": v(69.11, -9.34) * mm});
            const initialGuessF0  = {"E80": [-0.01316, -0.01779, 0, 1, 0.01006], "E290": [-0.07819, 0.05662, 0, 1, 0.01006], "E351": [-0.09987, 0.07539, 0, 1, 0.0075], "E590": [-0.08662, -0.00219, 1, 0, 0.0075], "E851": [0.0652, 0.05447, 0, 1, 0.005], "E1109": [0.0652, -0.0105, 0, 1, 0.005]};
            skSetInitialGuess(sketch, initialGuessF0);
            skSolve(sketch);
        }
        {
            var Q0;
            Q0=qSketchRegion(id+"F0",true);
            extrude(context, id + "F1", {"entities" : qUnion([Q0]), "depth" : 3.17 * mm, "offsetDistance" : 25.4 * mm});
        }
        {
            var Q0;
            Q0=makeQuery(id+"F1.opExtrude","SWEPT_EDGE",EDGE,{"disambiguationData":[OSD([sQuery(id+"F0.wireOp",EDGE,"E3.filletArc"),sQuery(id+"F0.wireOp",EDGE,"KwcFEo9U-bClh-D8h3-GzTv-NhEbKNvI21TT")])]});
            var Q1;
            Q1=makeQuery(id+"F1.opExtrude","SWEPT_EDGE",EDGE,{"disambiguationData":[OSD([sQuery(id+"F0.wireOp",EDGE,"E7MvMFNV-uK8b-8ZiQ-7Duk-cUjbGVXh6u7s"),sQuery(id+"F0.wireOp",EDGE,"0ab612f3-548e-47c6-a8b8-d151de601088.trimOffspring")])]});
            var Q2;
            Q2=makeQuery(id+"F1.opExtrude","SWEPT_EDGE",EDGE,{"disambiguationData":[OSD([sQuery(id+"F0.wireOp",EDGE,"MFMcjicZ-tfMV-cnA4-Z9pC-shCIlQqRngmt"),sQuery(id+"F0.wireOp",EDGE,"49b1c2fe-dd47-4412-b7ba-a2595802a9c0.trimOffspring")])]});
            var Q3;
            Q3=makeQuery(id+"F1.opExtrude","SWEPT_EDGE",EDGE,{"disambiguationData":[OSD([sQuery(id+"F0.wireOp",EDGE,"hqcUmv8U-3Y2f-1DYb-XFRx-DoM0Ldty7pgK"),sQuery(id+"F0.wireOp",EDGE,"0ab612f3-548e-47c6-a8b8-d151de601088.trimOffspring")])]});
            var Q4;
            Q4=makeQuery(id+"F1.opExtrude","SWEPT_EDGE",EDGE,{"disambiguationData":[OSD([sQuery(id+"F0.wireOp",EDGE,"BDxbyBsN-WUfq-DDqC-Ylty-fahBLUCrJihu"),sQuery(id+"F0.wireOp",EDGE,"49b1c2fe-dd47-4412-b7ba-a2595802a9c0.trimOffspring")])]});
            var Q5;
            Q5=makeQuery(id+"F1.opExtrude","SWEPT_EDGE",EDGE,{"disambiguationData":[OSD([sQuery(id+"F0.wireOp",EDGE,"qLwkn0zT-rJZj-oCyo-4JJa-DjERWgxp8KWt"),sQuery(id+"F0.wireOp",EDGE,"457cc2dd-0a22-47f4-a5e9-31956becaa98.trimOffspring")])]});
            var Q6;
            Q6=makeQuery(id+"F1.opExtrude","SWEPT_EDGE",EDGE,{"disambiguationData":[OSD([sQuery(id+"F0.wireOp",EDGE,"QbkmLgDQ-2k58-Ziiz-fUbB-J4hHGqKfhEZH"),sQuery(id+"F0.wireOp",EDGE,"6d273b1b-6e05-4ff9-b154-a73bd32e1f71.trimOffspring")])]});
            var Q7;
            Q7=makeQuery(id+"F1.opExtrude","SWEPT_EDGE",EDGE,{"disambiguationData":[OSD([sQuery(id+"F0.wireOp",EDGE,"QKDGq1wy-vTCk-Lj4D-VITr-jcaQ08ZgOf7o"),sQuery(id+"F0.wireOp",EDGE,"1e7fb99e-4ad8-4cc2-a7fa-02e236824d87.trimOffspring")])]});
            var Q8;
            Q8=makeQuery(id+"F1.opExtrude","SWEPT_EDGE",EDGE,{"disambiguationData":[OSD([sQuery(id+"F0.wireOp",EDGE,"cXYAuPDi-3OGr-QPoA-gxEK-N9iT9CviMBYx"),sQuery(id+"F0.wireOp",EDGE,"49480ebe-8ed0-4ae2-94ab-956c5f313c19.trimOffspring")])]});
            var Q9;
            Q9=makeQuery(id+"F1.opExtrude","SWEPT_EDGE",EDGE,{"disambiguationData":[OSD([sQuery(id+"F0.wireOp",EDGE,"hI7Z9iwd-lZgc-Dfsw-L6mG-scNOy0WF6EC7"),sQuery(id+"F0.wireOp",EDGE,"2a180a66-34a1-4841-8f87-04e5eba1ceab.trimOffspring")])]});
            var Q10;
            Q10=makeQuery(id+"F1.opExtrude","SWEPT_EDGE",EDGE,{"disambiguationData":[OSD([sQuery(id+"F0.wireOp",EDGE,"c8rfMAqR-dkwd-qCW3-9neE-H0AE0oPbs4Qp"),sQuery(id+"F0.wireOp",EDGE,"401ab048-5759-4413-abed-1134ba47fddd.trimOffspring")])]});
            var Q11;
            Q11=makeQuery(id+"F1.opExtrude","SWEPT_EDGE",EDGE,{"disambiguationData":[OSD([sQuery(id+"F0.wireOp",EDGE,"XWb4HBB5-t2Hc-oUr3-o6c1-bTJZQE5nsMn5"),sQuery(id+"F0.wireOp",EDGE,"39d9c749-9ffb-4b8e-ae83-386e5194df48.trimOffspring")])]});
            var Q12;
            Q12=makeQuery(id+"F1.opExtrude","SWEPT_EDGE",EDGE,{"disambiguationData":[OSD([sQuery(id+"F0.wireOp",EDGE,"BWBwDpZV-HqS4-YjK9-sSWS-v8iRheQrnra1"),sQuery(id+"F0.wireOp",EDGE,"fe6c2a4a-91f1-4b4e-b1e2-6b86066d8226.trimOffspring")])]});
            var Q13;
            Q13=makeQuery(id+"F1.opExtrude","SWEPT_EDGE",EDGE,{"disambiguationData":[OSD([sQuery(id+"F0.wireOp",EDGE,"DpMHMzxM-oLeH-X24q-mFt2-Zfh6rWlBPqLy"),sQuery(id+"F0.wireOp",EDGE,"e7940485-faa3-4b5d-8451-879a44a0535b.trimOffspring")])]});
            var Q14;
            Q14=makeQuery(id+"F1.opExtrude","SWEPT_EDGE",EDGE,{"disambiguationData":[OSD([sQuery(id+"F0.wireOp",EDGE,"8p8z02rz-XM1F-gFPC-RQVa-rfRN30CTPnuF"),sQuery(id+"F0.wireOp",EDGE,"cf35a97e-a59c-43df-8749-063313af8aeb.trimOffspring")])]});
            var Q15;
            Q15=makeQuery(id+"F1.opExtrude","SWEPT_EDGE",EDGE,{"disambiguationData":[OSD([sQuery(id+"F0.wireOp",EDGE,"1KdZPy54-IAHz-HdOO-9pBj-XyZoVR0dbeO1"),sQuery(id+"F0.wireOp",EDGE,"4941a0d5-5b4d-4c2d-bee2-9b9f4ed584f5.trimOffspring")])]});
            var Q16;
            Q16=makeQuery(id+"F1.opExtrude","SWEPT_EDGE",EDGE,{"disambiguationData":[OSD([sQuery(id+"F0.wireOp",EDGE,"D77W7Ugb-ZPTO-vBp9-5ZPV-knq85JaC9yaM"),sQuery(id+"F0.wireOp",EDGE,"105bb943-4d21-436c-ae5a-a526161733bb.trimOffspring")])]});
            var Q17;
            Q17=makeQuery(id+"F1.opExtrude","SWEPT_EDGE",EDGE,{"disambiguationData":[OSD([sQuery(id+"F0.wireOp",EDGE,"E0.right"),sQuery(id+"F0.wireOp",EDGE,"itbIzTSW-YEBt-L2aj-MggJ-UpqGRpPm7y69")])]});
            var Q18;
            Q18=makeQuery(id+"F1.opExtrude","SWEPT_EDGE",EDGE,{"disambiguationData":[OSD([sQuery(id+"F0.wireOp",EDGE,"KvrqN5Q7-6TQ0-ukyS-9HFH-Bqw6vbqitdDL"),sQuery(id+"F0.wireOp",EDGE,"457cc2dd-0a22-47f4-a5e9-31956becaa98.trimOffspring")])]});
            var Q19;
            Q19=makeQuery(id+"F1.opExtrude","SWEPT_EDGE",EDGE,{"disambiguationData":[OSD([sQuery(id+"F0.wireOp",EDGE,"92eDQtEN-0jaI-xoSh-TXxB-fUASiIEMQFeJ"),sQuery(id+"F0.wireOp",EDGE,"6d273b1b-6e05-4ff9-b154-a73bd32e1f71.trimOffspring")])]});
            var Q20;
            Q20=makeQuery(id+"F1.opExtrude","SWEPT_EDGE",EDGE,{"disambiguationData":[OSD([sQuery(id+"F0.wireOp",EDGE,"5c0QZ8NB-kqrX-tXYX-rwGu-YhZIMP3kNjtv"),sQuery(id+"F0.wireOp",EDGE,"1e7fb99e-4ad8-4cc2-a7fa-02e236824d87.trimOffspring")])]});
            var Q21;
            Q21=makeQuery(id+"F1.opExtrude","SWEPT_EDGE",EDGE,{"disambiguationData":[OSD([sQuery(id+"F0.wireOp",EDGE,"Co8MspyC-jpgy-OqRi-9X62-KS5NYQvcvOHt"),sQuery(id+"F0.wireOp",EDGE,"49480ebe-8ed0-4ae2-94ab-956c5f313c19.trimOffspring")])]});
            var Q22;
            Q22=makeQuery(id+"F1.opExtrude","SWEPT_EDGE",EDGE,{"disambiguationData":[OSD([sQuery(id+"F0.wireOp",EDGE,"N0CfcBmX-WNQ3-BAAi-rMmY-l0h40gDwQezy"),sQuery(id+"F0.wireOp",EDGE,"2a180a66-34a1-4841-8f87-04e5eba1ceab.trimOffspring")])]});
            var Q23;
            Q23=makeQuery(id+"F1.opExtrude","SWEPT_EDGE",EDGE,{"disambiguationData":[OSD([sQuery(id+"F0.wireOp",EDGE,"frJKysNw-LHww-dgYr-2R5g-6tPWvze6kZkP"),sQuery(id+"F0.wireOp",EDGE,"401ab048-5759-4413-abed-1134ba47fddd.trimOffspring")])]});
            var Q24;
            Q24=makeQuery(id+"F1.opExtrude","SWEPT_EDGE",EDGE,{"disambiguationData":[OSD([sQuery(id+"F0.wireOp",EDGE,"ioAGfyNb-zQ6n-KKhh-X4Rq-4gnoXz22f1pc"),sQuery(id+"F0.wireOp",EDGE,"39d9c749-9ffb-4b8e-ae83-386e5194df48.trimOffspring")])]});
            var Q25;
            Q25=makeQuery(id+"F1.opExtrude","SWEPT_EDGE",EDGE,{"disambiguationData":[OSD([sQuery(id+"F0.wireOp",EDGE,"4Z05me6M-pVjN-uT1z-6B9z-4clwtVMk1WCp"),sQuery(id+"F0.wireOp",EDGE,"fe6c2a4a-91f1-4b4e-b1e2-6b86066d8226.trimOffspring")])]});
            var Q26;
            Q26=makeQuery(id+"F1.opExtrude","SWEPT_EDGE",EDGE,{"disambiguationData":[OSD([sQuery(id+"F0.wireOp",EDGE,"CTEV1Vwn-BGBE-jlHb-FHnF-PdhdXIVbAuRO"),sQuery(id+"F0.wireOp",EDGE,"e7940485-faa3-4b5d-8451-879a44a0535b.trimOffspring")])]});
            var Q27;
            Q27=makeQuery(id+"F1.opExtrude","SWEPT_EDGE",EDGE,{"disambiguationData":[OSD([sQuery(id+"F0.wireOp",EDGE,"vmLdqNc3-eLYz-mePX-fzRX-2egRdkYDBIuf"),sQuery(id+"F0.wireOp",EDGE,"cf35a97e-a59c-43df-8749-063313af8aeb.trimOffspring")])]});
            var Q28;
            Q28=makeQuery(id+"F1.opExtrude","SWEPT_EDGE",EDGE,{"disambiguationData":[OSD([sQuery(id+"F0.wireOp",EDGE,"uBCBu26M-MPGh-sdtj-RZAV-gj2qaw1dCL6s"),sQuery(id+"F0.wireOp",EDGE,"4941a0d5-5b4d-4c2d-bee2-9b9f4ed584f5.trimOffspring")])]});
            var Q29;
            Q29=makeQuery(id+"F1.opExtrude","SWEPT_EDGE",EDGE,{"disambiguationData":[OSD([sQuery(id+"F0.wireOp",EDGE,"AOzfUuVY-sAip-yR5B-ZQbZ-Zymy6F6M52jt"),sQuery(id+"F0.wireOp",EDGE,"105bb943-4d21-436c-ae5a-a526161733bb.trimOffspring")])]});
            fillet(context, id + "F2", {"entities" : qUnion([Q0, Q1, Q2, Q3, Q4, Q5, Q6, Q7, Q8, Q9, Q10, Q11, Q12, Q13, Q14, Q15, Q16, Q17, Q18, Q19, Q20, Q21, Q22, Q23, Q24, Q25, Q26, Q27, Q28, Q29]), "radius" : 0.5 * mm, "tangentPropagation" : true, "allowEdgeOverflow" : false});
        }
        {
            var Q0;
            Q0=makeQuery(id+"F1.opExtrude","CAP_EDGE",EDGE,{"disambiguationData":[OSD([sQuery(id+"F0.wireOp",EDGE,"E18")])],"isStart":false});
            var Q1;
            Q1=makeQuery(id+"F1.opExtrude","CAP_EDGE",EDGE,{"disambiguationData":[OSD([sQuery(id+"F0.wireOp",EDGE,"E210.trimOffspring")])],"isStart":false});
            var Q2;
            Q2=makeQuery(id+"F1.opExtrude","CAP_EDGE",EDGE,{"disambiguationData":[OSD([sQuery(id+"F0.wireOp",EDGE,"E212.trimOffspring")])],"isStart":false});
            var Q3;
            Q3=makeQuery(id+"F1.opExtrude","CAP_EDGE",EDGE,{"disambiguationData":[OSD([sQuery(id+"F0.wireOp",EDGE,"E16")])],"isStart":false});
            var Q4;
            Q4=makeQuery(id+"F1.opExtrude","CAP_EDGE",EDGE,{"disambiguationData":[OSD([sQuery(id+"F0.wireOp",EDGE,"E206.trimOffspring")])],"isStart":false});
            var Q5;
            Q5=makeQuery(id+"F1.opExtrude","CAP_EDGE",EDGE,{"disambiguationData":[OSD([sQuery(id+"F0.wireOp",EDGE,"E201.trimOffspring")])],"isStart":false});
            var Q6;
            Q6=makeQuery(id+"F1.opExtrude","CAP_EDGE",EDGE,{"disambiguationData":[OSD([sQuery(id+"F0.wireOp",EDGE,"E6"),sQuery(id+"F0.wireOp",EDGE,"E203")])],"isStart":true});
            var Q7;
            Q7=makeQuery(id+"F1.opExtrude","CAP_EDGE",EDGE,{"disambiguationData":[OSD([sQuery(id+"F0.wireOp",EDGE,"E192.trimOffspring"),sQuery(id+"F0.wireOp",EDGE,"E211.trimOffspring")])],"isStart":true});
            var Q8;
            Q8=makeQuery(id+"F1.opExtrude","CAP_EDGE",EDGE,{"disambiguationData":[OSD([sQuery(id+"F0.wireOp",EDGE,"E194.trimOffspring"),sQuery(id+"F0.wireOp",EDGE,"E196")])],"isStart":true});
            var Q9;
            Q9=makeQuery(id+"F1.opExtrude","CAP_EDGE",EDGE,{"disambiguationData":[OSD([sQuery(id+"F0.wireOp",EDGE,"E9.MirrorCS"),sQuery(id+"F0.wireOp",EDGE,"E199.trimOffspring")])],"isStart":true});
            var Q10;
            Q10=makeQuery(id+"F1.opExtrude","CAP_EDGE",EDGE,{"disambiguationData":[OSD([sQuery(id+"F0.wireOp",EDGE,"E206.trimOffspring")])],"isStart":true});
            var Q11;
            Q11=makeQuery(id+"F1.opExtrude","CAP_EDGE",EDGE,{"disambiguationData":[OSD([sQuery(id+"F0.wireOp",EDGE,"E16")])],"isStart":true});
            var Q12;
            Q12=makeQuery(id+"F1.opExtrude","CAP_EDGE",EDGE,{"disambiguationData":[OSD([sQuery(id+"F0.wireOp",EDGE,"E201.trimOffspring")])],"isStart":true});
            var Q13;
            Q13=makeQuery(id+"F1.opExtrude","CAP_EDGE",EDGE,{"disambiguationData":[OSD([sQuery(id+"F0.wireOp",EDGE,"E18")])],"isStart":true});
            var Q14;
            Q14=makeQuery(id+"F1.opExtrude","CAP_EDGE",EDGE,{"disambiguationData":[OSD([sQuery(id+"F0.wireOp",EDGE,"E210.trimOffspring")])],"isStart":true});
            var Q15;
            Q15=makeQuery(id+"F1.opExtrude","CAP_EDGE",EDGE,{"disambiguationData":[OSD([sQuery(id+"F0.wireOp",EDGE,"E212.trimOffspring")])],"isStart":true});
            var Q16;
            Q16=makeQuery(id+"F1.opExtrude","CAP_EDGE",EDGE,{"disambiguationData":[OSD([sQuery(id+"F0.wireOp",EDGE,"E192.trimOffspring"),sQuery(id+"F0.wireOp",EDGE,"E211.trimOffspring")])],"isStart":false});
            var Q17;
            Q17=makeQuery(id+"F1.opExtrude","CAP_EDGE",EDGE,{"disambiguationData":[OSD([sQuery(id+"F0.wireOp",EDGE,"E6"),sQuery(id+"F0.wireOp",EDGE,"E203")])],"isStart":false});
            var Q18;
            Q18=makeQuery(id+"F1.opExtrude","CAP_EDGE",EDGE,{"disambiguationData":[OSD([sQuery(id+"F0.wireOp",EDGE,"E194.trimOffspring"),sQuery(id+"F0.wireOp",EDGE,"E196")])],"isStart":false});
            var Q19;
            Q19=makeQuery(id+"F1.opExtrude","CAP_EDGE",EDGE,{"disambiguationData":[OSD([sQuery(id+"F0.wireOp",EDGE,"E9.MirrorCS"),sQuery(id+"F0.wireOp",EDGE,"E199.trimOffspring")])],"isStart":false});
            fillet(context, id + "F3", {"entities" : qUnion([Q0, Q1, Q2, Q3, Q4, Q5, Q6, Q7, Q8, Q9, Q10, Q11, Q12, Q13, Q14, Q15, Q16, Q17, Q18, Q19]), "radius" : 0.5 * mm, "tangentPropagation" : true, "allowEdgeOverflow" : false});
        }
        {
            var Q0;
            Q0=makeQuery(id+"F1.opExtrude","CAP_FACE",FACE,{"disambiguationData":[OSD([sQuery(id+"F0.wireOp",EDGE,"E0.bottom"),sQuery(id+"F0.wireOp",EDGE,"E0.top"),sQuery(id+"F0.wireOp",EDGE,"E0.left"),sQuery(id+"F0.wireOp",EDGE,"E0.right"),sQuery(id+"F0.wireOp",EDGE,"E1.filletArc"),sQuery(id+"F0.wireOp",EDGE,"E2.filletArc"),sQuery(id+"F0.wireOp",EDGE,"E3.filletArc"),sQuery(id+"F0.wireOp",EDGE,"E4.filletArc"),sQuery(id+"F0.wireOp",EDGE,"E5"),sQuery(id+"F0.wireOp",EDGE,"E6"),sQuery(id+"F0.wireOp",EDGE,"E7"),sQuery(id+"F0.wireOp",EDGE,"E8.MirrorCS"),sQuery(id+"F0.wireOp",EDGE,"E9.MirrorCS"),sQuery(id+"F0.wireOp",EDGE,"E10.MirrorCS"),sQuery(id+"F0.wireOp",EDGE,"E16"),sQuery(id+"F0.wireOp",EDGE,"E18"),sQuery(id+"F0.wireOp",EDGE,"E19.trimOffspring"),sQuery(id+"F0.wireOp",EDGE,"E22.MirrorCS"),sQuery(id+"F0.wireOp",EDGE,"E23"),sQuery(id+"F0.wireOp",EDGE,"E26.MirrorCS"),sQuery(id+"F0.wireOp",EDGE,"E27"),sQuery(id+"F0.wireOp",EDGE,"E28"),sQuery(id+"F0.wireOp",EDGE,"E29"),sQuery(id+"F0.wireOp",EDGE,"E30"),sQuery(id+"F0.wireOp",EDGE,"E31"),sQuery(id+"F0.wireOp",EDGE,"E32"),sQuery(id+"F0.wireOp",EDGE,"E33"),sQuery(id+"F0.wireOp",EDGE,"E34"),sQuery(id+"F0.wireOp",EDGE,"E35"),sQuery(id+"F0.wireOp",EDGE,"E36"),sQuery(id+"F0.wireOp",EDGE,"E37"),sQuery(id+"F0.wireOp",EDGE,"E38"),sQuery(id+"F0.wireOp",EDGE,"E39"),sQuery(id+"F0.wireOp",EDGE,"E42.trimOffspring"),sQuery(id+"F0.wireOp",EDGE,"E43"),sQuery(id+"F0.wireOp",EDGE,"E45.trimOffspring"),sQuery(id+"F0.wireOp",EDGE,"E46.trimOffspring"),sQuery(id+"F0.wireOp",EDGE,"E49.MirrorCS"),sQuery(id+"F0.wireOp",EDGE,"E50.MirrorCS"),sQuery(id+"F0.wireOp",EDGE,"E51.MirrorCS"),sQuery(id+"F0.wireOp",EDGE,"E52.MirrorCS"),sQuery(id+"F0.wireOp",EDGE,"E53.MirrorCS"),sQuery(id+"F0.wireOp",EDGE,"E54.MirrorCS"),sQuery(id+"F0.wireOp",EDGE,"E55.MirrorCS"),sQuery(id+"F0.wireOp",EDGE,"E56.MirrorCS"),sQuery(id+"F0.wireOp",EDGE,"E57.MirrorCS"),sQuery(id+"F0.wireOp",EDGE,"E58.MirrorCS"),sQuery(id+"F0.wireOp",EDGE,"E59.MirrorCS"),sQuery(id+"F0.wireOp",EDGE,"E60.MirrorCS"),sQuery(id+"F0.wireOp",EDGE,"E61.MirrorCS"),sQuery(id+"F0.wireOp",EDGE,"E62.MirrorCS"),sQuery(id+"F0.wireOp",EDGE,"E63.MirrorCS"),sQuery(id+"F0.wireOp",EDGE,"E64.MirrorCS"),sQuery(id+"F0.wireOp",EDGE,"E65.MirrorCS"),sQuery(id+"F0.wireOp",EDGE,"E67.0"),sQuery(id+"F0.wireOp",EDGE,"E68.0"),sQuery(id+"F0.wireOp",EDGE,"E69.trimOffspring"),sQuery(id+"F0.wireOp",EDGE,"E71.trimOffspring"),sQuery(id+"F0.wireOp",EDGE,"E76.trimOffspring"),sQuery(id+"F0.wireOp",EDGE,"E77.trimOffspring"),sQuery(id+"F0.wireOp",EDGE,"E78.trimOffspring"),sQuery(id+"F0.wireOp",EDGE,"E79.trimOffspring"),sQuery(id+"F0.wireOp",EDGE,"E80.sketch_text.stroke-0"),sQuery(id+"F0.wireOp",EDGE,"E80.sketch_text.stroke-1"),sQuery(id+"F0.wireOp",EDGE,"E80.sketch_text.stroke-2"),sQuery(id+"F0.wireOp",EDGE,"E80.sketch_text.stroke-3"),sQuery(id+"F0.wireOp",EDGE,"E80.sketch_text.stroke-4"),sQuery(id+"F0.wireOp",EDGE,"E80.sketch_text.stroke-5"),sQuery(id+"F0.wireOp",EDGE,"E80.sketch_text.stroke-6"),sQuery(id+"F0.wireOp",EDGE,"E80.sketch_text.stroke-7"),sQuery(id+"F0.wireOp",EDGE,"E80.sketch_text.stroke-8"),sQuery(id+"F0.wireOp",EDGE,"E80.sketch_text.stroke-9"),sQuery(id+"F0.wireOp",EDGE,"E80.sketch_text.stroke-10"),sQuery(id+"F0.wireOp",EDGE,"E80.sketch_text.stroke-11"),sQuery(id+"F0.wireOp",EDGE,"E81"),sQuery(id+"F0.wireOp",EDGE,"E82"),sQuery(id+"F0.wireOp",EDGE,"E83"),sQuery(id+"F0.wireOp",EDGE,"E84"),sQuery(id+"F0.wireOp",EDGE,"E85"),sQuery(id+"F0.wireOp",EDGE,"E87"),sQuery(id+"F0.wireOp",EDGE,"E88"),sQuery(id+"F0.wireOp",EDGE,"E89"),sQuery(id+"F0.wireOp",EDGE,"E90"),sQuery(id+"F0.wireOp",EDGE,"E91"),sQuery(id+"F0.wireOp",EDGE,"E93"),sQuery(id+"F0.wireOp",EDGE,"E94"),sQuery(id+"F0.wireOp",EDGE,"E95"),sQuery(id+"F0.wireOp",EDGE,"E96"),sQuery(id+"F0.wireOp",EDGE,"E97"),sQuery(id+"F0.wireOp",EDGE,"E98"),sQuery(id+"F0.wireOp",EDGE,"E99"),sQuery(id+"F0.wireOp",EDGE,"E100"),sQuery(id+"F0.wireOp",EDGE,"E101"),sQuery(id+"F0.wireOp",EDGE,"79a4f8d0-de25-4821-8878-42326f9d03c0"),sQuery(id+"F0.wireOp",EDGE,"E102"),sQuery(id+"F0.wireOp",EDGE,"E103"),sQuery(id+"F0.wireOp",EDGE,"E104"),sQuery(id+"F0.wireOp",EDGE,"E105"),sQuery(id+"F0.wireOp",EDGE,"E106"),sQuery(id+"F0.wireOp",EDGE,"E107"),sQuery(id+"F0.wireOp",EDGE,"E108"),sQuery(id+"F0.wireOp",EDGE,"E109"),sQuery(id+"F0.wireOp",EDGE,"E110"),sQuery(id+"F0.wireOp",EDGE,"E111"),sQuery(id+"F0.wireOp",EDGE,"E112"),sQuery(id+"F0.wireOp",EDGE,"E113"),sQuery(id+"F0.wireOp",EDGE,"E115"),sQuery(id+"F0.wireOp",EDGE,"E116"),sQuery(id+"F0.wireOp",EDGE,"E117"),sQuery(id+"F0.wireOp",EDGE,"E114"),sQuery(id+"F0.wireOp",EDGE,"E118"),sQuery(id+"F0.wireOp",EDGE,"E119"),sQuery(id+"F0.wireOp",EDGE,"E120"),sQuery(id+"F0.wireOp",EDGE,"E121"),sQuery(id+"F0.wireOp",EDGE,"E123"),sQuery(id+"F0.wireOp",EDGE,"E124"),sQuery(id+"F0.wireOp",EDGE,"E125"),sQuery(id+"F0.wireOp",EDGE,"E122"),sQuery(id+"F0.wireOp",EDGE,"E126"),sQuery(id+"F0.wireOp",EDGE,"E127"),sQuery(id+"F0.wireOp",EDGE,"E128"),sQuery(id+"F0.wireOp",EDGE,"E129"),sQuery(id+"F0.wireOp",EDGE,"E131"),sQuery(id+"F0.wireOp",EDGE,"E132"),sQuery(id+"F0.wireOp",EDGE,"E133"),sQuery(id+"F0.wireOp",EDGE,"E130"),sQuery(id+"F0.wireOp",EDGE,"E134"),sQuery(id+"F0.wireOp",EDGE,"E135"),sQuery(id+"F0.wireOp",EDGE,"E136"),sQuery(id+"F0.wireOp",EDGE,"E137"),sQuery(id+"F0.wireOp",EDGE,"E139"),sQuery(id+"F0.wireOp",EDGE,"E140"),sQuery(id+"F0.wireOp",EDGE,"E141"),sQuery(id+"F0.wireOp",EDGE,"E138"),sQuery(id+"F0.wireOp",EDGE,"E142"),sQuery(id+"F0.wireOp",EDGE,"E143"),sQuery(id+"F0.wireOp",EDGE,"E144"),sQuery(id+"F0.wireOp",EDGE,"E145"),sQuery(id+"F0.wireOp",EDGE,"E146.0"),sQuery(id+"F0.wireOp",EDGE,"E147.0"),sQuery(id+"F0.wireOp",EDGE,"E148.0"),sQuery(id+"F0.wireOp",EDGE,"E149.0"),sQuery(id+"F0.wireOp",EDGE,"E150"),sQuery(id+"F0.wireOp",EDGE,"E151"),sQuery(id+"F0.wireOp",EDGE,"E152"),sQuery(id+"F0.wireOp",EDGE,"E153"),sQuery(id+"F0.wireOp",EDGE,"E154"),sQuery(id+"F0.wireOp",EDGE,"E155"),sQuery(id+"F0.wireOp",EDGE,"E156"),sQuery(id+"F0.wireOp",EDGE,"E157"),sQuery(id+"F0.wireOp",EDGE,"E158"),sQuery(id+"F0.wireOp",EDGE,"E159"),sQuery(id+"F0.wireOp",EDGE,"E160"),sQuery(id+"F0.wireOp",EDGE,"E161"),sQuery(id+"F0.wireOp",EDGE,"E162"),sQuery(id+"F0.wireOp",EDGE,"E163"),sQuery(id+"F0.wireOp",EDGE,"E164"),sQuery(id+"F0.wireOp",EDGE,"E165"),sQuery(id+"F0.wireOp",EDGE,"E166"),sQuery(id+"F0.wireOp",EDGE,"E167"),sQuery(id+"F0.wireOp",EDGE,"E168"),sQuery(id+"F0.wireOp",EDGE,"E169"),sQuery(id+"F0.wireOp",EDGE,"E170"),sQuery(id+"F0.wireOp",EDGE,"E171"),sQuery(id+"F0.wireOp",EDGE,"E172.trimOffspring"),sQuery(id+"F0.wireOp",EDGE,"E173.trimOffspring"),sQuery(id+"F0.wireOp",EDGE,"E174.trimOffspring"),sQuery(id+"F0.wireOp",EDGE,"E175.trimOffspring"),sQuery(id+"F0.wireOp",EDGE,"E176.trimOffspring"),sQuery(id+"F0.wireOp",EDGE,"E177.trimOffspring"),sQuery(id+"F0.wireOp",EDGE,"E178.trimOffspring"),sQuery(id+"F0.wireOp",EDGE,"E179.trimOffspring"),sQuery(id+"F0.wireOp",EDGE,"E180.trimOffspring"),sQuery(id+"F0.wireOp",EDGE,"E181.trimOffspring"),sQuery(id+"F0.wireOp",EDGE,"E182.trimOffspring"),sQuery(id+"F0.wireOp",EDGE,"E183.trimOffspring"),sQuery(id+"F0.wireOp",EDGE,"E184.trimOffspring"),sQuery(id+"F0.wireOp",EDGE,"E185.trimOffspring"),sQuery(id+"F0.wireOp",EDGE,"E186.trimOffspring"),sQuery(id+"F0.wireOp",EDGE,"E187.trimOffspring"),sQuery(id+"F0.wireOp",EDGE,"E188.trimOffspring"),sQuery(id+"F0.wireOp",EDGE,"E190"),sQuery(id+"F0.wireOp",EDGE,"c9c110c2-e288-4740-844f-ba483bac1077"),sQuery(id+"F0.wireOp",EDGE,"E192.trimOffspring"),sQuery(id+"F0.wireOp",EDGE,"E194.trimOffspring"),sQuery(id+"F0.wireOp",EDGE,"E196"),sQuery(id+"F0.wireOp",EDGE,"E197"),sQuery(id+"F0.wireOp",EDGE,"E199.trimOffspring"),sQuery(id+"F0.wireOp",EDGE,"E201.trimOffspring"),sQuery(id+"F0.wireOp",EDGE,"E202.trimOffspring"),sQuery(id+"F0.wireOp",EDGE,"E203"),sQuery(id+"F0.wireOp",EDGE,"E206.trimOffspring"),sQuery(id+"F0.wireOp",EDGE,"E207.MirrorCS"),sQuery(id+"F0.wireOp",EDGE,"E208.MirrorCS"),sQuery(id+"F0.wireOp",EDGE,"E210.trimOffspring"),sQuery(id+"F0.wireOp",EDGE,"E211.trimOffspring"),sQuery(id+"F0.wireOp",EDGE,"E212.trimOffspring"),sQuery(id+"F0.wireOp",EDGE,"E213"),sQuery(id+"F0.wireOp",EDGE,"E214.0"),sQuery(id+"F0.wireOp",EDGE,"E215.MirrorCS"),sQuery(id+"F0.wireOp",EDGE,"E216.MirrorCS"),sQuery(id+"F0.wireOp",EDGE,"E217.MirrorCS"),sQuery(id+"F0.wireOp",EDGE,"E220.MirrorCS"),sQuery(id+"F0.wireOp",EDGE,"E222.0"),sQuery(id+"F0.wireOp",EDGE,"E223"),sQuery(id+"F0.wireOp",EDGE,"E224"),sQuery(id+"F0.wireOp",EDGE,"E225.MirrorCS"),sQuery(id+"F0.wireOp",EDGE,"E226.MirrorCS"),sQuery(id+"F0.wireOp",EDGE,"E227.MirrorCS"),sQuery(id+"F0.wireOp",EDGE,"E228"),sQuery(id+"F0.wireOp",EDGE,"E229.MirrorCS"),sQuery(id+"F0.wireOp",EDGE,"3dc38050-8edc-4d42-b04c-eaa21bf2e0a0.1"),sQuery(id+"F0.wireOp",EDGE,"e4574c0f-6a98-4f32-a32a-c108774d045c.0"),sQuery(id+"F0.wireOp",EDGE,"b95a71d1-bf8c-48bc-b8c3-2cf85ccb1f46.0"),sQuery(id+"F0.wireOp",EDGE,"6CdnfpsF-UXbz-2lWf-uGiN-xV6Clk6CIY2p"),sQuery(id+"F0.wireOp",EDGE,"KS5p9Uql-fqoi-JtGu-taWY-fYe7bwKlLbq6"),sQuery(id+"F0.wireOp",EDGE,"BpbhWuwh-fzUD-TgpT-2ZhU-je7DzOudBbx2"),sQuery(id+"F0.wireOp",EDGE,"R8LeVDRJ-FVDW-Pxxb-p9s3-yAxdAxvIfl0D"),sQuery(id+"F0.wireOp",EDGE,"u3q2aAR3-qywJ-678t-KDM3-BQjLNxFmgKIp"),sQuery(id+"F0.wireOp",EDGE,"1zP8rDmj-YOUN-6304-H82i-UbNZi5IW9xmn"),sQuery(id+"F0.wireOp",EDGE,"iAE1nxCd-g0cb-LlmT-wda9-sPFThKMbQK5z"),sQuery(id+"F0.wireOp",EDGE,"yTdGwwuI-YBCA-HG15-3odK-iPDKNbZLJZ6I"),sQuery(id+"F0.wireOp",EDGE,"Ms6NsYPA-J4kW-OH2l-AAyO-E9cR8JsWQ4yT"),sQuery(id+"F0.wireOp",EDGE,"WaIveHo5-VdCo-zpOC-L39Y-QGmYMk3Qi7xO")])],"isStart":false});
            var sketch = newSketch(context, id + "F4", { "sketchPlane" : qUnion([Q0])});
            skLineSegment(sketch, "E1115.0", {"start": v(4.65, -40.26) * mm, "end": v(20.64, -40.26) * mm});
            skArc(sketch, "E1116.0", {"start": v(-8.74, -45.01) * mm, "mid": v(-3.77, -45.27) * mm, "end": v(0.4, -42.58) * mm});
            skArc(sketch, "E1117.0", {"start": v(20.64, -40.26) * mm, "mid": v(23.33, -39.14) * mm, "end": v(24.45, -36.45) * mm});
            skArc(sketch, "E1118", {"start": v(4.65, -40.26) * mm, "mid": v(2.2, -41.12) * mm, "end": v(0.22, -42.8) * mm});
            skSolve(sketch);
        }
        {
            var Q0;
            Q0=makeQuery(id+"F1.opExtrude","SWEPT_FACE",FACE,{"disambiguationData":[OSD([sQuery(id+"F0.wireOp",EDGE,"E94")])]});
            var sketch = newSketch(context, id + "F5", { "sketchPlane" : qUnion([Q0])});
            skLineSegment(sketch, "E1119", {"start": v(24.45, -3.18) * mm, "end": v(24.45, 0) * mm});
            skLineSegment(sketch, "E1120", {"start": v(24.45, 0) * mm, "end": v(28.82, 0) * mm});
            skLineSegment(sketch, "E1121", {"start": v(24.45, -3.18) * mm, "end": v(26.99, 0) * mm});
            skLineSegment(sketch, "E1122", {"start": v(26.99, 0) * mm, "end": v(26.99, -3.18) * mm});
            skLineSegment(sketch, "E1123", {"start": v(26.99, -3.18) * mm, "end": v(24.45, -3.18) * mm});
            skSolve(sketch);
        }
        {
            var Q0;
            {var subQ0=sQuery(id+"F5.wireOp",EDGE,"E1122");Q0=makeQuery(id+"F5.imprint","IMPRINT",FACE,{"disambiguationData":[TD([[makeQuery(id+"F5.imprint","IMPRINT",EDGE,{"derivedFrom":subQ0}),-1.0]])]});}
            var Q1;
            {var subQ1=sQuery(id+"F5.wireOp",EDGE,"E1121");var subQ2=sQuery(id+"F0.wireOp",EDGE,"E94");var subQ4=makeQuery(id+"F1.opExtrude","SWEPT_EDGE",EDGE,{"disambiguationData":[OSD([sQuery(id+"F0.wireOp",EDGE,"E91"),subQ2])]});var subQ5=makeQuery(id+"F5.imprint","INTERSECT",VERTEX,{"derivedFrom":[subQ4,subQ1]});Q1=makeQuery(id+"F5.imprint","IMPRINT",FACE,{"disambiguationData":[TD([[makeQuery(id+"F5.imprint","IMPRINT",EDGE,{"disambiguationData":[TD([[subQ5,1.0]])],"derivedFrom":subQ1}),-1.0]])]});}
            var Q2;
            Q2=sQuery(id+"F4.wireOp",EDGE,"E1117.0");
            var Q3;
            Q3=sQuery(id+"F4.wireOp",EDGE,"E1115.0");
            var Q4;
            Q4=sQuery(id+"F4.wireOp",EDGE,"E1118");
            sweep(context, id + "F6", {"operationType" : NewBodyOperationType.REMOVE, "profiles" : qUnion([Q0, Q1]), "path" : qUnion([Q2, Q3, Q4])});
        }
    });
